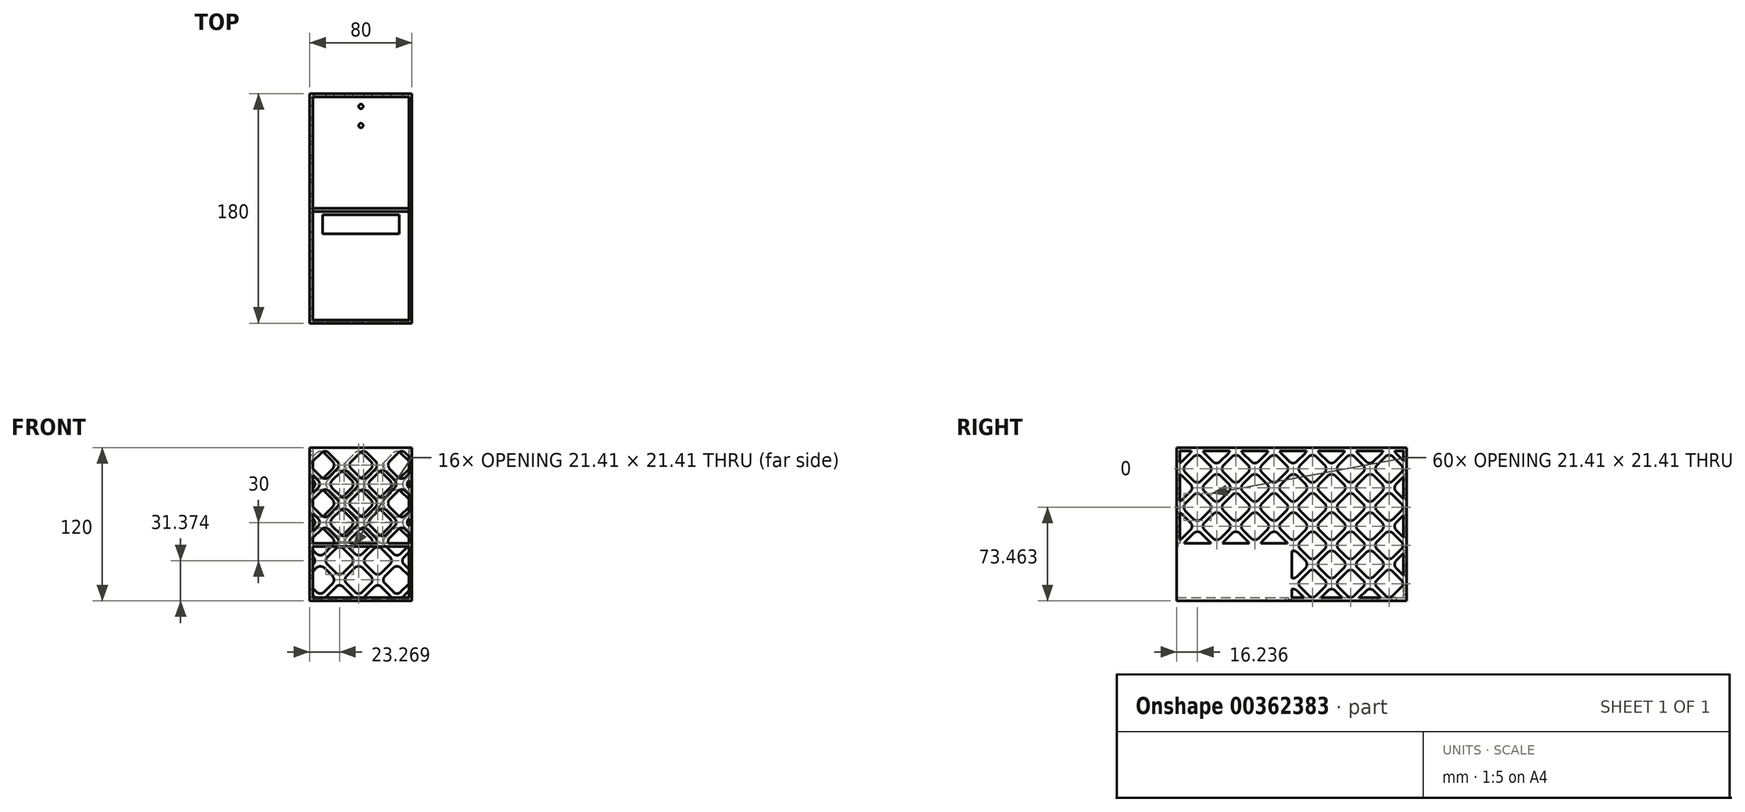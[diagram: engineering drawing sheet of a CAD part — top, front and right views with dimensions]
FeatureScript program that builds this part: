
annotation { "Feature Type Name" : "Feature", "Feature Type Description" : "" }
export const myFeature = defineFeature(function(context is Context, id is Id, definition is map)
    precondition{}
    {
        {
            var Q0;
            Q0=qCreatedBy(makeId("Right.planeOp"),FACE);
            var sketch = newSketch(context, id + "F0", { "sketchPlane" : qUnion([Q0])});
            skLineSegment(sketch, "E0.bottom", {"start": v(-62.96, 61.03) * mm, "end": v(117.04, 61.03) * mm});
            skLineSegment(sketch, "E0.top", {"start": v(-62.96, -58.97) * mm, "end": v(117.04, -58.97) * mm});
            skLineSegment(sketch, "E0.left", {"start": v(-62.96, 61.03) * mm, "end": v(-62.96, -58.97) * mm});
            skLineSegment(sketch, "E0.right", {"start": v(117.04, 61.03) * mm, "end": v(117.04, -58.97) * mm});
            skSolve(sketch);
        }
        {
            var Q0;
            Q0 = qSketchRegion(id + "F0", true);
            extrude(context, id + "F1", {"entities" : qUnion([Q0]), "depth" : 80 * mm});
        }
        {
            var Q0;
            Q0=makeQuery(id+"F1.opExtrude","CAP_FACE",FACE,{"disambiguationData":[OSD([sQuery(id+"F0.wireOp",EDGE,"E0.bottom"),sQuery(id+"F0.wireOp",EDGE,"E0.top"),sQuery(id+"F0.wireOp",EDGE,"E0.left"),sQuery(id+"F0.wireOp",EDGE,"E0.right")])],"isStart":false});
            var sketch = newSketch(context, id + "F2", { "sketchPlane" : qUnion([Q0])});
            skLineSegment(sketch, "E1.bottom", {"start": v(-60.46, 61.03) * mm, "end": v(114.54, 61.03) * mm});
            skLineSegment(sketch, "E1.top", {"start": v(-60.46, -13.97) * mm, "end": v(27.04, -13.97) * mm});
            skLineSegment(sketch, "E1.left", {"start": v(-60.46, 61.03) * mm, "end": v(-60.46, -13.97) * mm});
            skLineSegment(sketch, "E1.right", {"start": v(114.54, 61.03) * mm, "end": v(114.54, -13.97) * mm});
            skLineSegment(sketch, "E2.top", {"start": v(27.04, -56.47) * mm, "end": v(114.54, -56.47) * mm});
            skLineSegment(sketch, "E2.left", {"start": v(27.04, -13.97) * mm, "end": v(27.04, -56.47) * mm});
            skLineSegment(sketch, "E2.right", {"start": v(114.54, 15.9) * mm, "end": v(114.54, -56.47) * mm});
            skSolve(sketch);
        }
        {
            var Q0;
            Q0=makeQuery(id+"F2.imprint","IMPRINT",FACE,{"disambiguationData":[TD([[makeQuery(id+"F2.imprint","IMPRINT",EDGE,{"derivedFrom":sQuery(id+"F2.wireOp",EDGE,"E1.bottom")}),-1.0]])]});
            extrude(context, id + "F3", {"entities" : qUnion([Q0]), "operationType" : NewBodyOperationType.REMOVE, "oppositeDirection" : true, "depth" : 77.5 * mm, "hasSecondDirection" : true, "secondDirectionOppositeDirection" : false, "secondDirectionDepth" : -2.5 * mm});
        }
        {
            var Q0;
            Q0=makeQuery(id+"F1.opExtrude","SWEPT_FACE",FACE,{"disambiguationData":[OSD([sQuery(id+"F0.wireOp",EDGE,"E0.left")])]});
            var sketch = newSketch(context, id + "F4", { "sketchPlane" : qUnion([Q0])});
            skLineSegment(sketch, "E3.bottom", {"start": v(2.5, -16.47) * mm, "end": v(77.5, -16.47) * mm});
            skLineSegment(sketch, "E3.top", {"start": v(2.5, -56.47) * mm, "end": v(77.5, -56.47) * mm});
            skLineSegment(sketch, "E3.left", {"start": v(2.5, -16.47) * mm, "end": v(2.5, -56.47) * mm});
            skLineSegment(sketch, "E3.right", {"start": v(77.5, -16.47) * mm, "end": v(77.5, -56.47) * mm});
            skSolve(sketch);
        }
        {
            var Q0;
            Q0=makeQuery(id+"F4.imprint","IMPRINT",FACE,{"disambiguationData":[TD([[makeQuery(id+"F4.imprint","IMPRINT",EDGE,{"derivedFrom":sQuery(id+"F4.wireOp",EDGE,"E3.bottom")}),-1.0]])]});
            extrude(context, id + "F5", {"entities" : qUnion([Q0]), "operationType" : NewBodyOperationType.REMOVE, "oppositeDirection" : true, "depth" : 87.5 * mm});
        }
        {
            var Q0;
            Q0=makeQuery(id+"F1.opExtrude","CAP_FACE",FACE,{"disambiguationData":[OSD([sQuery(id+"F0.wireOp",EDGE,"E0.bottom"),sQuery(id+"F0.wireOp",EDGE,"E0.top"),sQuery(id+"F0.wireOp",EDGE,"E0.left"),sQuery(id+"F0.wireOp",EDGE,"E0.right")])],"isStart":false});
            var sketch = newSketch(context, id + "F6", { "sketchPlane" : qUnion([Q0])});
            skLineSegment(sketch, "E4", {"start": v(-49.58, 54.02) * mm, "end": v(-56.25, 47.34) * mm});
            skLineSegment(sketch, "E5", {"start": v(-56.25, 41.64) * mm, "end": v(-49.58, 34.97) * mm});
            skLineSegment(sketch, "E6", {"start": v(-43.87, 34.97) * mm, "end": v(-37.2, 41.64) * mm});
            skLineSegment(sketch, "E7", {"start": v(-37.2, 47.34) * mm, "end": v(-43.87, 54.02) * mm});
            skArc(sketch, "E8", {"start": v(-43.87, 54.02) * mm, "mid": v(-46.72, 55.2) * mm, "end": v(-49.58, 54.02) * mm});
            skArc(sketch, "E9", {"start": v(-37.2, 41.64) * mm, "mid": v(-36.02, 44.5) * mm, "end": v(-37.2, 47.34) * mm});
            skArc(sketch, "E10", {"start": v(-56.25, 47.34) * mm, "mid": v(-57.43, 44.5) * mm, "end": v(-56.25, 41.64) * mm});
            skArc(sketch, "E11", {"start": v(-49.58, 34.97) * mm, "mid": v(-46.72, 33.79) * mm, "end": v(-43.87, 34.97) * mm});
            skLineSegment(sketch, "E12", {"start": v(-64.58, 39.02) * mm, "end": v(-71.25, 32.34) * mm});
            skLineSegment(sketch, "E13", {"start": v(-71.25, 26.64) * mm, "end": v(-64.58, 19.97) * mm});
            skLineSegment(sketch, "E14", {"start": v(-58.87, 19.97) * mm, "end": v(-52.2, 26.64) * mm});
            skLineSegment(sketch, "E15", {"start": v(-52.2, 32.34) * mm, "end": v(-58.87, 39.02) * mm});
            skArc(sketch, "E16", {"start": v(-58.87, 39.02) * mm, "mid": v(-61.72, 40.2) * mm, "end": v(-64.58, 39.02) * mm});
            skArc(sketch, "E17", {"start": v(-52.2, 26.64) * mm, "mid": v(-51.02, 29.5) * mm, "end": v(-52.2, 32.34) * mm});
            skArc(sketch, "E18", {"start": v(-71.25, 32.34) * mm, "mid": v(-72.43, 29.5) * mm, "end": v(-71.25, 26.64) * mm});
            skArc(sketch, "E19", {"start": v(-64.58, 19.97) * mm, "mid": v(-61.72, 18.79) * mm, "end": v(-58.87, 19.97) * mm});
            skLineSegment(sketch, "E20.0.1.0", {"start": v(-37.2, 17.34) * mm, "end": v(-43.87, 24.02) * mm});
            skArc(sketch, "E20.0.1.1", {"start": v(-43.87, 24.02) * mm, "mid": v(-46.72, 25.2) * mm, "end": v(-49.58, 24.02) * mm});
            skLineSegment(sketch, "E20.0.1.2", {"start": v(-49.58, 24.02) * mm, "end": v(-56.25, 17.34) * mm});
            skArc(sketch, "E20.0.1.3", {"start": v(-56.25, 17.34) * mm, "mid": v(-57.43, 14.5) * mm, "end": v(-56.25, 11.64) * mm});
            skLineSegment(sketch, "E20.0.1.4", {"start": v(-56.25, 11.64) * mm, "end": v(-49.58, 4.97) * mm});
            skArc(sketch, "E20.0.1.5", {"start": v(-49.58, 4.97) * mm, "mid": v(-46.72, 3.79) * mm, "end": v(-43.87, 4.97) * mm});
            skLineSegment(sketch, "E20.0.1.6", {"start": v(-43.87, 4.97) * mm, "end": v(-37.2, 11.64) * mm});
            skArc(sketch, "E20.0.1.7", {"start": v(-37.2, 11.64) * mm, "mid": v(-36.02, 14.5) * mm, "end": v(-37.2, 17.34) * mm});
            skLineSegment(sketch, "E20.0.1.8", {"start": v(-52.2, 2.34) * mm, "end": v(-58.87, 9.02) * mm});
            skArc(sketch, "E20.0.1.9", {"start": v(-58.87, 9.02) * mm, "mid": v(-61.72, 10.2) * mm, "end": v(-64.58, 9.02) * mm});
            skLineSegment(sketch, "E20.0.1.10", {"start": v(-64.58, 9.02) * mm, "end": v(-71.25, 2.34) * mm});
            skArc(sketch, "E20.0.1.11", {"start": v(-71.25, 2.34) * mm, "mid": v(-72.43, -0.5) * mm, "end": v(-71.25, -3.36) * mm});
            skLineSegment(sketch, "E20.0.1.12", {"start": v(-71.25, -3.36) * mm, "end": v(-64.58, -10.03) * mm});
            skArc(sketch, "E20.0.1.13", {"start": v(-64.58, -10.03) * mm, "mid": v(-61.72, -11.21) * mm, "end": v(-58.87, -10.03) * mm});
            skLineSegment(sketch, "E20.0.1.14", {"start": v(-58.87, -10.03) * mm, "end": v(-52.2, -3.36) * mm});
            skArc(sketch, "E20.0.1.15", {"start": v(-52.2, -3.36) * mm, "mid": v(-51.02, -0.5) * mm, "end": v(-52.2, 2.34) * mm});
            skLineSegment(sketch, "E20.0.2.0", {"start": v(-37.2, -12.66) * mm, "end": v(-43.87, -5.98) * mm});
            skArc(sketch, "E20.0.2.1", {"start": v(-43.87, -5.98) * mm, "mid": v(-46.72, -4.8) * mm, "end": v(-49.58, -5.98) * mm});
            skLineSegment(sketch, "E20.0.2.2", {"start": v(-49.58, -5.98) * mm, "end": v(-56.25, -12.66) * mm});
            skArc(sketch, "E20.0.2.3", {"start": v(-56.25, -12.66) * mm, "mid": v(-57.43, -15.5) * mm, "end": v(-56.25, -18.36) * mm});
            skLineSegment(sketch, "E20.0.2.4", {"start": v(-56.25, -18.36) * mm, "end": v(-49.58, -25.03) * mm});
            skArc(sketch, "E20.0.2.5", {"start": v(-49.58, -25.03) * mm, "mid": v(-46.72, -26.21) * mm, "end": v(-43.87, -25.03) * mm});
            skLineSegment(sketch, "E20.0.2.6", {"start": v(-43.87, -25.03) * mm, "end": v(-37.2, -18.36) * mm});
            skArc(sketch, "E20.0.2.7", {"start": v(-37.2, -18.36) * mm, "mid": v(-36.02, -15.5) * mm, "end": v(-37.2, -12.66) * mm});
            skLineSegment(sketch, "E20.0.2.8", {"start": v(-52.2, -27.66) * mm, "end": v(-58.87, -20.98) * mm});
            skArc(sketch, "E20.0.2.9", {"start": v(-58.87, -20.98) * mm, "mid": v(-61.72, -19.8) * mm, "end": v(-64.58, -20.98) * mm});
            skLineSegment(sketch, "E20.0.2.10", {"start": v(-64.58, -20.98) * mm, "end": v(-71.25, -27.66) * mm});
            skArc(sketch, "E20.0.2.11", {"start": v(-71.25, -27.66) * mm, "mid": v(-72.43, -30.5) * mm, "end": v(-71.25, -33.36) * mm});
            skLineSegment(sketch, "E20.0.2.12", {"start": v(-71.25, -33.36) * mm, "end": v(-64.58, -40.03) * mm});
            skArc(sketch, "E20.0.2.13", {"start": v(-64.58, -40.03) * mm, "mid": v(-61.72, -41.21) * mm, "end": v(-58.87, -40.03) * mm});
            skLineSegment(sketch, "E20.0.2.14", {"start": v(-58.87, -40.03) * mm, "end": v(-52.2, -33.36) * mm});
            skArc(sketch, "E20.0.2.15", {"start": v(-52.2, -33.36) * mm, "mid": v(-51.02, -30.5) * mm, "end": v(-52.2, -27.66) * mm});
            skLineSegment(sketch, "E20.0.3.0", {"start": v(-37.2, -42.66) * mm, "end": v(-43.87, -35.98) * mm});
            skArc(sketch, "E20.0.3.1", {"start": v(-43.87, -35.98) * mm, "mid": v(-46.72, -34.8) * mm, "end": v(-49.58, -35.98) * mm});
            skLineSegment(sketch, "E20.0.3.2", {"start": v(-49.58, -35.98) * mm, "end": v(-56.25, -42.66) * mm});
            skArc(sketch, "E20.0.3.3", {"start": v(-56.25, -42.66) * mm, "mid": v(-57.43, -45.5) * mm, "end": v(-56.25, -48.36) * mm});
            skLineSegment(sketch, "E20.0.3.4", {"start": v(-56.25, -48.36) * mm, "end": v(-49.58, -55.03) * mm});
            skArc(sketch, "E20.0.3.5", {"start": v(-49.58, -55.03) * mm, "mid": v(-46.72, -56.21) * mm, "end": v(-43.87, -55.03) * mm});
            skLineSegment(sketch, "E20.0.3.6", {"start": v(-43.87, -55.03) * mm, "end": v(-37.2, -48.36) * mm});
            skArc(sketch, "E20.0.3.7", {"start": v(-37.2, -48.36) * mm, "mid": v(-36.02, -45.5) * mm, "end": v(-37.2, -42.66) * mm});
            skLineSegment(sketch, "E20.0.3.8", {"start": v(-52.2, -57.66) * mm, "end": v(-58.87, -50.98) * mm});
            skArc(sketch, "E20.0.3.9", {"start": v(-58.87, -50.98) * mm, "mid": v(-61.72, -49.8) * mm, "end": v(-64.58, -50.98) * mm});
            skLineSegment(sketch, "E20.0.3.10", {"start": v(-64.58, -50.98) * mm, "end": v(-71.25, -57.66) * mm});
            skArc(sketch, "E20.0.3.11", {"start": v(-71.25, -57.66) * mm, "mid": v(-72.43, -60.5) * mm, "end": v(-71.25, -63.36) * mm});
            skLineSegment(sketch, "E20.0.3.12", {"start": v(-71.25, -63.36) * mm, "end": v(-64.58, -70.03) * mm});
            skArc(sketch, "E20.0.3.13", {"start": v(-64.58, -70.03) * mm, "mid": v(-61.72, -71.21) * mm, "end": v(-58.87, -70.03) * mm});
            skLineSegment(sketch, "E20.0.3.14", {"start": v(-58.87, -70.03) * mm, "end": v(-52.2, -63.36) * mm});
            skArc(sketch, "E20.0.3.15", {"start": v(-52.2, -63.36) * mm, "mid": v(-51.02, -60.5) * mm, "end": v(-52.2, -57.66) * mm});
            skLineSegment(sketch, "E20.1.0.0", {"start": v(-7.2, 47.34) * mm, "end": v(-13.87, 54.02) * mm});
            skArc(sketch, "E20.1.0.1", {"start": v(-13.87, 54.02) * mm, "mid": v(-16.72, 55.2) * mm, "end": v(-19.58, 54.02) * mm});
            skLineSegment(sketch, "E20.1.0.2", {"start": v(-19.58, 54.02) * mm, "end": v(-26.25, 47.34) * mm});
            skArc(sketch, "E20.1.0.3", {"start": v(-26.25, 47.34) * mm, "mid": v(-27.43, 44.5) * mm, "end": v(-26.25, 41.64) * mm});
            skLineSegment(sketch, "E20.1.0.4", {"start": v(-26.25, 41.64) * mm, "end": v(-19.58, 34.97) * mm});
            skArc(sketch, "E20.1.0.5", {"start": v(-19.58, 34.97) * mm, "mid": v(-16.72, 33.79) * mm, "end": v(-13.87, 34.97) * mm});
            skLineSegment(sketch, "E20.1.0.6", {"start": v(-13.87, 34.97) * mm, "end": v(-7.2, 41.64) * mm});
            skArc(sketch, "E20.1.0.7", {"start": v(-7.2, 41.64) * mm, "mid": v(-6.02, 44.5) * mm, "end": v(-7.2, 47.34) * mm});
            skLineSegment(sketch, "E20.1.0.8", {"start": v(-22.2, 32.34) * mm, "end": v(-28.87, 39.02) * mm});
            skArc(sketch, "E20.1.0.9", {"start": v(-28.87, 39.02) * mm, "mid": v(-31.72, 40.2) * mm, "end": v(-34.58, 39.02) * mm});
            skLineSegment(sketch, "E20.1.0.10", {"start": v(-34.58, 39.02) * mm, "end": v(-41.25, 32.34) * mm});
            skArc(sketch, "E20.1.0.11", {"start": v(-41.25, 32.34) * mm, "mid": v(-42.43, 29.5) * mm, "end": v(-41.25, 26.64) * mm});
            skLineSegment(sketch, "E20.1.0.12", {"start": v(-41.25, 26.64) * mm, "end": v(-34.58, 19.97) * mm});
            skArc(sketch, "E20.1.0.13", {"start": v(-34.58, 19.97) * mm, "mid": v(-31.72, 18.79) * mm, "end": v(-28.87, 19.97) * mm});
            skLineSegment(sketch, "E20.1.0.14", {"start": v(-28.87, 19.97) * mm, "end": v(-22.2, 26.64) * mm});
            skArc(sketch, "E20.1.0.15", {"start": v(-22.2, 26.64) * mm, "mid": v(-21.02, 29.5) * mm, "end": v(-22.2, 32.34) * mm});
            skLineSegment(sketch, "E20.1.1.0", {"start": v(-7.2, 17.34) * mm, "end": v(-13.87, 24.02) * mm});
            skArc(sketch, "E20.1.1.1", {"start": v(-13.87, 24.02) * mm, "mid": v(-16.72, 25.2) * mm, "end": v(-19.58, 24.02) * mm});
            skLineSegment(sketch, "E20.1.1.2", {"start": v(-19.58, 24.02) * mm, "end": v(-26.25, 17.34) * mm});
            skArc(sketch, "E20.1.1.3", {"start": v(-26.25, 17.34) * mm, "mid": v(-27.43, 14.5) * mm, "end": v(-26.25, 11.64) * mm});
            skLineSegment(sketch, "E20.1.1.4", {"start": v(-26.25, 11.64) * mm, "end": v(-19.58, 4.97) * mm});
            skArc(sketch, "E20.1.1.5", {"start": v(-19.58, 4.97) * mm, "mid": v(-16.72, 3.79) * mm, "end": v(-13.87, 4.97) * mm});
            skLineSegment(sketch, "E20.1.1.6", {"start": v(-13.87, 4.97) * mm, "end": v(-7.2, 11.64) * mm});
            skArc(sketch, "E20.1.1.7", {"start": v(-7.2, 11.64) * mm, "mid": v(-6.02, 14.5) * mm, "end": v(-7.2, 17.34) * mm});
            skLineSegment(sketch, "E20.1.1.8", {"start": v(-22.2, 2.34) * mm, "end": v(-28.87, 9.02) * mm});
            skArc(sketch, "E20.1.1.9", {"start": v(-28.87, 9.02) * mm, "mid": v(-31.72, 10.2) * mm, "end": v(-34.58, 9.02) * mm});
            skLineSegment(sketch, "E20.1.1.10", {"start": v(-34.58, 9.02) * mm, "end": v(-41.25, 2.34) * mm});
            skArc(sketch, "E20.1.1.11", {"start": v(-41.25, 2.34) * mm, "mid": v(-42.43, -0.5) * mm, "end": v(-41.25, -3.36) * mm});
            skLineSegment(sketch, "E20.1.1.12", {"start": v(-41.25, -3.36) * mm, "end": v(-34.58, -10.03) * mm});
            skArc(sketch, "E20.1.1.13", {"start": v(-34.58, -10.03) * mm, "mid": v(-31.72, -11.21) * mm, "end": v(-28.87, -10.03) * mm});
            skLineSegment(sketch, "E20.1.1.14", {"start": v(-28.87, -10.03) * mm, "end": v(-22.2, -3.36) * mm});
            skArc(sketch, "E20.1.1.15", {"start": v(-22.2, -3.36) * mm, "mid": v(-21.02, -0.5) * mm, "end": v(-22.2, 2.34) * mm});
            skLineSegment(sketch, "E20.1.2.0", {"start": v(-7.2, -12.66) * mm, "end": v(-13.87, -5.98) * mm});
            skArc(sketch, "E20.1.2.1", {"start": v(-13.87, -5.98) * mm, "mid": v(-16.72, -4.8) * mm, "end": v(-19.58, -5.98) * mm});
            skLineSegment(sketch, "E20.1.2.2", {"start": v(-19.58, -5.98) * mm, "end": v(-26.25, -12.66) * mm});
            skArc(sketch, "E20.1.2.3", {"start": v(-26.25, -12.66) * mm, "mid": v(-27.43, -15.5) * mm, "end": v(-26.25, -18.36) * mm});
            skLineSegment(sketch, "E20.1.2.4", {"start": v(-26.25, -18.36) * mm, "end": v(-19.58, -25.03) * mm});
            skArc(sketch, "E20.1.2.5", {"start": v(-19.58, -25.03) * mm, "mid": v(-16.72, -26.21) * mm, "end": v(-13.87, -25.03) * mm});
            skLineSegment(sketch, "E20.1.2.6", {"start": v(-13.87, -25.03) * mm, "end": v(-7.2, -18.36) * mm});
            skArc(sketch, "E20.1.2.7", {"start": v(-7.2, -18.36) * mm, "mid": v(-6.02, -15.5) * mm, "end": v(-7.2, -12.66) * mm});
            skLineSegment(sketch, "E20.1.2.8", {"start": v(-22.2, -27.66) * mm, "end": v(-28.87, -20.98) * mm});
            skArc(sketch, "E20.1.2.9", {"start": v(-28.87, -20.98) * mm, "mid": v(-31.72, -19.8) * mm, "end": v(-34.58, -20.98) * mm});
            skLineSegment(sketch, "E20.1.2.10", {"start": v(-34.58, -20.98) * mm, "end": v(-41.25, -27.66) * mm});
            skArc(sketch, "E20.1.2.11", {"start": v(-41.25, -27.66) * mm, "mid": v(-42.43, -30.5) * mm, "end": v(-41.25, -33.36) * mm});
            skLineSegment(sketch, "E20.1.2.12", {"start": v(-41.25, -33.36) * mm, "end": v(-34.58, -40.03) * mm});
            skArc(sketch, "E20.1.2.13", {"start": v(-34.58, -40.03) * mm, "mid": v(-31.72, -41.21) * mm, "end": v(-28.87, -40.03) * mm});
            skLineSegment(sketch, "E20.1.2.14", {"start": v(-28.87, -40.03) * mm, "end": v(-22.2, -33.36) * mm});
            skArc(sketch, "E20.1.2.15", {"start": v(-22.2, -33.36) * mm, "mid": v(-21.02, -30.5) * mm, "end": v(-22.2, -27.66) * mm});
            skLineSegment(sketch, "E20.1.3.0", {"start": v(-7.2, -42.66) * mm, "end": v(-13.87, -35.98) * mm});
            skArc(sketch, "E20.1.3.1", {"start": v(-13.87, -35.98) * mm, "mid": v(-16.72, -34.8) * mm, "end": v(-19.58, -35.98) * mm});
            skLineSegment(sketch, "E20.1.3.2", {"start": v(-19.58, -35.98) * mm, "end": v(-26.25, -42.66) * mm});
            skArc(sketch, "E20.1.3.3", {"start": v(-26.25, -42.66) * mm, "mid": v(-27.43, -45.5) * mm, "end": v(-26.25, -48.36) * mm});
            skLineSegment(sketch, "E20.1.3.4", {"start": v(-26.25, -48.36) * mm, "end": v(-19.58, -55.03) * mm});
            skArc(sketch, "E20.1.3.5", {"start": v(-19.58, -55.03) * mm, "mid": v(-16.72, -56.21) * mm, "end": v(-13.87, -55.03) * mm});
            skLineSegment(sketch, "E20.1.3.6", {"start": v(-13.87, -55.03) * mm, "end": v(-7.2, -48.36) * mm});
            skArc(sketch, "E20.1.3.7", {"start": v(-7.2, -48.36) * mm, "mid": v(-6.02, -45.5) * mm, "end": v(-7.2, -42.66) * mm});
            skLineSegment(sketch, "E20.1.3.8", {"start": v(-22.2, -57.66) * mm, "end": v(-28.87, -50.98) * mm});
            skArc(sketch, "E20.1.3.9", {"start": v(-28.87, -50.98) * mm, "mid": v(-31.72, -49.8) * mm, "end": v(-34.58, -50.98) * mm});
            skLineSegment(sketch, "E20.1.3.10", {"start": v(-34.58, -50.98) * mm, "end": v(-41.25, -57.66) * mm});
            skArc(sketch, "E20.1.3.11", {"start": v(-41.25, -57.66) * mm, "mid": v(-42.43, -60.5) * mm, "end": v(-41.25, -63.36) * mm});
            skLineSegment(sketch, "E20.1.3.12", {"start": v(-41.25, -63.36) * mm, "end": v(-34.58, -70.03) * mm});
            skArc(sketch, "E20.1.3.13", {"start": v(-34.58, -70.03) * mm, "mid": v(-31.72, -71.21) * mm, "end": v(-28.87, -70.03) * mm});
            skLineSegment(sketch, "E20.1.3.14", {"start": v(-28.87, -70.03) * mm, "end": v(-22.2, -63.36) * mm});
            skArc(sketch, "E20.1.3.15", {"start": v(-22.2, -63.36) * mm, "mid": v(-21.02, -60.5) * mm, "end": v(-22.2, -57.66) * mm});
            skLineSegment(sketch, "E20.2.0.0", {"start": v(22.8, 47.34) * mm, "end": v(16.13, 54.02) * mm});
            skArc(sketch, "E20.2.0.1", {"start": v(16.13, 54.02) * mm, "mid": v(13.28, 55.2) * mm, "end": v(10.42, 54.02) * mm});
            skLineSegment(sketch, "E20.2.0.2", {"start": v(10.42, 54.02) * mm, "end": v(3.75, 47.34) * mm});
            skArc(sketch, "E20.2.0.3", {"start": v(3.75, 47.34) * mm, "mid": v(2.57, 44.5) * mm, "end": v(3.75, 41.64) * mm});
            skLineSegment(sketch, "E20.2.0.4", {"start": v(3.75, 41.64) * mm, "end": v(10.42, 34.97) * mm});
            skArc(sketch, "E20.2.0.5", {"start": v(10.42, 34.97) * mm, "mid": v(13.28, 33.79) * mm, "end": v(16.13, 34.97) * mm});
            skLineSegment(sketch, "E20.2.0.6", {"start": v(16.13, 34.97) * mm, "end": v(22.8, 41.64) * mm});
            skArc(sketch, "E20.2.0.7", {"start": v(22.8, 41.64) * mm, "mid": v(23.98, 44.5) * mm, "end": v(22.8, 47.34) * mm});
            skLineSegment(sketch, "E20.2.0.8", {"start": v(7.8, 32.34) * mm, "end": v(1.13, 39.02) * mm});
            skArc(sketch, "E20.2.0.9", {"start": v(1.13, 39.02) * mm, "mid": v(-1.72, 40.2) * mm, "end": v(-4.58, 39.02) * mm});
            skLineSegment(sketch, "E20.2.0.10", {"start": v(-4.58, 39.02) * mm, "end": v(-11.25, 32.34) * mm});
            skArc(sketch, "E20.2.0.11", {"start": v(-11.25, 32.34) * mm, "mid": v(-12.43, 29.5) * mm, "end": v(-11.25, 26.64) * mm});
            skLineSegment(sketch, "E20.2.0.12", {"start": v(-11.25, 26.64) * mm, "end": v(-4.58, 19.97) * mm});
            skArc(sketch, "E20.2.0.13", {"start": v(-4.58, 19.97) * mm, "mid": v(-1.72, 18.79) * mm, "end": v(1.13, 19.97) * mm});
            skLineSegment(sketch, "E20.2.0.14", {"start": v(1.13, 19.97) * mm, "end": v(7.8, 26.64) * mm});
            skArc(sketch, "E20.2.0.15", {"start": v(7.8, 26.64) * mm, "mid": v(8.98, 29.5) * mm, "end": v(7.8, 32.34) * mm});
            skLineSegment(sketch, "E20.2.1.0", {"start": v(22.8, 17.34) * mm, "end": v(16.13, 24.02) * mm});
            skArc(sketch, "E20.2.1.1", {"start": v(16.13, 24.02) * mm, "mid": v(13.28, 25.2) * mm, "end": v(10.42, 24.02) * mm});
            skLineSegment(sketch, "E20.2.1.2", {"start": v(10.42, 24.02) * mm, "end": v(3.75, 17.34) * mm});
            skArc(sketch, "E20.2.1.3", {"start": v(3.75, 17.34) * mm, "mid": v(2.57, 14.5) * mm, "end": v(3.75, 11.64) * mm});
            skLineSegment(sketch, "E20.2.1.4", {"start": v(3.75, 11.64) * mm, "end": v(10.42, 4.97) * mm});
            skArc(sketch, "E20.2.1.5", {"start": v(10.42, 4.97) * mm, "mid": v(13.28, 3.79) * mm, "end": v(16.13, 4.97) * mm});
            skLineSegment(sketch, "E20.2.1.6", {"start": v(16.13, 4.97) * mm, "end": v(22.8, 11.64) * mm});
            skArc(sketch, "E20.2.1.7", {"start": v(22.8, 11.64) * mm, "mid": v(23.98, 14.5) * mm, "end": v(22.8, 17.34) * mm});
            skLineSegment(sketch, "E20.2.1.8", {"start": v(7.8, 2.34) * mm, "end": v(1.13, 9.02) * mm});
            skArc(sketch, "E20.2.1.9", {"start": v(1.13, 9.02) * mm, "mid": v(-1.72, 10.2) * mm, "end": v(-4.58, 9.02) * mm});
            skLineSegment(sketch, "E20.2.1.10", {"start": v(-4.58, 9.02) * mm, "end": v(-11.25, 2.34) * mm});
            skArc(sketch, "E20.2.1.11", {"start": v(-11.25, 2.34) * mm, "mid": v(-12.43, -0.5) * mm, "end": v(-11.25, -3.36) * mm});
            skLineSegment(sketch, "E20.2.1.12", {"start": v(-11.25, -3.36) * mm, "end": v(-4.58, -10.03) * mm});
            skArc(sketch, "E20.2.1.13", {"start": v(-4.58, -10.03) * mm, "mid": v(-1.72, -11.21) * mm, "end": v(1.13, -10.03) * mm});
            skLineSegment(sketch, "E20.2.1.14", {"start": v(1.13, -10.03) * mm, "end": v(7.8, -3.36) * mm});
            skArc(sketch, "E20.2.1.15", {"start": v(7.8, -3.36) * mm, "mid": v(8.98, -0.5) * mm, "end": v(7.8, 2.34) * mm});
            skLineSegment(sketch, "E20.2.2.0", {"start": v(22.8, -12.66) * mm, "end": v(16.13, -5.98) * mm});
            skArc(sketch, "E20.2.2.1", {"start": v(16.13, -5.98) * mm, "mid": v(13.28, -4.8) * mm, "end": v(10.42, -5.98) * mm});
            skLineSegment(sketch, "E20.2.2.2", {"start": v(10.42, -5.98) * mm, "end": v(3.75, -12.66) * mm});
            skArc(sketch, "E20.2.2.3", {"start": v(3.75, -12.66) * mm, "mid": v(2.57, -15.5) * mm, "end": v(3.75, -18.36) * mm});
            skLineSegment(sketch, "E20.2.2.4", {"start": v(3.75, -18.36) * mm, "end": v(10.42, -25.03) * mm});
            skArc(sketch, "E20.2.2.5", {"start": v(10.42, -25.03) * mm, "mid": v(13.28, -26.21) * mm, "end": v(16.13, -25.03) * mm});
            skLineSegment(sketch, "E20.2.2.6", {"start": v(16.13, -25.03) * mm, "end": v(22.8, -18.36) * mm});
            skArc(sketch, "E20.2.2.7", {"start": v(22.8, -18.36) * mm, "mid": v(23.98, -15.5) * mm, "end": v(22.8, -12.66) * mm});
            skLineSegment(sketch, "E20.2.2.8", {"start": v(7.8, -27.66) * mm, "end": v(1.13, -20.98) * mm});
            skArc(sketch, "E20.2.2.9", {"start": v(1.13, -20.98) * mm, "mid": v(-1.72, -19.8) * mm, "end": v(-4.58, -20.98) * mm});
            skLineSegment(sketch, "E20.2.2.10", {"start": v(-4.58, -20.98) * mm, "end": v(-11.25, -27.66) * mm});
            skArc(sketch, "E20.2.2.11", {"start": v(-11.25, -27.66) * mm, "mid": v(-12.43, -30.5) * mm, "end": v(-11.25, -33.36) * mm});
            skLineSegment(sketch, "E20.2.2.12", {"start": v(-11.25, -33.36) * mm, "end": v(-4.58, -40.03) * mm});
            skArc(sketch, "E20.2.2.13", {"start": v(-4.58, -40.03) * mm, "mid": v(-1.72, -41.21) * mm, "end": v(1.13, -40.03) * mm});
            skLineSegment(sketch, "E20.2.2.14", {"start": v(1.13, -40.03) * mm, "end": v(7.8, -33.36) * mm});
            skArc(sketch, "E20.2.2.15", {"start": v(7.8, -33.36) * mm, "mid": v(8.98, -30.5) * mm, "end": v(7.8, -27.66) * mm});
            skLineSegment(sketch, "E20.2.3.0", {"start": v(22.8, -42.66) * mm, "end": v(16.13, -35.98) * mm});
            skArc(sketch, "E20.2.3.1", {"start": v(16.13, -35.98) * mm, "mid": v(13.28, -34.8) * mm, "end": v(10.42, -35.98) * mm});
            skLineSegment(sketch, "E20.2.3.2", {"start": v(10.42, -35.98) * mm, "end": v(3.75, -42.66) * mm});
            skArc(sketch, "E20.2.3.3", {"start": v(3.75, -42.66) * mm, "mid": v(2.57, -45.5) * mm, "end": v(3.75, -48.36) * mm});
            skLineSegment(sketch, "E20.2.3.4", {"start": v(3.75, -48.36) * mm, "end": v(10.42, -55.03) * mm});
            skArc(sketch, "E20.2.3.5", {"start": v(10.42, -55.03) * mm, "mid": v(13.28, -56.21) * mm, "end": v(16.13, -55.03) * mm});
            skLineSegment(sketch, "E20.2.3.6", {"start": v(16.13, -55.03) * mm, "end": v(22.8, -48.36) * mm});
            skArc(sketch, "E20.2.3.7", {"start": v(22.8, -48.36) * mm, "mid": v(23.98, -45.5) * mm, "end": v(22.8, -42.66) * mm});
            skLineSegment(sketch, "E20.2.3.8", {"start": v(7.8, -57.66) * mm, "end": v(1.13, -50.98) * mm});
            skArc(sketch, "E20.2.3.9", {"start": v(1.13, -50.98) * mm, "mid": v(-1.72, -49.8) * mm, "end": v(-4.58, -50.98) * mm});
            skLineSegment(sketch, "E20.2.3.10", {"start": v(-4.58, -50.98) * mm, "end": v(-11.25, -57.66) * mm});
            skArc(sketch, "E20.2.3.11", {"start": v(-11.25, -57.66) * mm, "mid": v(-12.43, -60.5) * mm, "end": v(-11.25, -63.36) * mm});
            skLineSegment(sketch, "E20.2.3.12", {"start": v(-11.25, -63.36) * mm, "end": v(-4.58, -70.03) * mm});
            skArc(sketch, "E20.2.3.13", {"start": v(-4.58, -70.03) * mm, "mid": v(-1.72, -71.21) * mm, "end": v(1.13, -70.03) * mm});
            skLineSegment(sketch, "E20.2.3.14", {"start": v(1.13, -70.03) * mm, "end": v(7.8, -63.36) * mm});
            skArc(sketch, "E20.2.3.15", {"start": v(7.8, -63.36) * mm, "mid": v(8.98, -60.5) * mm, "end": v(7.8, -57.66) * mm});
            skLineSegment(sketch, "E20.3.0.0", {"start": v(52.8, 47.34) * mm, "end": v(46.13, 54.02) * mm});
            skArc(sketch, "E20.3.0.1", {"start": v(46.13, 54.02) * mm, "mid": v(43.28, 55.2) * mm, "end": v(40.42, 54.02) * mm});
            skLineSegment(sketch, "E20.3.0.2", {"start": v(40.42, 54.02) * mm, "end": v(33.75, 47.34) * mm});
            skArc(sketch, "E20.3.0.3", {"start": v(33.75, 47.34) * mm, "mid": v(32.57, 44.5) * mm, "end": v(33.75, 41.64) * mm});
            skLineSegment(sketch, "E20.3.0.4", {"start": v(33.75, 41.64) * mm, "end": v(40.42, 34.97) * mm});
            skArc(sketch, "E20.3.0.5", {"start": v(40.42, 34.97) * mm, "mid": v(43.28, 33.79) * mm, "end": v(46.13, 34.97) * mm});
            skLineSegment(sketch, "E20.3.0.6", {"start": v(46.13, 34.97) * mm, "end": v(52.8, 41.64) * mm});
            skArc(sketch, "E20.3.0.7", {"start": v(52.8, 41.64) * mm, "mid": v(53.98, 44.5) * mm, "end": v(52.8, 47.34) * mm});
            skLineSegment(sketch, "E20.3.0.8", {"start": v(37.8, 32.34) * mm, "end": v(31.13, 39.02) * mm});
            skArc(sketch, "E20.3.0.9", {"start": v(31.13, 39.02) * mm, "mid": v(28.28, 40.2) * mm, "end": v(25.42, 39.02) * mm});
            skLineSegment(sketch, "E20.3.0.10", {"start": v(25.42, 39.02) * mm, "end": v(18.75, 32.34) * mm});
            skArc(sketch, "E20.3.0.11", {"start": v(18.75, 32.34) * mm, "mid": v(17.57, 29.5) * mm, "end": v(18.75, 26.64) * mm});
            skLineSegment(sketch, "E20.3.0.12", {"start": v(18.75, 26.64) * mm, "end": v(25.42, 19.97) * mm});
            skArc(sketch, "E20.3.0.13", {"start": v(25.42, 19.97) * mm, "mid": v(28.28, 18.79) * mm, "end": v(31.13, 19.97) * mm});
            skLineSegment(sketch, "E20.3.0.14", {"start": v(31.13, 19.97) * mm, "end": v(37.8, 26.64) * mm});
            skArc(sketch, "E20.3.0.15", {"start": v(37.8, 26.64) * mm, "mid": v(38.98, 29.5) * mm, "end": v(37.8, 32.34) * mm});
            skLineSegment(sketch, "E20.3.1.0", {"start": v(52.8, 17.34) * mm, "end": v(46.13, 24.02) * mm});
            skArc(sketch, "E20.3.1.1", {"start": v(46.13, 24.02) * mm, "mid": v(43.28, 25.2) * mm, "end": v(40.42, 24.02) * mm});
            skLineSegment(sketch, "E20.3.1.2", {"start": v(40.42, 24.02) * mm, "end": v(33.75, 17.34) * mm});
            skArc(sketch, "E20.3.1.3", {"start": v(33.75, 17.34) * mm, "mid": v(32.57, 14.5) * mm, "end": v(33.75, 11.64) * mm});
            skLineSegment(sketch, "E20.3.1.4", {"start": v(33.75, 11.64) * mm, "end": v(40.42, 4.97) * mm});
            skArc(sketch, "E20.3.1.5", {"start": v(40.42, 4.97) * mm, "mid": v(43.28, 3.79) * mm, "end": v(46.13, 4.97) * mm});
            skLineSegment(sketch, "E20.3.1.6", {"start": v(46.13, 4.97) * mm, "end": v(52.8, 11.64) * mm});
            skArc(sketch, "E20.3.1.7", {"start": v(52.8, 11.64) * mm, "mid": v(53.98, 14.5) * mm, "end": v(52.8, 17.34) * mm});
            skLineSegment(sketch, "E20.3.1.8", {"start": v(37.8, 2.34) * mm, "end": v(31.13, 9.02) * mm});
            skArc(sketch, "E20.3.1.9", {"start": v(31.13, 9.02) * mm, "mid": v(28.28, 10.2) * mm, "end": v(25.42, 9.02) * mm});
            skLineSegment(sketch, "E20.3.1.10", {"start": v(25.42, 9.02) * mm, "end": v(18.75, 2.34) * mm});
            skArc(sketch, "E20.3.1.11", {"start": v(18.75, 2.34) * mm, "mid": v(17.57, -0.5) * mm, "end": v(18.75, -3.36) * mm});
            skLineSegment(sketch, "E20.3.1.12", {"start": v(18.75, -3.36) * mm, "end": v(25.42, -10.03) * mm});
            skArc(sketch, "E20.3.1.13", {"start": v(25.42, -10.03) * mm, "mid": v(28.28, -11.21) * mm, "end": v(31.13, -10.03) * mm});
            skLineSegment(sketch, "E20.3.1.14", {"start": v(31.13, -10.03) * mm, "end": v(37.8, -3.36) * mm});
            skArc(sketch, "E20.3.1.15", {"start": v(37.8, -3.36) * mm, "mid": v(38.98, -0.5) * mm, "end": v(37.8, 2.34) * mm});
            skLineSegment(sketch, "E20.3.2.0", {"start": v(52.8, -12.66) * mm, "end": v(46.13, -5.98) * mm});
            skArc(sketch, "E20.3.2.1", {"start": v(46.13, -5.98) * mm, "mid": v(43.28, -4.8) * mm, "end": v(40.42, -5.98) * mm});
            skLineSegment(sketch, "E20.3.2.2", {"start": v(40.42, -5.98) * mm, "end": v(33.75, -12.66) * mm});
            skArc(sketch, "E20.3.2.3", {"start": v(33.75, -12.66) * mm, "mid": v(32.57, -15.5) * mm, "end": v(33.75, -18.36) * mm});
            skLineSegment(sketch, "E20.3.2.4", {"start": v(33.75, -18.36) * mm, "end": v(40.42, -25.03) * mm});
            skArc(sketch, "E20.3.2.5", {"start": v(40.42, -25.03) * mm, "mid": v(43.28, -26.21) * mm, "end": v(46.13, -25.03) * mm});
            skLineSegment(sketch, "E20.3.2.6", {"start": v(46.13, -25.03) * mm, "end": v(52.8, -18.36) * mm});
            skArc(sketch, "E20.3.2.7", {"start": v(52.8, -18.36) * mm, "mid": v(53.98, -15.5) * mm, "end": v(52.8, -12.66) * mm});
            skLineSegment(sketch, "E20.3.2.8", {"start": v(37.8, -27.66) * mm, "end": v(31.13, -20.98) * mm});
            skArc(sketch, "E20.3.2.9", {"start": v(31.13, -20.98) * mm, "mid": v(28.28, -19.8) * mm, "end": v(25.42, -20.98) * mm});
            skLineSegment(sketch, "E20.3.2.10", {"start": v(25.42, -20.98) * mm, "end": v(18.75, -27.66) * mm});
            skArc(sketch, "E20.3.2.11", {"start": v(18.75, -27.66) * mm, "mid": v(17.57, -30.5) * mm, "end": v(18.75, -33.36) * mm});
            skLineSegment(sketch, "E20.3.2.12", {"start": v(18.75, -33.36) * mm, "end": v(25.42, -40.03) * mm});
            skArc(sketch, "E20.3.2.13", {"start": v(25.42, -40.03) * mm, "mid": v(28.28, -41.21) * mm, "end": v(31.13, -40.03) * mm});
            skLineSegment(sketch, "E20.3.2.14", {"start": v(31.13, -40.03) * mm, "end": v(37.8, -33.36) * mm});
            skArc(sketch, "E20.3.2.15", {"start": v(37.8, -33.36) * mm, "mid": v(38.98, -30.5) * mm, "end": v(37.8, -27.66) * mm});
            skLineSegment(sketch, "E20.3.3.0", {"start": v(52.8, -42.66) * mm, "end": v(46.13, -35.98) * mm});
            skArc(sketch, "E20.3.3.1", {"start": v(46.13, -35.98) * mm, "mid": v(43.28, -34.8) * mm, "end": v(40.42, -35.98) * mm});
            skLineSegment(sketch, "E20.3.3.2", {"start": v(40.42, -35.98) * mm, "end": v(33.75, -42.66) * mm});
            skArc(sketch, "E20.3.3.3", {"start": v(33.75, -42.66) * mm, "mid": v(32.57, -45.5) * mm, "end": v(33.75, -48.36) * mm});
            skLineSegment(sketch, "E20.3.3.4", {"start": v(33.75, -48.36) * mm, "end": v(40.42, -55.03) * mm});
            skArc(sketch, "E20.3.3.5", {"start": v(40.42, -55.03) * mm, "mid": v(43.28, -56.21) * mm, "end": v(46.13, -55.03) * mm});
            skLineSegment(sketch, "E20.3.3.6", {"start": v(46.13, -55.03) * mm, "end": v(52.8, -48.36) * mm});
            skArc(sketch, "E20.3.3.7", {"start": v(52.8, -48.36) * mm, "mid": v(53.98, -45.5) * mm, "end": v(52.8, -42.66) * mm});
            skLineSegment(sketch, "E20.3.3.8", {"start": v(37.8, -57.66) * mm, "end": v(31.13, -50.98) * mm});
            skArc(sketch, "E20.3.3.9", {"start": v(31.13, -50.98) * mm, "mid": v(28.28, -49.8) * mm, "end": v(25.42, -50.98) * mm});
            skLineSegment(sketch, "E20.3.3.10", {"start": v(25.42, -50.98) * mm, "end": v(18.75, -57.66) * mm});
            skArc(sketch, "E20.3.3.11", {"start": v(18.75, -57.66) * mm, "mid": v(17.57, -60.5) * mm, "end": v(18.75, -63.36) * mm});
            skLineSegment(sketch, "E20.3.3.12", {"start": v(18.75, -63.36) * mm, "end": v(25.42, -70.03) * mm});
            skArc(sketch, "E20.3.3.13", {"start": v(25.42, -70.03) * mm, "mid": v(28.28, -71.21) * mm, "end": v(31.13, -70.03) * mm});
            skLineSegment(sketch, "E20.3.3.14", {"start": v(31.13, -70.03) * mm, "end": v(37.8, -63.36) * mm});
            skArc(sketch, "E20.3.3.15", {"start": v(37.8, -63.36) * mm, "mid": v(38.98, -60.5) * mm, "end": v(37.8, -57.66) * mm});
            skLineSegment(sketch, "E20.4.0.0", {"start": v(82.8, 47.34) * mm, "end": v(76.13, 54.02) * mm});
            skArc(sketch, "E20.4.0.1", {"start": v(76.13, 54.02) * mm, "mid": v(73.28, 55.2) * mm, "end": v(70.42, 54.02) * mm});
            skLineSegment(sketch, "E20.4.0.2", {"start": v(70.42, 54.02) * mm, "end": v(63.75, 47.34) * mm});
            skArc(sketch, "E20.4.0.3", {"start": v(63.75, 47.34) * mm, "mid": v(62.57, 44.5) * mm, "end": v(63.75, 41.64) * mm});
            skLineSegment(sketch, "E20.4.0.4", {"start": v(63.75, 41.64) * mm, "end": v(70.42, 34.97) * mm});
            skArc(sketch, "E20.4.0.5", {"start": v(70.42, 34.97) * mm, "mid": v(73.28, 33.79) * mm, "end": v(76.13, 34.97) * mm});
            skLineSegment(sketch, "E20.4.0.6", {"start": v(76.13, 34.97) * mm, "end": v(82.8, 41.64) * mm});
            skArc(sketch, "E20.4.0.7", {"start": v(82.8, 41.64) * mm, "mid": v(83.98, 44.5) * mm, "end": v(82.8, 47.34) * mm});
            skLineSegment(sketch, "E20.4.0.8", {"start": v(67.8, 32.34) * mm, "end": v(61.13, 39.02) * mm});
            skArc(sketch, "E20.4.0.9", {"start": v(61.13, 39.02) * mm, "mid": v(58.28, 40.2) * mm, "end": v(55.42, 39.02) * mm});
            skLineSegment(sketch, "E20.4.0.10", {"start": v(55.42, 39.02) * mm, "end": v(48.75, 32.34) * mm});
            skArc(sketch, "E20.4.0.11", {"start": v(48.75, 32.34) * mm, "mid": v(47.57, 29.5) * mm, "end": v(48.75, 26.64) * mm});
            skLineSegment(sketch, "E20.4.0.12", {"start": v(48.75, 26.64) * mm, "end": v(55.42, 19.97) * mm});
            skArc(sketch, "E20.4.0.13", {"start": v(55.42, 19.97) * mm, "mid": v(58.28, 18.79) * mm, "end": v(61.13, 19.97) * mm});
            skLineSegment(sketch, "E20.4.0.14", {"start": v(61.13, 19.97) * mm, "end": v(67.8, 26.64) * mm});
            skArc(sketch, "E20.4.0.15", {"start": v(67.8, 26.64) * mm, "mid": v(68.98, 29.5) * mm, "end": v(67.8, 32.34) * mm});
            skLineSegment(sketch, "E20.4.1.0", {"start": v(82.8, 17.34) * mm, "end": v(76.13, 24.02) * mm});
            skArc(sketch, "E20.4.1.1", {"start": v(76.13, 24.02) * mm, "mid": v(73.28, 25.2) * mm, "end": v(70.42, 24.02) * mm});
            skLineSegment(sketch, "E20.4.1.2", {"start": v(70.42, 24.02) * mm, "end": v(63.75, 17.34) * mm});
            skArc(sketch, "E20.4.1.3", {"start": v(63.75, 17.34) * mm, "mid": v(62.57, 14.5) * mm, "end": v(63.75, 11.64) * mm});
            skLineSegment(sketch, "E20.4.1.4", {"start": v(63.75, 11.64) * mm, "end": v(70.42, 4.97) * mm});
            skArc(sketch, "E20.4.1.5", {"start": v(70.42, 4.97) * mm, "mid": v(73.28, 3.79) * mm, "end": v(76.13, 4.97) * mm});
            skLineSegment(sketch, "E20.4.1.6", {"start": v(76.13, 4.97) * mm, "end": v(82.8, 11.64) * mm});
            skArc(sketch, "E20.4.1.7", {"start": v(82.8, 11.64) * mm, "mid": v(83.98, 14.5) * mm, "end": v(82.8, 17.34) * mm});
            skLineSegment(sketch, "E20.4.1.8", {"start": v(67.8, 2.34) * mm, "end": v(61.13, 9.02) * mm});
            skArc(sketch, "E20.4.1.9", {"start": v(61.13, 9.02) * mm, "mid": v(58.28, 10.2) * mm, "end": v(55.42, 9.02) * mm});
            skLineSegment(sketch, "E20.4.1.10", {"start": v(55.42, 9.02) * mm, "end": v(48.75, 2.34) * mm});
            skArc(sketch, "E20.4.1.11", {"start": v(48.75, 2.34) * mm, "mid": v(47.57, -0.5) * mm, "end": v(48.75, -3.36) * mm});
            skLineSegment(sketch, "E20.4.1.12", {"start": v(48.75, -3.36) * mm, "end": v(55.42, -10.03) * mm});
            skArc(sketch, "E20.4.1.13", {"start": v(55.42, -10.03) * mm, "mid": v(58.28, -11.21) * mm, "end": v(61.13, -10.03) * mm});
            skLineSegment(sketch, "E20.4.1.14", {"start": v(61.13, -10.03) * mm, "end": v(67.8, -3.36) * mm});
            skArc(sketch, "E20.4.1.15", {"start": v(67.8, -3.36) * mm, "mid": v(68.98, -0.5) * mm, "end": v(67.8, 2.34) * mm});
            skLineSegment(sketch, "E20.4.2.0", {"start": v(82.8, -12.66) * mm, "end": v(76.13, -5.98) * mm});
            skArc(sketch, "E20.4.2.1", {"start": v(76.13, -5.98) * mm, "mid": v(73.28, -4.8) * mm, "end": v(70.42, -5.98) * mm});
            skLineSegment(sketch, "E20.4.2.2", {"start": v(70.42, -5.98) * mm, "end": v(63.75, -12.66) * mm});
            skArc(sketch, "E20.4.2.3", {"start": v(63.75, -12.66) * mm, "mid": v(62.57, -15.5) * mm, "end": v(63.75, -18.36) * mm});
            skLineSegment(sketch, "E20.4.2.4", {"start": v(63.75, -18.36) * mm, "end": v(70.42, -25.03) * mm});
            skArc(sketch, "E20.4.2.5", {"start": v(70.42, -25.03) * mm, "mid": v(73.28, -26.21) * mm, "end": v(76.13, -25.03) * mm});
            skLineSegment(sketch, "E20.4.2.6", {"start": v(76.13, -25.03) * mm, "end": v(82.8, -18.36) * mm});
            skArc(sketch, "E20.4.2.7", {"start": v(82.8, -18.36) * mm, "mid": v(83.98, -15.5) * mm, "end": v(82.8, -12.66) * mm});
            skLineSegment(sketch, "E20.4.2.8", {"start": v(67.8, -27.66) * mm, "end": v(61.13, -20.98) * mm});
            skArc(sketch, "E20.4.2.9", {"start": v(61.13, -20.98) * mm, "mid": v(58.28, -19.8) * mm, "end": v(55.42, -20.98) * mm});
            skLineSegment(sketch, "E20.4.2.10", {"start": v(55.42, -20.98) * mm, "end": v(48.75, -27.66) * mm});
            skArc(sketch, "E20.4.2.11", {"start": v(48.75, -27.66) * mm, "mid": v(47.57, -30.5) * mm, "end": v(48.75, -33.36) * mm});
            skLineSegment(sketch, "E20.4.2.12", {"start": v(48.75, -33.36) * mm, "end": v(55.42, -40.03) * mm});
            skArc(sketch, "E20.4.2.13", {"start": v(55.42, -40.03) * mm, "mid": v(58.28, -41.21) * mm, "end": v(61.13, -40.03) * mm});
            skLineSegment(sketch, "E20.4.2.14", {"start": v(61.13, -40.03) * mm, "end": v(67.8, -33.36) * mm});
            skArc(sketch, "E20.4.2.15", {"start": v(67.8, -33.36) * mm, "mid": v(68.98, -30.5) * mm, "end": v(67.8, -27.66) * mm});
            skLineSegment(sketch, "E20.4.3.0", {"start": v(82.8, -42.66) * mm, "end": v(76.13, -35.98) * mm});
            skArc(sketch, "E20.4.3.1", {"start": v(76.13, -35.98) * mm, "mid": v(73.28, -34.8) * mm, "end": v(70.42, -35.98) * mm});
            skLineSegment(sketch, "E20.4.3.2", {"start": v(70.42, -35.98) * mm, "end": v(63.75, -42.66) * mm});
            skArc(sketch, "E20.4.3.3", {"start": v(63.75, -42.66) * mm, "mid": v(62.57, -45.5) * mm, "end": v(63.75, -48.36) * mm});
            skLineSegment(sketch, "E20.4.3.4", {"start": v(63.75, -48.36) * mm, "end": v(70.42, -55.03) * mm});
            skArc(sketch, "E20.4.3.5", {"start": v(70.42, -55.03) * mm, "mid": v(73.28, -56.21) * mm, "end": v(76.13, -55.03) * mm});
            skLineSegment(sketch, "E20.4.3.6", {"start": v(76.13, -55.03) * mm, "end": v(82.8, -48.36) * mm});
            skArc(sketch, "E20.4.3.7", {"start": v(82.8, -48.36) * mm, "mid": v(83.98, -45.5) * mm, "end": v(82.8, -42.66) * mm});
            skLineSegment(sketch, "E20.4.3.8", {"start": v(67.8, -57.66) * mm, "end": v(61.13, -50.98) * mm});
            skArc(sketch, "E20.4.3.9", {"start": v(61.13, -50.98) * mm, "mid": v(58.28, -49.8) * mm, "end": v(55.42, -50.98) * mm});
            skLineSegment(sketch, "E20.4.3.10", {"start": v(55.42, -50.98) * mm, "end": v(48.75, -57.66) * mm});
            skArc(sketch, "E20.4.3.11", {"start": v(48.75, -57.66) * mm, "mid": v(47.57, -60.5) * mm, "end": v(48.75, -63.36) * mm});
            skLineSegment(sketch, "E20.4.3.12", {"start": v(48.75, -63.36) * mm, "end": v(55.42, -70.03) * mm});
            skArc(sketch, "E20.4.3.13", {"start": v(55.42, -70.03) * mm, "mid": v(58.28, -71.21) * mm, "end": v(61.13, -70.03) * mm});
            skLineSegment(sketch, "E20.4.3.14", {"start": v(61.13, -70.03) * mm, "end": v(67.8, -63.36) * mm});
            skArc(sketch, "E20.4.3.15", {"start": v(67.8, -63.36) * mm, "mid": v(68.98, -60.5) * mm, "end": v(67.8, -57.66) * mm});
            skLineSegment(sketch, "E20.5.0.0", {"start": v(112.8, 47.34) * mm, "end": v(106.13, 54.02) * mm});
            skArc(sketch, "E20.5.0.1", {"start": v(106.13, 54.02) * mm, "mid": v(103.28, 55.2) * mm, "end": v(100.42, 54.02) * mm});
            skLineSegment(sketch, "E20.5.0.2", {"start": v(100.42, 54.02) * mm, "end": v(93.75, 47.34) * mm});
            skArc(sketch, "E20.5.0.3", {"start": v(93.75, 47.34) * mm, "mid": v(92.57, 44.5) * mm, "end": v(93.75, 41.64) * mm});
            skLineSegment(sketch, "E20.5.0.4", {"start": v(93.75, 41.64) * mm, "end": v(100.42, 34.97) * mm});
            skArc(sketch, "E20.5.0.5", {"start": v(100.42, 34.97) * mm, "mid": v(103.28, 33.79) * mm, "end": v(106.13, 34.97) * mm});
            skLineSegment(sketch, "E20.5.0.6", {"start": v(106.13, 34.97) * mm, "end": v(112.8, 41.64) * mm});
            skArc(sketch, "E20.5.0.7", {"start": v(112.8, 41.64) * mm, "mid": v(113.98, 44.5) * mm, "end": v(112.8, 47.34) * mm});
            skLineSegment(sketch, "E20.5.0.8", {"start": v(97.8, 32.34) * mm, "end": v(91.13, 39.02) * mm});
            skArc(sketch, "E20.5.0.9", {"start": v(91.13, 39.02) * mm, "mid": v(88.28, 40.2) * mm, "end": v(85.42, 39.02) * mm});
            skLineSegment(sketch, "E20.5.0.10", {"start": v(85.42, 39.02) * mm, "end": v(78.75, 32.34) * mm});
            skArc(sketch, "E20.5.0.11", {"start": v(78.75, 32.34) * mm, "mid": v(77.57, 29.5) * mm, "end": v(78.75, 26.64) * mm});
            skLineSegment(sketch, "E20.5.0.12", {"start": v(78.75, 26.64) * mm, "end": v(85.42, 19.97) * mm});
            skArc(sketch, "E20.5.0.13", {"start": v(85.42, 19.97) * mm, "mid": v(88.28, 18.79) * mm, "end": v(91.13, 19.97) * mm});
            skLineSegment(sketch, "E20.5.0.14", {"start": v(91.13, 19.97) * mm, "end": v(97.8, 26.64) * mm});
            skArc(sketch, "E20.5.0.15", {"start": v(97.8, 26.64) * mm, "mid": v(98.98, 29.5) * mm, "end": v(97.8, 32.34) * mm});
            skLineSegment(sketch, "E20.5.1.0", {"start": v(112.8, 17.34) * mm, "end": v(106.13, 24.02) * mm});
            skArc(sketch, "E20.5.1.1", {"start": v(106.13, 24.02) * mm, "mid": v(103.28, 25.2) * mm, "end": v(100.42, 24.02) * mm});
            skLineSegment(sketch, "E20.5.1.2", {"start": v(100.42, 24.02) * mm, "end": v(93.75, 17.34) * mm});
            skArc(sketch, "E20.5.1.3", {"start": v(93.75, 17.34) * mm, "mid": v(92.57, 14.5) * mm, "end": v(93.75, 11.64) * mm});
            skLineSegment(sketch, "E20.5.1.4", {"start": v(93.75, 11.64) * mm, "end": v(100.42, 4.97) * mm});
            skArc(sketch, "E20.5.1.5", {"start": v(100.42, 4.97) * mm, "mid": v(103.28, 3.79) * mm, "end": v(106.13, 4.97) * mm});
            skLineSegment(sketch, "E20.5.1.6", {"start": v(106.13, 4.97) * mm, "end": v(112.8, 11.64) * mm});
            skArc(sketch, "E20.5.1.7", {"start": v(112.8, 11.64) * mm, "mid": v(113.98, 14.5) * mm, "end": v(112.8, 17.34) * mm});
            skLineSegment(sketch, "E20.5.1.8", {"start": v(97.8, 2.34) * mm, "end": v(91.13, 9.02) * mm});
            skArc(sketch, "E20.5.1.9", {"start": v(91.13, 9.02) * mm, "mid": v(88.28, 10.2) * mm, "end": v(85.42, 9.02) * mm});
            skLineSegment(sketch, "E20.5.1.10", {"start": v(85.42, 9.02) * mm, "end": v(78.75, 2.34) * mm});
            skArc(sketch, "E20.5.1.11", {"start": v(78.75, 2.34) * mm, "mid": v(77.57, -0.5) * mm, "end": v(78.75, -3.36) * mm});
            skLineSegment(sketch, "E20.5.1.12", {"start": v(78.75, -3.36) * mm, "end": v(85.42, -10.03) * mm});
            skArc(sketch, "E20.5.1.13", {"start": v(85.42, -10.03) * mm, "mid": v(88.28, -11.21) * mm, "end": v(91.13, -10.03) * mm});
            skLineSegment(sketch, "E20.5.1.14", {"start": v(91.13, -10.03) * mm, "end": v(97.8, -3.36) * mm});
            skArc(sketch, "E20.5.1.15", {"start": v(97.8, -3.36) * mm, "mid": v(98.98, -0.5) * mm, "end": v(97.8, 2.34) * mm});
            skLineSegment(sketch, "E20.5.2.0", {"start": v(112.8, -12.66) * mm, "end": v(106.13, -5.98) * mm});
            skArc(sketch, "E20.5.2.1", {"start": v(106.13, -5.98) * mm, "mid": v(103.28, -4.8) * mm, "end": v(100.42, -5.98) * mm});
            skLineSegment(sketch, "E20.5.2.2", {"start": v(100.42, -5.98) * mm, "end": v(93.75, -12.66) * mm});
            skArc(sketch, "E20.5.2.3", {"start": v(93.75, -12.66) * mm, "mid": v(92.57, -15.5) * mm, "end": v(93.75, -18.36) * mm});
            skLineSegment(sketch, "E20.5.2.4", {"start": v(93.75, -18.36) * mm, "end": v(100.42, -25.03) * mm});
            skArc(sketch, "E20.5.2.5", {"start": v(100.42, -25.03) * mm, "mid": v(103.28, -26.21) * mm, "end": v(106.13, -25.03) * mm});
            skLineSegment(sketch, "E20.5.2.6", {"start": v(106.13, -25.03) * mm, "end": v(112.8, -18.36) * mm});
            skArc(sketch, "E20.5.2.7", {"start": v(112.8, -18.36) * mm, "mid": v(113.98, -15.5) * mm, "end": v(112.8, -12.66) * mm});
            skLineSegment(sketch, "E20.5.2.8", {"start": v(97.8, -27.66) * mm, "end": v(91.13, -20.98) * mm});
            skArc(sketch, "E20.5.2.9", {"start": v(91.13, -20.98) * mm, "mid": v(88.28, -19.8) * mm, "end": v(85.42, -20.98) * mm});
            skLineSegment(sketch, "E20.5.2.10", {"start": v(85.42, -20.98) * mm, "end": v(78.75, -27.66) * mm});
            skArc(sketch, "E20.5.2.11", {"start": v(78.75, -27.66) * mm, "mid": v(77.57, -30.5) * mm, "end": v(78.75, -33.36) * mm});
            skLineSegment(sketch, "E20.5.2.12", {"start": v(78.75, -33.36) * mm, "end": v(85.42, -40.03) * mm});
            skArc(sketch, "E20.5.2.13", {"start": v(85.42, -40.03) * mm, "mid": v(88.28, -41.21) * mm, "end": v(91.13, -40.03) * mm});
            skLineSegment(sketch, "E20.5.2.14", {"start": v(91.13, -40.03) * mm, "end": v(97.8, -33.36) * mm});
            skArc(sketch, "E20.5.2.15", {"start": v(97.8, -33.36) * mm, "mid": v(98.98, -30.5) * mm, "end": v(97.8, -27.66) * mm});
            skLineSegment(sketch, "E20.5.3.0", {"start": v(112.8, -42.66) * mm, "end": v(106.13, -35.98) * mm});
            skArc(sketch, "E20.5.3.1", {"start": v(106.13, -35.98) * mm, "mid": v(103.28, -34.8) * mm, "end": v(100.42, -35.98) * mm});
            skLineSegment(sketch, "E20.5.3.2", {"start": v(100.42, -35.98) * mm, "end": v(93.75, -42.66) * mm});
            skArc(sketch, "E20.5.3.3", {"start": v(93.75, -42.66) * mm, "mid": v(92.57, -45.5) * mm, "end": v(93.75, -48.36) * mm});
            skLineSegment(sketch, "E20.5.3.4", {"start": v(93.75, -48.36) * mm, "end": v(100.42, -55.03) * mm});
            skArc(sketch, "E20.5.3.5", {"start": v(100.42, -55.03) * mm, "mid": v(103.28, -56.21) * mm, "end": v(106.13, -55.03) * mm});
            skLineSegment(sketch, "E20.5.3.6", {"start": v(106.13, -55.03) * mm, "end": v(112.8, -48.36) * mm});
            skArc(sketch, "E20.5.3.7", {"start": v(112.8, -48.36) * mm, "mid": v(113.98, -45.5) * mm, "end": v(112.8, -42.66) * mm});
            skLineSegment(sketch, "E20.5.3.8", {"start": v(97.8, -57.66) * mm, "end": v(91.13, -50.98) * mm});
            skArc(sketch, "E20.5.3.9", {"start": v(91.13, -50.98) * mm, "mid": v(88.28, -49.8) * mm, "end": v(85.42, -50.98) * mm});
            skLineSegment(sketch, "E20.5.3.10", {"start": v(85.42, -50.98) * mm, "end": v(78.75, -57.66) * mm});
            skArc(sketch, "E20.5.3.11", {"start": v(78.75, -57.66) * mm, "mid": v(77.57, -60.5) * mm, "end": v(78.75, -63.36) * mm});
            skLineSegment(sketch, "E20.5.3.12", {"start": v(78.75, -63.36) * mm, "end": v(85.42, -70.03) * mm});
            skArc(sketch, "E20.5.3.13", {"start": v(85.42, -70.03) * mm, "mid": v(88.28, -71.21) * mm, "end": v(91.13, -70.03) * mm});
            skLineSegment(sketch, "E20.5.3.14", {"start": v(91.13, -70.03) * mm, "end": v(97.8, -63.36) * mm});
            skArc(sketch, "E20.5.3.15", {"start": v(97.8, -63.36) * mm, "mid": v(98.98, -60.5) * mm, "end": v(97.8, -57.66) * mm});
            skLineSegment(sketch, "E20.6.0.0", {"start": v(142.8, 47.34) * mm, "end": v(136.13, 54.02) * mm});
            skArc(sketch, "E20.6.0.1", {"start": v(136.13, 54.02) * mm, "mid": v(133.28, 55.2) * mm, "end": v(130.42, 54.02) * mm});
            skLineSegment(sketch, "E20.6.0.2", {"start": v(130.42, 54.02) * mm, "end": v(123.75, 47.34) * mm});
            skArc(sketch, "E20.6.0.3", {"start": v(123.75, 47.34) * mm, "mid": v(122.57, 44.5) * mm, "end": v(123.75, 41.64) * mm});
            skLineSegment(sketch, "E20.6.0.4", {"start": v(123.75, 41.64) * mm, "end": v(130.42, 34.97) * mm});
            skArc(sketch, "E20.6.0.5", {"start": v(130.42, 34.97) * mm, "mid": v(133.28, 33.79) * mm, "end": v(136.13, 34.97) * mm});
            skLineSegment(sketch, "E20.6.0.6", {"start": v(136.13, 34.97) * mm, "end": v(142.8, 41.64) * mm});
            skArc(sketch, "E20.6.0.7", {"start": v(142.8, 41.64) * mm, "mid": v(143.98, 44.5) * mm, "end": v(142.8, 47.34) * mm});
            skLineSegment(sketch, "E20.6.0.8", {"start": v(127.8, 32.34) * mm, "end": v(121.13, 39.02) * mm});
            skArc(sketch, "E20.6.0.9", {"start": v(121.13, 39.02) * mm, "mid": v(118.28, 40.2) * mm, "end": v(115.42, 39.02) * mm});
            skLineSegment(sketch, "E20.6.0.10", {"start": v(115.42, 39.02) * mm, "end": v(108.75, 32.34) * mm});
            skArc(sketch, "E20.6.0.11", {"start": v(108.75, 32.34) * mm, "mid": v(107.57, 29.5) * mm, "end": v(108.75, 26.64) * mm});
            skLineSegment(sketch, "E20.6.0.12", {"start": v(108.75, 26.64) * mm, "end": v(115.42, 19.97) * mm});
            skArc(sketch, "E20.6.0.13", {"start": v(115.42, 19.97) * mm, "mid": v(118.28, 18.79) * mm, "end": v(121.13, 19.97) * mm});
            skLineSegment(sketch, "E20.6.0.14", {"start": v(121.13, 19.97) * mm, "end": v(127.8, 26.64) * mm});
            skArc(sketch, "E20.6.0.15", {"start": v(127.8, 26.64) * mm, "mid": v(128.98, 29.5) * mm, "end": v(127.8, 32.34) * mm});
            skLineSegment(sketch, "E20.6.1.0", {"start": v(142.8, 17.34) * mm, "end": v(136.13, 24.02) * mm});
            skArc(sketch, "E20.6.1.1", {"start": v(136.13, 24.02) * mm, "mid": v(133.28, 25.2) * mm, "end": v(130.42, 24.02) * mm});
            skLineSegment(sketch, "E20.6.1.2", {"start": v(130.42, 24.02) * mm, "end": v(123.75, 17.34) * mm});
            skArc(sketch, "E20.6.1.3", {"start": v(123.75, 17.34) * mm, "mid": v(122.57, 14.5) * mm, "end": v(123.75, 11.64) * mm});
            skLineSegment(sketch, "E20.6.1.4", {"start": v(123.75, 11.64) * mm, "end": v(130.42, 4.97) * mm});
            skArc(sketch, "E20.6.1.5", {"start": v(130.42, 4.97) * mm, "mid": v(133.28, 3.79) * mm, "end": v(136.13, 4.97) * mm});
            skLineSegment(sketch, "E20.6.1.6", {"start": v(136.13, 4.97) * mm, "end": v(142.8, 11.64) * mm});
            skArc(sketch, "E20.6.1.7", {"start": v(142.8, 11.64) * mm, "mid": v(143.98, 14.5) * mm, "end": v(142.8, 17.34) * mm});
            skLineSegment(sketch, "E20.6.1.8", {"start": v(127.8, 2.34) * mm, "end": v(121.13, 9.02) * mm});
            skArc(sketch, "E20.6.1.9", {"start": v(121.13, 9.02) * mm, "mid": v(118.28, 10.2) * mm, "end": v(115.42, 9.02) * mm});
            skLineSegment(sketch, "E20.6.1.10", {"start": v(115.42, 9.02) * mm, "end": v(108.75, 2.34) * mm});
            skArc(sketch, "E20.6.1.11", {"start": v(108.75, 2.34) * mm, "mid": v(107.57, -0.5) * mm, "end": v(108.75, -3.36) * mm});
            skLineSegment(sketch, "E20.6.1.12", {"start": v(108.75, -3.36) * mm, "end": v(115.42, -10.03) * mm});
            skArc(sketch, "E20.6.1.13", {"start": v(115.42, -10.03) * mm, "mid": v(118.28, -11.21) * mm, "end": v(121.13, -10.03) * mm});
            skLineSegment(sketch, "E20.6.1.14", {"start": v(121.13, -10.03) * mm, "end": v(127.8, -3.36) * mm});
            skArc(sketch, "E20.6.1.15", {"start": v(127.8, -3.36) * mm, "mid": v(128.98, -0.5) * mm, "end": v(127.8, 2.34) * mm});
            skLineSegment(sketch, "E20.6.2.0", {"start": v(142.8, -12.66) * mm, "end": v(136.13, -5.98) * mm});
            skArc(sketch, "E20.6.2.1", {"start": v(136.13, -5.98) * mm, "mid": v(133.28, -4.8) * mm, "end": v(130.42, -5.98) * mm});
            skLineSegment(sketch, "E20.6.2.2", {"start": v(130.42, -5.98) * mm, "end": v(123.75, -12.66) * mm});
            skArc(sketch, "E20.6.2.3", {"start": v(123.75, -12.66) * mm, "mid": v(122.57, -15.5) * mm, "end": v(123.75, -18.36) * mm});
            skLineSegment(sketch, "E20.6.2.4", {"start": v(123.75, -18.36) * mm, "end": v(130.42, -25.03) * mm});
            skArc(sketch, "E20.6.2.5", {"start": v(130.42, -25.03) * mm, "mid": v(133.28, -26.21) * mm, "end": v(136.13, -25.03) * mm});
            skLineSegment(sketch, "E20.6.2.6", {"start": v(136.13, -25.03) * mm, "end": v(142.8, -18.36) * mm});
            skArc(sketch, "E20.6.2.7", {"start": v(142.8, -18.36) * mm, "mid": v(143.98, -15.5) * mm, "end": v(142.8, -12.66) * mm});
            skLineSegment(sketch, "E20.6.2.8", {"start": v(127.8, -27.66) * mm, "end": v(121.13, -20.98) * mm});
            skArc(sketch, "E20.6.2.9", {"start": v(121.13, -20.98) * mm, "mid": v(118.28, -19.8) * mm, "end": v(115.42, -20.98) * mm});
            skLineSegment(sketch, "E20.6.2.10", {"start": v(115.42, -20.98) * mm, "end": v(108.75, -27.66) * mm});
            skArc(sketch, "E20.6.2.11", {"start": v(108.75, -27.66) * mm, "mid": v(107.57, -30.5) * mm, "end": v(108.75, -33.36) * mm});
            skLineSegment(sketch, "E20.6.2.12", {"start": v(108.75, -33.36) * mm, "end": v(115.42, -40.03) * mm});
            skArc(sketch, "E20.6.2.13", {"start": v(115.42, -40.03) * mm, "mid": v(118.28, -41.21) * mm, "end": v(121.13, -40.03) * mm});
            skLineSegment(sketch, "E20.6.2.14", {"start": v(121.13, -40.03) * mm, "end": v(127.8, -33.36) * mm});
            skArc(sketch, "E20.6.2.15", {"start": v(127.8, -33.36) * mm, "mid": v(128.98, -30.5) * mm, "end": v(127.8, -27.66) * mm});
            skLineSegment(sketch, "E20.6.3.0", {"start": v(142.8, -42.66) * mm, "end": v(136.13, -35.98) * mm});
            skArc(sketch, "E20.6.3.1", {"start": v(136.13, -35.98) * mm, "mid": v(133.28, -34.8) * mm, "end": v(130.42, -35.98) * mm});
            skLineSegment(sketch, "E20.6.3.2", {"start": v(130.42, -35.98) * mm, "end": v(123.75, -42.66) * mm});
            skArc(sketch, "E20.6.3.3", {"start": v(123.75, -42.66) * mm, "mid": v(122.57, -45.5) * mm, "end": v(123.75, -48.36) * mm});
            skLineSegment(sketch, "E20.6.3.4", {"start": v(123.75, -48.36) * mm, "end": v(130.42, -55.03) * mm});
            skArc(sketch, "E20.6.3.5", {"start": v(130.42, -55.03) * mm, "mid": v(133.28, -56.21) * mm, "end": v(136.13, -55.03) * mm});
            skLineSegment(sketch, "E20.6.3.6", {"start": v(136.13, -55.03) * mm, "end": v(142.8, -48.36) * mm});
            skArc(sketch, "E20.6.3.7", {"start": v(142.8, -48.36) * mm, "mid": v(143.98, -45.5) * mm, "end": v(142.8, -42.66) * mm});
            skLineSegment(sketch, "E20.6.3.8", {"start": v(127.8, -57.66) * mm, "end": v(121.13, -50.98) * mm});
            skArc(sketch, "E20.6.3.9", {"start": v(121.13, -50.98) * mm, "mid": v(118.28, -49.8) * mm, "end": v(115.42, -50.98) * mm});
            skLineSegment(sketch, "E20.6.3.10", {"start": v(115.42, -50.98) * mm, "end": v(108.75, -57.66) * mm});
            skArc(sketch, "E20.6.3.11", {"start": v(108.75, -57.66) * mm, "mid": v(107.57, -60.5) * mm, "end": v(108.75, -63.36) * mm});
            skLineSegment(sketch, "E20.6.3.12", {"start": v(108.75, -63.36) * mm, "end": v(115.42, -70.03) * mm});
            skArc(sketch, "E20.6.3.13", {"start": v(115.42, -70.03) * mm, "mid": v(118.28, -71.21) * mm, "end": v(121.13, -70.03) * mm});
            skLineSegment(sketch, "E20.6.3.14", {"start": v(121.13, -70.03) * mm, "end": v(127.8, -63.36) * mm});
            skArc(sketch, "E20.6.3.15", {"start": v(127.8, -63.36) * mm, "mid": v(128.98, -60.5) * mm, "end": v(127.8, -57.66) * mm});
            skLineSegment(sketch, "E20.direction1", {"start": v(-37.2, 47.34) * mm, "end": v(-7.2, 47.34) * mm, "construction": true});
            skLineSegment(sketch, "E20.direction2", {"start": v(-37.2, 47.34) * mm, "end": v(-37.2, 17.34) * mm, "construction": true});
            skLineSegment(sketch, "E21", {"start": v(-60.46, 61.03) * mm, "end": v(-60.46, -13.97) * mm});
            skLineSegment(sketch, "E22", {"start": v(-60.46, -13.97) * mm, "end": v(27.06, -13.97) * mm});
            skLineSegment(sketch, "E23", {"start": v(27.06, -13.97) * mm, "end": v(27.06, -56.47) * mm});
            skLineSegment(sketch, "E24", {"start": v(27.06, -56.47) * mm, "end": v(114.54, -56.47) * mm});
            skLineSegment(sketch, "E25", {"start": v(114.54, -56.47) * mm, "end": v(114.54, 61.03) * mm});
            skLineSegment(sketch, "E26", {"start": v(114.54, 61.03) * mm, "end": v(-60.46, 61.03) * mm});
            skLineSegment(sketch, "E27.1.0.8", {"start": v(-52.54, 62.34) * mm, "end": v(-59.04, 68.85) * mm});
            skArc(sketch, "E27.1.0.9", {"start": v(-59.04, 68.85) * mm, "mid": v(-61.9, 70.08) * mm, "end": v(-64.74, 68.85) * mm});
            skLineSegment(sketch, "E27.1.0.10", {"start": v(-64.74, 68.85) * mm, "end": v(-71.25, 62.34) * mm});
            skArc(sketch, "E27.1.0.11", {"start": v(-71.25, 62.34) * mm, "mid": v(-72.43, 59.5) * mm, "end": v(-71.25, 56.64) * mm});
            skLineSegment(sketch, "E27.1.0.12", {"start": v(-71.25, 56.64) * mm, "end": v(-64.74, 50.14) * mm});
            skArc(sketch, "E27.1.0.13", {"start": v(-64.74, 50.14) * mm, "mid": v(-61.9, 48.96) * mm, "end": v(-59.04, 50.14) * mm});
            skLineSegment(sketch, "E27.1.0.14", {"start": v(-59.04, 50.14) * mm, "end": v(-52.54, 56.64) * mm});
            skArc(sketch, "E27.1.0.15", {"start": v(-52.54, 56.64) * mm, "mid": v(-51.36, 59.5) * mm, "end": v(-52.54, 62.34) * mm});
            skLineSegment(sketch, "E28.1.0.0", {"start": v(-34.74, 68.85) * mm, "end": v(-41.25, 62.34) * mm});
            skArc(sketch, "E28.1.0.1", {"start": v(-29.04, 68.85) * mm, "mid": v(-31.9, 70.08) * mm, "end": v(-34.74, 68.85) * mm});
            skLineSegment(sketch, "E28.1.0.2", {"start": v(-22.54, 62.34) * mm, "end": v(-29.04, 68.85) * mm});
            skArc(sketch, "E28.1.0.3", {"start": v(-22.54, 56.64) * mm, "mid": v(-21.36, 59.5) * mm, "end": v(-22.54, 62.34) * mm});
            skLineSegment(sketch, "E28.1.0.4", {"start": v(-29.04, 50.14) * mm, "end": v(-22.54, 56.64) * mm});
            skArc(sketch, "E28.1.0.5", {"start": v(-34.74, 50.14) * mm, "mid": v(-31.9, 48.96) * mm, "end": v(-29.04, 50.14) * mm});
            skLineSegment(sketch, "E28.1.0.6", {"start": v(-41.25, 56.64) * mm, "end": v(-34.74, 50.14) * mm});
            skArc(sketch, "E28.1.0.7", {"start": v(-41.25, 62.34) * mm, "mid": v(-42.43, 59.5) * mm, "end": v(-41.25, 56.64) * mm});
            skLineSegment(sketch, "E28.2.0.0", {"start": v(-4.74, 68.85) * mm, "end": v(-11.25, 62.34) * mm});
            skArc(sketch, "E28.2.0.1", {"start": v(0.96, 68.85) * mm, "mid": v(-1.9, 70.08) * mm, "end": v(-4.74, 68.85) * mm});
            skLineSegment(sketch, "E28.2.0.2", {"start": v(7.46, 62.34) * mm, "end": v(0.96, 68.85) * mm});
            skArc(sketch, "E28.2.0.3", {"start": v(7.46, 56.64) * mm, "mid": v(8.64, 59.5) * mm, "end": v(7.46, 62.34) * mm});
            skLineSegment(sketch, "E28.2.0.4", {"start": v(0.96, 50.14) * mm, "end": v(7.46, 56.64) * mm});
            skArc(sketch, "E28.2.0.5", {"start": v(-4.74, 50.14) * mm, "mid": v(-1.9, 48.96) * mm, "end": v(0.96, 50.14) * mm});
            skLineSegment(sketch, "E28.2.0.6", {"start": v(-11.25, 56.64) * mm, "end": v(-4.74, 50.14) * mm});
            skArc(sketch, "E28.2.0.7", {"start": v(-11.25, 62.34) * mm, "mid": v(-12.43, 59.5) * mm, "end": v(-11.25, 56.64) * mm});
            skLineSegment(sketch, "E28.3.0.0", {"start": v(25.26, 68.85) * mm, "end": v(18.75, 62.34) * mm});
            skArc(sketch, "E28.3.0.1", {"start": v(30.96, 68.85) * mm, "mid": v(28.1, 70.08) * mm, "end": v(25.26, 68.85) * mm});
            skLineSegment(sketch, "E28.3.0.2", {"start": v(37.46, 62.34) * mm, "end": v(30.96, 68.85) * mm});
            skArc(sketch, "E28.3.0.3", {"start": v(37.46, 56.64) * mm, "mid": v(38.64, 59.5) * mm, "end": v(37.46, 62.34) * mm});
            skLineSegment(sketch, "E28.3.0.4", {"start": v(30.96, 50.14) * mm, "end": v(37.46, 56.64) * mm});
            skArc(sketch, "E28.3.0.5", {"start": v(25.26, 50.14) * mm, "mid": v(28.1, 48.96) * mm, "end": v(30.96, 50.14) * mm});
            skLineSegment(sketch, "E28.3.0.6", {"start": v(18.75, 56.64) * mm, "end": v(25.26, 50.14) * mm});
            skArc(sketch, "E28.3.0.7", {"start": v(18.75, 62.34) * mm, "mid": v(17.57, 59.5) * mm, "end": v(18.75, 56.64) * mm});
            skLineSegment(sketch, "E28.4.0.0", {"start": v(55.26, 68.85) * mm, "end": v(48.75, 62.34) * mm});
            skArc(sketch, "E28.4.0.1", {"start": v(60.96, 68.85) * mm, "mid": v(58.1, 70.08) * mm, "end": v(55.26, 68.85) * mm});
            skLineSegment(sketch, "E28.4.0.2", {"start": v(67.46, 62.34) * mm, "end": v(60.96, 68.85) * mm});
            skArc(sketch, "E28.4.0.3", {"start": v(67.46, 56.64) * mm, "mid": v(68.64, 59.5) * mm, "end": v(67.46, 62.34) * mm});
            skLineSegment(sketch, "E28.4.0.4", {"start": v(60.96, 50.14) * mm, "end": v(67.46, 56.64) * mm});
            skArc(sketch, "E28.4.0.5", {"start": v(55.26, 50.14) * mm, "mid": v(58.1, 48.96) * mm, "end": v(60.96, 50.14) * mm});
            skLineSegment(sketch, "E28.4.0.6", {"start": v(48.75, 56.64) * mm, "end": v(55.26, 50.14) * mm});
            skArc(sketch, "E28.4.0.7", {"start": v(48.75, 62.34) * mm, "mid": v(47.57, 59.5) * mm, "end": v(48.75, 56.64) * mm});
            skLineSegment(sketch, "E28.5.0.0", {"start": v(85.26, 68.85) * mm, "end": v(78.75, 62.34) * mm});
            skArc(sketch, "E28.5.0.1", {"start": v(90.96, 68.85) * mm, "mid": v(88.1, 70.08) * mm, "end": v(85.26, 68.85) * mm});
            skLineSegment(sketch, "E28.5.0.2", {"start": v(97.46, 62.34) * mm, "end": v(90.96, 68.85) * mm});
            skArc(sketch, "E28.5.0.3", {"start": v(97.46, 56.64) * mm, "mid": v(98.64, 59.5) * mm, "end": v(97.46, 62.34) * mm});
            skLineSegment(sketch, "E28.5.0.4", {"start": v(90.96, 50.14) * mm, "end": v(97.46, 56.64) * mm});
            skArc(sketch, "E28.5.0.5", {"start": v(85.26, 50.14) * mm, "mid": v(88.1, 48.96) * mm, "end": v(90.96, 50.14) * mm});
            skLineSegment(sketch, "E28.5.0.6", {"start": v(78.75, 56.64) * mm, "end": v(85.26, 50.14) * mm});
            skArc(sketch, "E28.5.0.7", {"start": v(78.75, 62.34) * mm, "mid": v(77.57, 59.5) * mm, "end": v(78.75, 56.64) * mm});
            skLineSegment(sketch, "E28.6.0.0", {"start": v(115.26, 68.85) * mm, "end": v(108.75, 62.34) * mm});
            skArc(sketch, "E28.6.0.1", {"start": v(120.96, 68.85) * mm, "mid": v(118.1, 70.08) * mm, "end": v(115.26, 68.85) * mm});
            skLineSegment(sketch, "E28.6.0.2", {"start": v(127.46, 62.34) * mm, "end": v(120.96, 68.85) * mm});
            skArc(sketch, "E28.6.0.3", {"start": v(127.46, 56.64) * mm, "mid": v(128.64, 59.5) * mm, "end": v(127.46, 62.34) * mm});
            skLineSegment(sketch, "E28.6.0.4", {"start": v(120.96, 50.14) * mm, "end": v(127.46, 56.64) * mm});
            skArc(sketch, "E28.6.0.5", {"start": v(115.26, 50.14) * mm, "mid": v(118.1, 48.96) * mm, "end": v(120.96, 50.14) * mm});
            skLineSegment(sketch, "E28.6.0.6", {"start": v(108.75, 56.64) * mm, "end": v(115.26, 50.14) * mm});
            skArc(sketch, "E28.6.0.7", {"start": v(108.75, 62.34) * mm, "mid": v(107.57, 59.5) * mm, "end": v(108.75, 56.64) * mm});
            skLineSegment(sketch, "E28.direction1", {"start": v(-64.74, 50.14) * mm, "end": v(-34.74, 50.14) * mm, "construction": true});
            skLineSegment(sketch, "E29", {"start": v(-60.46, 58.53) * mm, "end": v(114.54, 58.53) * mm});
            skSolve(sketch);
        }
        {
            var Q0;
            Q0=makeQuery(id+"F6.imprint","IMPRINT",FACE,{"disambiguationData":[TD([[makeQuery(id+"F6.imprint","IMPRINT",EDGE,{"derivedFrom":sQuery(id+"F6.wireOp",EDGE,"E4")}),1.0]])]});
            var Q1;
            {var subQ4=sQuery(id+"F6.wireOp",EDGE,"E14");Q1=makeQuery(id+"F6.imprint","IMPRINT",FACE,{"disambiguationData":[TD([[makeQuery(id+"F6.imprint","IMPRINT",EDGE,{"derivedFrom":subQ4}),1.0]])]});}
            var Q2;
            {var subQ5=sQuery(id+"F6.wireOp",EDGE,"E20.0.1.8");Q2=makeQuery(id+"F6.imprint","IMPRINT",FACE,{"disambiguationData":[TD([[makeQuery(id+"F6.imprint","IMPRINT",EDGE,{"derivedFrom":subQ5}),1.0]])]});}
            var Q3;
            Q3=makeQuery(id+"F6.imprint","IMPRINT",FACE,{"disambiguationData":[TD([[makeQuery(id+"F6.imprint","IMPRINT",EDGE,{"derivedFrom":sQuery(id+"F6.wireOp",EDGE,"E20.0.1.0")}),1.0]])]});
            var Q4;
            Q4=makeQuery(id+"F6.imprint","IMPRINT",FACE,{"disambiguationData":[TD([[makeQuery(id+"F6.imprint","IMPRINT",EDGE,{"derivedFrom":sQuery(id+"F6.wireOp",EDGE,"E20.0.2.0")}),1.0]])]});
            var Q5;
            Q5=makeQuery(id+"F6.imprint","IMPRINT",FACE,{"disambiguationData":[TD([[makeQuery(id+"F6.imprint","IMPRINT",EDGE,{"derivedFrom":sQuery(id+"F6.wireOp",EDGE,"E20.1.2.0")}),1.0]])]});
            var Q6;
            Q6=makeQuery(id+"F6.imprint","IMPRINT",FACE,{"disambiguationData":[TD([[makeQuery(id+"F6.imprint","IMPRINT",EDGE,{"derivedFrom":sQuery(id+"F6.wireOp",EDGE,"E20.1.1.8")}),1.0]])]});
            var Q7;
            Q7=makeQuery(id+"F6.imprint","IMPRINT",FACE,{"disambiguationData":[TD([[makeQuery(id+"F6.imprint","IMPRINT",EDGE,{"derivedFrom":sQuery(id+"F6.wireOp",EDGE,"E20.1.1.0")}),1.0]])]});
            var Q8;
            Q8=makeQuery(id+"F6.imprint","IMPRINT",FACE,{"disambiguationData":[TD([[makeQuery(id+"F6.imprint","IMPRINT",EDGE,{"derivedFrom":sQuery(id+"F6.wireOp",EDGE,"E20.1.0.8")}),1.0]])]});
            var Q9;
            Q9=makeQuery(id+"F6.imprint","IMPRINT",FACE,{"disambiguationData":[TD([[makeQuery(id+"F6.imprint","IMPRINT",EDGE,{"derivedFrom":sQuery(id+"F6.wireOp",EDGE,"E20.1.0.0")}),1.0]])]});
            var Q10;
            Q10=makeQuery(id+"F6.imprint","IMPRINT",FACE,{"disambiguationData":[TD([[makeQuery(id+"F6.imprint","IMPRINT",EDGE,{"derivedFrom":sQuery(id+"F6.wireOp",EDGE,"E20.2.0.8")}),1.0]])]});
            var Q11;
            Q11=makeQuery(id+"F6.imprint","IMPRINT",FACE,{"disambiguationData":[TD([[makeQuery(id+"F6.imprint","IMPRINT",EDGE,{"derivedFrom":sQuery(id+"F6.wireOp",EDGE,"E20.2.0.0")}),1.0]])]});
            var Q12;
            Q12=makeQuery(id+"F6.imprint","IMPRINT",FACE,{"disambiguationData":[TD([[makeQuery(id+"F6.imprint","IMPRINT",EDGE,{"derivedFrom":sQuery(id+"F6.wireOp",EDGE,"E20.3.0.8")}),1.0]])]});
            var Q13;
            Q13=makeQuery(id+"F6.imprint","IMPRINT",FACE,{"disambiguationData":[TD([[makeQuery(id+"F6.imprint","IMPRINT",EDGE,{"derivedFrom":sQuery(id+"F6.wireOp",EDGE,"E20.2.1.0")}),1.0]])]});
            var Q14;
            Q14=makeQuery(id+"F6.imprint","IMPRINT",FACE,{"disambiguationData":[TD([[makeQuery(id+"F6.imprint","IMPRINT",EDGE,{"derivedFrom":sQuery(id+"F6.wireOp",EDGE,"E20.2.1.8")}),1.0]])]});
            var Q15;
            Q15=makeQuery(id+"F6.imprint","IMPRINT",FACE,{"disambiguationData":[TD([[makeQuery(id+"F6.imprint","IMPRINT",EDGE,{"derivedFrom":sQuery(id+"F6.wireOp",EDGE,"E20.2.2.0")}),1.0]])]});
            var Q16;
            Q16=makeQuery(id+"F6.imprint","IMPRINT",FACE,{"disambiguationData":[TD([[makeQuery(id+"F6.imprint","IMPRINT",EDGE,{"derivedFrom":sQuery(id+"F6.wireOp",EDGE,"E20.3.2.8")}),1.0]])]});
            var Q17;
            Q17=makeQuery(id+"F6.imprint","IMPRINT",FACE,{"disambiguationData":[TD([[makeQuery(id+"F6.imprint","IMPRINT",EDGE,{"derivedFrom":sQuery(id+"F6.wireOp",EDGE,"E20.3.2.0")}),1.0]])]});
            var Q18;
            Q18=makeQuery(id+"F6.imprint","IMPRINT",FACE,{"disambiguationData":[TD([[makeQuery(id+"F6.imprint","IMPRINT",EDGE,{"derivedFrom":sQuery(id+"F6.wireOp",EDGE,"E20.3.3.0")}),1.0]])]});
            var Q19;
            {var subQ0=sQuery(id+"F6.wireOp",EDGE,"E20.3.3.9");var subQ1=sQuery(id+"F6.wireOp",EDGE,"E20.3.3.8");var subQ2=makeQuery(id+"F6.imprint","INTERSECT",VERTEX,{"derivedFrom":[subQ1,subQ0]});Q19=makeQuery(id+"F6.imprint","IMPRINT",FACE,{"disambiguationData":[TD([[makeQuery(id+"F6.imprint","IMPRINT",EDGE,{"disambiguationData":[TD([[subQ2,1.0]])],"derivedFrom":subQ1}),1.0]])]});}
            var Q20;
            {var subQ0=sQuery(id+"F6.wireOp",EDGE,"E20.4.3.9");Q20=makeQuery(id+"F6.imprint","IMPRINT",FACE,{"disambiguationData":[TD([[makeQuery(id+"F6.imprint","IMPRINT",EDGE,{"derivedFrom":subQ0}),1.0]])]});}
            var Q21;
            Q21=makeQuery(id+"F6.imprint","IMPRINT",FACE,{"disambiguationData":[TD([[makeQuery(id+"F6.imprint","IMPRINT",EDGE,{"derivedFrom":sQuery(id+"F6.wireOp",EDGE,"E20.4.3.0")}),1.0]])]});
            var Q22;
            {var subQ0=sQuery(id+"F6.wireOp",EDGE,"E20.5.3.9");Q22=makeQuery(id+"F6.imprint","IMPRINT",FACE,{"disambiguationData":[TD([[makeQuery(id+"F6.imprint","IMPRINT",EDGE,{"derivedFrom":subQ0}),1.0]])]});}
            var Q23;
            Q23=makeQuery(id+"F6.imprint","IMPRINT",FACE,{"disambiguationData":[TD([[makeQuery(id+"F6.imprint","IMPRINT",EDGE,{"derivedFrom":sQuery(id+"F6.wireOp",EDGE,"E20.5.3.0")}),1.0]])]});
            var Q24;
            {var subQ0=sQuery(id+"F6.wireOp",EDGE,"E20.6.2.11");Q24=makeQuery(id+"F6.imprint","IMPRINT",FACE,{"disambiguationData":[TD([[makeQuery(id+"F6.imprint","IMPRINT",EDGE,{"derivedFrom":subQ0}),1.0]])]});}
            var Q25;
            Q25=makeQuery(id+"F6.imprint","IMPRINT",FACE,{"disambiguationData":[TD([[makeQuery(id+"F6.imprint","IMPRINT",EDGE,{"derivedFrom":sQuery(id+"F6.wireOp",EDGE,"E20.5.2.0")}),1.0]])]});
            var Q26;
            Q26=makeQuery(id+"F6.imprint","IMPRINT",FACE,{"disambiguationData":[TD([[makeQuery(id+"F6.imprint","IMPRINT",EDGE,{"derivedFrom":sQuery(id+"F6.wireOp",EDGE,"E20.5.2.8")}),1.0]])]});
            var Q27;
            Q27=makeQuery(id+"F6.imprint","IMPRINT",FACE,{"disambiguationData":[TD([[makeQuery(id+"F6.imprint","IMPRINT",EDGE,{"derivedFrom":sQuery(id+"F6.wireOp",EDGE,"E20.4.2.8")}),1.0]])]});
            var Q28;
            Q28=makeQuery(id+"F6.imprint","IMPRINT",FACE,{"disambiguationData":[TD([[makeQuery(id+"F6.imprint","IMPRINT",EDGE,{"derivedFrom":sQuery(id+"F6.wireOp",EDGE,"E20.3.1.8")}),1.0]])]});
            var Q29;
            Q29=makeQuery(id+"F6.imprint","IMPRINT",FACE,{"disambiguationData":[TD([[makeQuery(id+"F6.imprint","IMPRINT",EDGE,{"derivedFrom":sQuery(id+"F6.wireOp",EDGE,"E20.4.1.8")}),1.0]])]});
            var Q30;
            Q30=makeQuery(id+"F6.imprint","IMPRINT",FACE,{"disambiguationData":[TD([[makeQuery(id+"F6.imprint","IMPRINT",EDGE,{"derivedFrom":sQuery(id+"F6.wireOp",EDGE,"E20.3.1.0")}),1.0]])]});
            var Q31;
            Q31=makeQuery(id+"F6.imprint","IMPRINT",FACE,{"disambiguationData":[TD([[makeQuery(id+"F6.imprint","IMPRINT",EDGE,{"derivedFrom":sQuery(id+"F6.wireOp",EDGE,"E20.3.0.0")}),1.0]])]});
            var Q32;
            Q32=makeQuery(id+"F6.imprint","IMPRINT",FACE,{"disambiguationData":[TD([[makeQuery(id+"F6.imprint","IMPRINT",EDGE,{"derivedFrom":sQuery(id+"F6.wireOp",EDGE,"E20.4.0.8")}),1.0]])]});
            var Q33;
            Q33=makeQuery(id+"F6.imprint","IMPRINT",FACE,{"disambiguationData":[TD([[makeQuery(id+"F6.imprint","IMPRINT",EDGE,{"derivedFrom":sQuery(id+"F6.wireOp",EDGE,"E20.4.0.0")}),1.0]])]});
            var Q34;
            Q34=makeQuery(id+"F6.imprint","IMPRINT",FACE,{"disambiguationData":[TD([[makeQuery(id+"F6.imprint","IMPRINT",EDGE,{"derivedFrom":sQuery(id+"F6.wireOp",EDGE,"E20.4.1.0")}),1.0]])]});
            var Q35;
            Q35=makeQuery(id+"F6.imprint","IMPRINT",FACE,{"disambiguationData":[TD([[makeQuery(id+"F6.imprint","IMPRINT",EDGE,{"derivedFrom":sQuery(id+"F6.wireOp",EDGE,"E20.5.0.8")}),1.0]])]});
            var Q36;
            Q36=makeQuery(id+"F6.imprint","IMPRINT",FACE,{"disambiguationData":[TD([[makeQuery(id+"F6.imprint","IMPRINT",EDGE,{"derivedFrom":sQuery(id+"F6.wireOp",EDGE,"E20.5.0.0")}),1.0]])]});
            var Q37;
            Q37=makeQuery(id+"F6.imprint","IMPRINT",FACE,{"disambiguationData":[TD([[makeQuery(id+"F6.imprint","IMPRINT",EDGE,{"derivedFrom":sQuery(id+"F6.wireOp",EDGE,"E20.5.1.0")}),1.0]])]});
            var Q38;
            {var subQ0=sQuery(id+"F6.wireOp",EDGE,"E20.6.0.11");Q38=makeQuery(id+"F6.imprint","IMPRINT",FACE,{"disambiguationData":[TD([[makeQuery(id+"F6.imprint","IMPRINT",EDGE,{"derivedFrom":subQ0}),1.0]])]});}
            var Q39;
            Q39=makeQuery(id+"F6.imprint","IMPRINT",FACE,{"disambiguationData":[TD([[makeQuery(id+"F6.imprint","IMPRINT",EDGE,{"derivedFrom":sQuery(id+"F6.wireOp",EDGE,"E20.5.1.8")}),1.0]])]});
            var Q40;
            Q40=makeQuery(id+"F6.imprint","IMPRINT",FACE,{"disambiguationData":[TD([[makeQuery(id+"F6.imprint","IMPRINT",EDGE,{"derivedFrom":sQuery(id+"F6.wireOp",EDGE,"E20.4.2.0")}),1.0]])]});
            var Q41;
            {var subQ0=sQuery(id+"F6.wireOp",EDGE,"E20.6.1.11");Q41=makeQuery(id+"F6.imprint","IMPRINT",FACE,{"disambiguationData":[TD([[makeQuery(id+"F6.imprint","IMPRINT",EDGE,{"derivedFrom":subQ0}),1.0]])]});}
            var Q42;
            {var subQ1=sQuery(id+"F6.wireOp",EDGE,"E27.1.0.14");Q42=makeQuery(id+"F6.imprint","IMPRINT",FACE,{"disambiguationData":[TD([[makeQuery(id+"F6.imprint","IMPRINT",EDGE,{"derivedFrom":subQ1}),1.0]])]});}
            var Q43;
            {var subQ0=sQuery(id+"F6.wireOp",EDGE,"E28.1.0.4");Q43=makeQuery(id+"F6.imprint","IMPRINT",FACE,{"disambiguationData":[TD([[makeQuery(id+"F6.imprint","IMPRINT",EDGE,{"derivedFrom":subQ0}),1.0]])]});}
            var Q44;
            {var subQ0=sQuery(id+"F6.wireOp",EDGE,"E28.2.0.4");Q44=makeQuery(id+"F6.imprint","IMPRINT",FACE,{"disambiguationData":[TD([[makeQuery(id+"F6.imprint","IMPRINT",EDGE,{"derivedFrom":subQ0}),1.0]])]});}
            var Q45;
            {var subQ0=sQuery(id+"F6.wireOp",EDGE,"E28.3.0.4");Q45=makeQuery(id+"F6.imprint","IMPRINT",FACE,{"disambiguationData":[TD([[makeQuery(id+"F6.imprint","IMPRINT",EDGE,{"derivedFrom":subQ0}),1.0]])]});}
            var Q46;
            {var subQ0=sQuery(id+"F6.wireOp",EDGE,"E28.4.0.4");Q46=makeQuery(id+"F6.imprint","IMPRINT",FACE,{"disambiguationData":[TD([[makeQuery(id+"F6.imprint","IMPRINT",EDGE,{"derivedFrom":subQ0}),1.0]])]});}
            var Q47;
            {var subQ0=sQuery(id+"F6.wireOp",EDGE,"E28.5.0.4");Q47=makeQuery(id+"F6.imprint","IMPRINT",FACE,{"disambiguationData":[TD([[makeQuery(id+"F6.imprint","IMPRINT",EDGE,{"derivedFrom":subQ0}),1.0]])]});}
            var Q48;
            {var subQ0=sQuery(id+"F6.wireOp",EDGE,"E29");var subQ1=sQuery(id+"F6.wireOp",EDGE,"E25");var subQ2=makeQuery(id+"F6.imprint","INTERSECT",VERTEX,{"derivedFrom":[subQ1,subQ0]});Q48=makeQuery(id+"F6.imprint","IMPRINT",FACE,{"disambiguationData":[TD([[makeQuery(id+"F6.imprint","IMPRINT",EDGE,{"disambiguationData":[TD([[subQ2,1.0]])],"derivedFrom":subQ1}),1.0]])]});}
            extrude(context, id + "F7", {"entities" : qUnion([Q0, Q1, Q2, Q3, Q4, Q5, Q6, Q7, Q8, Q9, Q10, Q11, Q12, Q13, Q14, Q15, Q16, Q17, Q18, Q19, Q20, Q21, Q22, Q23, Q24, Q25, Q26, Q27, Q28, Q29, Q30, Q31, Q32, Q33, Q34, Q35, Q36, Q37, Q38, Q39, Q40, Q41, Q42, Q43, Q44, Q45, Q46, Q47, Q48]), "operationType" : NewBodyOperationType.REMOVE, "oppositeDirection" : true, "depth" : 100 * mm});
        }
        {
            var Q0;
            Q0=makeQuery(id+"F1.opExtrude","SWEPT_FACE",FACE,{"disambiguationData":[OSD([sQuery(id+"F0.wireOp",EDGE,"E0.top")])]});
            var sketch = newSketch(context, id + "F8", { "sketchPlane" : qUnion([Q0])});
            skLineSegment(sketch, "E30.bottom", {"start": v(10, -7.04) * mm, "end": v(70, -7.04) * mm});
            skLineSegment(sketch, "E30.top", {"start": v(10, -22.04) * mm, "end": v(70, -22.04) * mm});
            skLineSegment(sketch, "E30.left", {"start": v(10, -7.04) * mm, "end": v(10, -22.04) * mm});
            skLineSegment(sketch, "E30.right", {"start": v(70, -7.04) * mm, "end": v(70, -22.04) * mm});
            skCircle(sketch, "E31", {"center": v(40, -92.04) * mm, "radius": 1.75 * mm});
            skCircle(sketch, "E32", {"center": v(40, -107.04) * mm, "radius": 1.75 * mm});
            skSolve(sketch);
        }
        {
            var Q0;
            Q0=makeQuery(id+"F8.imprint","IMPRINT",FACE,{"disambiguationData":[TD([[makeQuery(id+"F8.imprint","IMPRINT",EDGE,{"derivedFrom":sQuery(id+"F8.wireOp",EDGE,"E30.bottom")}),-1.0]])]});
            var Q1;
            Q1=makeQuery(id+"F8.imprint","IMPRINT",FACE,{"disambiguationData":[TD([[makeQuery(id+"F8.imprint","IMPRINT",EDGE,{"derivedFrom":sQuery(id+"F8.wireOp",EDGE,"E31")}),1.0]])]});
            var Q2;
            Q2=makeQuery(id+"F8.imprint","IMPRINT",FACE,{"disambiguationData":[TD([[makeQuery(id+"F8.imprint","IMPRINT",EDGE,{"derivedFrom":sQuery(id+"F8.wireOp",EDGE,"E32")}),1.0]])]});
            extrude(context, id + "F9", {"entities" : qUnion([Q0, Q1, Q2]), "operationType" : NewBodyOperationType.REMOVE, "oppositeDirection" : true, "depth" : 5 * mm});
        }
        {
            var Q0;
            Q0=makeQuery(id+"F1.opExtrude","SWEPT_FACE",FACE,{"disambiguationData":[OSD([sQuery(id+"F0.wireOp",EDGE,"E0.right")])]});
            var sketch = newSketch(context, id + "F10", { "sketchPlane" : qUnion([Q0])});
            skLineSegment(sketch, "E33", {"start": v(-71.12, 56.93) * mm, "end": v(-77.8, 50.26) * mm});
            skLineSegment(sketch, "E34", {"start": v(-77.8, 44.55) * mm, "end": v(-71.12, 37.88) * mm});
            skLineSegment(sketch, "E35", {"start": v(-65.42, 37.88) * mm, "end": v(-58.75, 44.55) * mm});
            skLineSegment(sketch, "E36", {"start": v(-58.75, 50.26) * mm, "end": v(-65.42, 56.93) * mm});
            skArc(sketch, "E37", {"start": v(-65.42, 56.93) * mm, "mid": v(-68.27, 58.1) * mm, "end": v(-71.12, 56.93) * mm});
            skArc(sketch, "E38", {"start": v(-58.75, 44.55) * mm, "mid": v(-57.57, 47.4) * mm, "end": v(-58.75, 50.26) * mm});
            skArc(sketch, "E39", {"start": v(-77.8, 50.26) * mm, "mid": v(-78.97, 47.4) * mm, "end": v(-77.8, 44.55) * mm});
            skArc(sketch, "E40", {"start": v(-71.12, 37.88) * mm, "mid": v(-68.27, 36.7) * mm, "end": v(-65.42, 37.88) * mm});
            skLineSegment(sketch, "E41", {"start": v(-86.12, 41.93) * mm, "end": v(-92.8, 35.26) * mm});
            skLineSegment(sketch, "E42", {"start": v(-92.8, 29.55) * mm, "end": v(-86.12, 22.88) * mm});
            skLineSegment(sketch, "E43", {"start": v(-80.42, 22.88) * mm, "end": v(-73.75, 29.55) * mm});
            skLineSegment(sketch, "E44", {"start": v(-73.75, 35.26) * mm, "end": v(-80.42, 41.93) * mm});
            skArc(sketch, "E45", {"start": v(-80.42, 41.93) * mm, "mid": v(-83.27, 43.1) * mm, "end": v(-86.12, 41.93) * mm});
            skArc(sketch, "E46", {"start": v(-73.75, 29.55) * mm, "mid": v(-72.57, 32.4) * mm, "end": v(-73.75, 35.26) * mm});
            skArc(sketch, "E47", {"start": v(-92.8, 35.26) * mm, "mid": v(-93.97, 32.4) * mm, "end": v(-92.8, 29.55) * mm});
            skArc(sketch, "E48", {"start": v(-86.12, 22.88) * mm, "mid": v(-83.27, 21.7) * mm, "end": v(-80.42, 22.88) * mm});
            skLineSegment(sketch, "E49.0.1.0", {"start": v(-58.75, 20.26) * mm, "end": v(-65.42, 26.93) * mm});
            skArc(sketch, "E49.0.1.1", {"start": v(-58.75, 14.55) * mm, "mid": v(-57.57, 17.4) * mm, "end": v(-58.75, 20.26) * mm});
            skLineSegment(sketch, "E49.0.1.2", {"start": v(-65.42, 7.88) * mm, "end": v(-58.75, 14.55) * mm});
            skLineSegment(sketch, "E49.0.1.3", {"start": v(-77.8, 14.55) * mm, "end": v(-71.12, 7.88) * mm});
            skArc(sketch, "E49.0.1.4", {"start": v(-77.8, 20.26) * mm, "mid": v(-78.97, 17.4) * mm, "end": v(-77.8, 14.55) * mm});
            skLineSegment(sketch, "E49.0.1.5", {"start": v(-71.12, 26.93) * mm, "end": v(-77.8, 20.26) * mm});
            skArc(sketch, "E49.0.1.6", {"start": v(-65.42, 26.93) * mm, "mid": v(-68.27, 28.1) * mm, "end": v(-71.12, 26.93) * mm});
            skArc(sketch, "E49.0.1.7", {"start": v(-71.12, 7.88) * mm, "mid": v(-68.27, 6.7) * mm, "end": v(-65.42, 7.88) * mm});
            skArc(sketch, "E49.0.1.8", {"start": v(-73.75, -0.45) * mm, "mid": v(-72.57, 2.4) * mm, "end": v(-73.75, 5.26) * mm});
            skLineSegment(sketch, "E49.0.1.9", {"start": v(-80.42, -7.12) * mm, "end": v(-73.75, -0.45) * mm});
            skArc(sketch, "E49.0.1.10", {"start": v(-86.12, -7.12) * mm, "mid": v(-83.27, -8.3) * mm, "end": v(-80.42, -7.12) * mm});
            skLineSegment(sketch, "E49.0.1.11", {"start": v(-92.8, -0.45) * mm, "end": v(-86.12, -7.12) * mm});
            skArc(sketch, "E49.0.1.12", {"start": v(-92.8, 5.26) * mm, "mid": v(-93.97, 2.4) * mm, "end": v(-92.8, -0.45) * mm});
            skLineSegment(sketch, "E49.0.1.13", {"start": v(-86.12, 11.93) * mm, "end": v(-92.8, 5.26) * mm});
            skArc(sketch, "E49.0.1.14", {"start": v(-80.42, 11.93) * mm, "mid": v(-83.27, 13.1) * mm, "end": v(-86.12, 11.93) * mm});
            skLineSegment(sketch, "E49.0.1.15", {"start": v(-73.75, 5.26) * mm, "end": v(-80.42, 11.93) * mm});
            skLineSegment(sketch, "E49.0.2.0", {"start": v(-58.75, -9.74) * mm, "end": v(-65.42, -3.07) * mm});
            skArc(sketch, "E49.0.2.1", {"start": v(-58.75, -15.45) * mm, "mid": v(-57.57, -12.6) * mm, "end": v(-58.75, -9.74) * mm});
            skLineSegment(sketch, "E49.0.2.2", {"start": v(-65.42, -22.12) * mm, "end": v(-58.75, -15.45) * mm});
            skLineSegment(sketch, "E49.0.2.3", {"start": v(-77.8, -15.45) * mm, "end": v(-71.12, -22.12) * mm});
            skArc(sketch, "E49.0.2.4", {"start": v(-77.8, -9.74) * mm, "mid": v(-78.97, -12.6) * mm, "end": v(-77.8, -15.45) * mm});
            skLineSegment(sketch, "E49.0.2.5", {"start": v(-71.12, -3.07) * mm, "end": v(-77.8, -9.74) * mm});
            skArc(sketch, "E49.0.2.6", {"start": v(-65.42, -3.07) * mm, "mid": v(-68.27, -1.9) * mm, "end": v(-71.12, -3.07) * mm});
            skArc(sketch, "E49.0.2.7", {"start": v(-71.12, -22.12) * mm, "mid": v(-68.27, -23.3) * mm, "end": v(-65.42, -22.12) * mm});
            skArc(sketch, "E49.0.2.8", {"start": v(-73.75, -30.45) * mm, "mid": v(-72.57, -27.6) * mm, "end": v(-73.75, -24.74) * mm});
            skLineSegment(sketch, "E49.0.2.9", {"start": v(-80.42, -37.12) * mm, "end": v(-73.75, -30.45) * mm});
            skArc(sketch, "E49.0.2.10", {"start": v(-86.12, -37.12) * mm, "mid": v(-83.27, -38.3) * mm, "end": v(-80.42, -37.12) * mm});
            skLineSegment(sketch, "E49.0.2.11", {"start": v(-92.8, -30.45) * mm, "end": v(-86.12, -37.12) * mm});
            skArc(sketch, "E49.0.2.12", {"start": v(-92.8, -24.74) * mm, "mid": v(-93.97, -27.6) * mm, "end": v(-92.8, -30.45) * mm});
            skLineSegment(sketch, "E49.0.2.13", {"start": v(-86.12, -18.07) * mm, "end": v(-92.8, -24.74) * mm});
            skArc(sketch, "E49.0.2.14", {"start": v(-80.42, -18.07) * mm, "mid": v(-83.27, -16.9) * mm, "end": v(-86.12, -18.07) * mm});
            skLineSegment(sketch, "E49.0.2.15", {"start": v(-73.75, -24.74) * mm, "end": v(-80.42, -18.07) * mm});
            skLineSegment(sketch, "E49.0.3.0", {"start": v(-58.75, -39.74) * mm, "end": v(-65.42, -33.07) * mm});
            skArc(sketch, "E49.0.3.1", {"start": v(-58.75, -45.45) * mm, "mid": v(-57.57, -42.6) * mm, "end": v(-58.75, -39.74) * mm});
            skLineSegment(sketch, "E49.0.3.2", {"start": v(-65.42, -52.12) * mm, "end": v(-58.75, -45.45) * mm});
            skLineSegment(sketch, "E49.0.3.3", {"start": v(-77.8, -45.45) * mm, "end": v(-71.12, -52.12) * mm});
            skArc(sketch, "E49.0.3.4", {"start": v(-77.8, -39.74) * mm, "mid": v(-78.97, -42.6) * mm, "end": v(-77.8, -45.45) * mm});
            skLineSegment(sketch, "E49.0.3.5", {"start": v(-71.12, -33.07) * mm, "end": v(-77.8, -39.74) * mm});
            skArc(sketch, "E49.0.3.6", {"start": v(-65.42, -33.07) * mm, "mid": v(-68.27, -31.9) * mm, "end": v(-71.12, -33.07) * mm});
            skArc(sketch, "E49.0.3.7", {"start": v(-71.12, -52.12) * mm, "mid": v(-68.27, -53.3) * mm, "end": v(-65.42, -52.12) * mm});
            skArc(sketch, "E49.0.3.8", {"start": v(-73.75, -60.45) * mm, "mid": v(-72.57, -57.6) * mm, "end": v(-73.75, -54.74) * mm});
            skLineSegment(sketch, "E49.0.3.9", {"start": v(-80.42, -67.12) * mm, "end": v(-73.75, -60.45) * mm});
            skArc(sketch, "E49.0.3.10", {"start": v(-86.12, -67.12) * mm, "mid": v(-83.27, -68.3) * mm, "end": v(-80.42, -67.12) * mm});
            skLineSegment(sketch, "E49.0.3.11", {"start": v(-92.8, -60.45) * mm, "end": v(-86.12, -67.12) * mm});
            skArc(sketch, "E49.0.3.12", {"start": v(-92.8, -54.74) * mm, "mid": v(-93.97, -57.6) * mm, "end": v(-92.8, -60.45) * mm});
            skLineSegment(sketch, "E49.0.3.13", {"start": v(-86.12, -48.07) * mm, "end": v(-92.8, -54.74) * mm});
            skArc(sketch, "E49.0.3.14", {"start": v(-80.42, -48.07) * mm, "mid": v(-83.27, -46.9) * mm, "end": v(-86.12, -48.07) * mm});
            skLineSegment(sketch, "E49.0.3.15", {"start": v(-73.75, -54.74) * mm, "end": v(-80.42, -48.07) * mm});
            skLineSegment(sketch, "E49.1.0.0", {"start": v(-28.75, 50.26) * mm, "end": v(-35.42, 56.93) * mm});
            skArc(sketch, "E49.1.0.1", {"start": v(-28.75, 44.55) * mm, "mid": v(-27.57, 47.4) * mm, "end": v(-28.75, 50.26) * mm});
            skLineSegment(sketch, "E49.1.0.2", {"start": v(-35.42, 37.88) * mm, "end": v(-28.75, 44.55) * mm});
            skLineSegment(sketch, "E49.1.0.3", {"start": v(-47.8, 44.55) * mm, "end": v(-41.12, 37.88) * mm});
            skArc(sketch, "E49.1.0.4", {"start": v(-47.8, 50.26) * mm, "mid": v(-48.97, 47.4) * mm, "end": v(-47.8, 44.55) * mm});
            skLineSegment(sketch, "E49.1.0.5", {"start": v(-41.12, 56.93) * mm, "end": v(-47.8, 50.26) * mm});
            skArc(sketch, "E49.1.0.6", {"start": v(-35.42, 56.93) * mm, "mid": v(-38.27, 58.1) * mm, "end": v(-41.12, 56.93) * mm});
            skArc(sketch, "E49.1.0.7", {"start": v(-41.12, 37.88) * mm, "mid": v(-38.27, 36.7) * mm, "end": v(-35.42, 37.88) * mm});
            skArc(sketch, "E49.1.0.8", {"start": v(-43.75, 29.55) * mm, "mid": v(-42.57, 32.4) * mm, "end": v(-43.75, 35.26) * mm});
            skLineSegment(sketch, "E49.1.0.9", {"start": v(-50.42, 22.88) * mm, "end": v(-43.75, 29.55) * mm});
            skArc(sketch, "E49.1.0.10", {"start": v(-56.12, 22.88) * mm, "mid": v(-53.27, 21.7) * mm, "end": v(-50.42, 22.88) * mm});
            skLineSegment(sketch, "E49.1.0.11", {"start": v(-62.8, 29.55) * mm, "end": v(-56.12, 22.88) * mm});
            skArc(sketch, "E49.1.0.12", {"start": v(-62.8, 35.26) * mm, "mid": v(-63.97, 32.4) * mm, "end": v(-62.8, 29.55) * mm});
            skLineSegment(sketch, "E49.1.0.13", {"start": v(-56.12, 41.93) * mm, "end": v(-62.8, 35.26) * mm});
            skArc(sketch, "E49.1.0.14", {"start": v(-50.42, 41.93) * mm, "mid": v(-53.27, 43.1) * mm, "end": v(-56.12, 41.93) * mm});
            skLineSegment(sketch, "E49.1.0.15", {"start": v(-43.75, 35.26) * mm, "end": v(-50.42, 41.93) * mm});
            skLineSegment(sketch, "E49.1.1.0", {"start": v(-28.75, 20.26) * mm, "end": v(-35.42, 26.93) * mm});
            skArc(sketch, "E49.1.1.1", {"start": v(-28.75, 14.55) * mm, "mid": v(-27.57, 17.4) * mm, "end": v(-28.75, 20.26) * mm});
            skLineSegment(sketch, "E49.1.1.2", {"start": v(-35.42, 7.88) * mm, "end": v(-28.75, 14.55) * mm});
            skLineSegment(sketch, "E49.1.1.3", {"start": v(-47.8, 14.55) * mm, "end": v(-41.12, 7.88) * mm});
            skArc(sketch, "E49.1.1.4", {"start": v(-47.8, 20.26) * mm, "mid": v(-48.97, 17.4) * mm, "end": v(-47.8, 14.55) * mm});
            skLineSegment(sketch, "E49.1.1.5", {"start": v(-41.12, 26.93) * mm, "end": v(-47.8, 20.26) * mm});
            skArc(sketch, "E49.1.1.6", {"start": v(-35.42, 26.93) * mm, "mid": v(-38.27, 28.1) * mm, "end": v(-41.12, 26.93) * mm});
            skArc(sketch, "E49.1.1.7", {"start": v(-41.12, 7.88) * mm, "mid": v(-38.27, 6.7) * mm, "end": v(-35.42, 7.88) * mm});
            skArc(sketch, "E49.1.1.8", {"start": v(-43.75, -0.45) * mm, "mid": v(-42.57, 2.4) * mm, "end": v(-43.75, 5.26) * mm});
            skLineSegment(sketch, "E49.1.1.9", {"start": v(-50.42, -7.12) * mm, "end": v(-43.75, -0.45) * mm});
            skArc(sketch, "E49.1.1.10", {"start": v(-56.12, -7.12) * mm, "mid": v(-53.27, -8.3) * mm, "end": v(-50.42, -7.12) * mm});
            skLineSegment(sketch, "E49.1.1.11", {"start": v(-62.8, -0.45) * mm, "end": v(-56.12, -7.12) * mm});
            skArc(sketch, "E49.1.1.12", {"start": v(-62.8, 5.26) * mm, "mid": v(-63.97, 2.4) * mm, "end": v(-62.8, -0.45) * mm});
            skLineSegment(sketch, "E49.1.1.13", {"start": v(-56.12, 11.93) * mm, "end": v(-62.8, 5.26) * mm});
            skArc(sketch, "E49.1.1.14", {"start": v(-50.42, 11.93) * mm, "mid": v(-53.27, 13.1) * mm, "end": v(-56.12, 11.93) * mm});
            skLineSegment(sketch, "E49.1.1.15", {"start": v(-43.75, 5.26) * mm, "end": v(-50.42, 11.93) * mm});
            skLineSegment(sketch, "E49.1.2.0", {"start": v(-28.75, -9.74) * mm, "end": v(-35.42, -3.07) * mm});
            skArc(sketch, "E49.1.2.1", {"start": v(-28.75, -15.45) * mm, "mid": v(-27.57, -12.6) * mm, "end": v(-28.75, -9.74) * mm});
            skLineSegment(sketch, "E49.1.2.2", {"start": v(-35.42, -22.12) * mm, "end": v(-28.75, -15.45) * mm});
            skLineSegment(sketch, "E49.1.2.3", {"start": v(-47.8, -15.45) * mm, "end": v(-41.12, -22.12) * mm});
            skArc(sketch, "E49.1.2.4", {"start": v(-47.8, -9.74) * mm, "mid": v(-48.97, -12.6) * mm, "end": v(-47.8, -15.45) * mm});
            skLineSegment(sketch, "E49.1.2.5", {"start": v(-41.12, -3.07) * mm, "end": v(-47.8, -9.74) * mm});
            skArc(sketch, "E49.1.2.6", {"start": v(-35.42, -3.07) * mm, "mid": v(-38.27, -1.9) * mm, "end": v(-41.12, -3.07) * mm});
            skArc(sketch, "E49.1.2.7", {"start": v(-41.12, -22.12) * mm, "mid": v(-38.27, -23.3) * mm, "end": v(-35.42, -22.12) * mm});
            skArc(sketch, "E49.1.2.8", {"start": v(-43.75, -30.45) * mm, "mid": v(-42.57, -27.6) * mm, "end": v(-43.75, -24.74) * mm});
            skLineSegment(sketch, "E49.1.2.9", {"start": v(-50.42, -37.12) * mm, "end": v(-43.75, -30.45) * mm});
            skArc(sketch, "E49.1.2.10", {"start": v(-56.12, -37.12) * mm, "mid": v(-53.27, -38.3) * mm, "end": v(-50.42, -37.12) * mm});
            skLineSegment(sketch, "E49.1.2.11", {"start": v(-62.8, -30.45) * mm, "end": v(-56.12, -37.12) * mm});
            skArc(sketch, "E49.1.2.12", {"start": v(-62.8, -24.74) * mm, "mid": v(-63.97, -27.6) * mm, "end": v(-62.8, -30.45) * mm});
            skLineSegment(sketch, "E49.1.2.13", {"start": v(-56.12, -18.07) * mm, "end": v(-62.8, -24.74) * mm});
            skArc(sketch, "E49.1.2.14", {"start": v(-50.42, -18.07) * mm, "mid": v(-53.27, -16.9) * mm, "end": v(-56.12, -18.07) * mm});
            skLineSegment(sketch, "E49.1.2.15", {"start": v(-43.75, -24.74) * mm, "end": v(-50.42, -18.07) * mm});
            skLineSegment(sketch, "E49.1.3.0", {"start": v(-28.75, -39.74) * mm, "end": v(-35.42, -33.07) * mm});
            skArc(sketch, "E49.1.3.1", {"start": v(-28.75, -45.45) * mm, "mid": v(-27.57, -42.6) * mm, "end": v(-28.75, -39.74) * mm});
            skLineSegment(sketch, "E49.1.3.2", {"start": v(-35.42, -52.12) * mm, "end": v(-28.75, -45.45) * mm});
            skLineSegment(sketch, "E49.1.3.3", {"start": v(-47.8, -45.45) * mm, "end": v(-41.12, -52.12) * mm});
            skArc(sketch, "E49.1.3.4", {"start": v(-47.8, -39.74) * mm, "mid": v(-48.97, -42.6) * mm, "end": v(-47.8, -45.45) * mm});
            skLineSegment(sketch, "E49.1.3.5", {"start": v(-41.12, -33.07) * mm, "end": v(-47.8, -39.74) * mm});
            skArc(sketch, "E49.1.3.6", {"start": v(-35.42, -33.07) * mm, "mid": v(-38.27, -31.9) * mm, "end": v(-41.12, -33.07) * mm});
            skArc(sketch, "E49.1.3.7", {"start": v(-41.12, -52.12) * mm, "mid": v(-38.27, -53.3) * mm, "end": v(-35.42, -52.12) * mm});
            skArc(sketch, "E49.1.3.8", {"start": v(-43.75, -60.45) * mm, "mid": v(-42.57, -57.6) * mm, "end": v(-43.75, -54.74) * mm});
            skLineSegment(sketch, "E49.1.3.9", {"start": v(-50.42, -67.12) * mm, "end": v(-43.75, -60.45) * mm});
            skArc(sketch, "E49.1.3.10", {"start": v(-56.12, -67.12) * mm, "mid": v(-53.27, -68.3) * mm, "end": v(-50.42, -67.12) * mm});
            skLineSegment(sketch, "E49.1.3.11", {"start": v(-62.8, -60.45) * mm, "end": v(-56.12, -67.12) * mm});
            skArc(sketch, "E49.1.3.12", {"start": v(-62.8, -54.74) * mm, "mid": v(-63.97, -57.6) * mm, "end": v(-62.8, -60.45) * mm});
            skLineSegment(sketch, "E49.1.3.13", {"start": v(-56.12, -48.07) * mm, "end": v(-62.8, -54.74) * mm});
            skArc(sketch, "E49.1.3.14", {"start": v(-50.42, -48.07) * mm, "mid": v(-53.27, -46.9) * mm, "end": v(-56.12, -48.07) * mm});
            skLineSegment(sketch, "E49.1.3.15", {"start": v(-43.75, -54.74) * mm, "end": v(-50.42, -48.07) * mm});
            skLineSegment(sketch, "E49.2.0.0", {"start": v(1.25, 50.26) * mm, "end": v(-5.42, 56.93) * mm});
            skArc(sketch, "E49.2.0.1", {"start": v(1.25, 44.55) * mm, "mid": v(2.43, 47.4) * mm, "end": v(1.25, 50.26) * mm});
            skLineSegment(sketch, "E49.2.0.2", {"start": v(-5.42, 37.88) * mm, "end": v(1.25, 44.55) * mm});
            skLineSegment(sketch, "E49.2.0.3", {"start": v(-17.8, 44.55) * mm, "end": v(-11.12, 37.88) * mm});
            skArc(sketch, "E49.2.0.4", {"start": v(-17.8, 50.26) * mm, "mid": v(-18.97, 47.4) * mm, "end": v(-17.8, 44.55) * mm});
            skLineSegment(sketch, "E49.2.0.5", {"start": v(-11.12, 56.93) * mm, "end": v(-17.8, 50.26) * mm});
            skArc(sketch, "E49.2.0.6", {"start": v(-5.42, 56.93) * mm, "mid": v(-8.27, 58.1) * mm, "end": v(-11.12, 56.93) * mm});
            skArc(sketch, "E49.2.0.7", {"start": v(-11.12, 37.88) * mm, "mid": v(-8.27, 36.7) * mm, "end": v(-5.42, 37.88) * mm});
            skArc(sketch, "E49.2.0.8", {"start": v(-13.75, 29.55) * mm, "mid": v(-12.57, 32.4) * mm, "end": v(-13.75, 35.26) * mm});
            skLineSegment(sketch, "E49.2.0.9", {"start": v(-20.42, 22.88) * mm, "end": v(-13.75, 29.55) * mm});
            skArc(sketch, "E49.2.0.10", {"start": v(-26.12, 22.88) * mm, "mid": v(-23.27, 21.7) * mm, "end": v(-20.42, 22.88) * mm});
            skLineSegment(sketch, "E49.2.0.11", {"start": v(-32.8, 29.55) * mm, "end": v(-26.12, 22.88) * mm});
            skArc(sketch, "E49.2.0.12", {"start": v(-32.8, 35.26) * mm, "mid": v(-33.97, 32.4) * mm, "end": v(-32.8, 29.55) * mm});
            skLineSegment(sketch, "E49.2.0.13", {"start": v(-26.12, 41.93) * mm, "end": v(-32.8, 35.26) * mm});
            skArc(sketch, "E49.2.0.14", {"start": v(-20.42, 41.93) * mm, "mid": v(-23.27, 43.1) * mm, "end": v(-26.12, 41.93) * mm});
            skLineSegment(sketch, "E49.2.0.15", {"start": v(-13.75, 35.26) * mm, "end": v(-20.42, 41.93) * mm});
            skLineSegment(sketch, "E49.2.1.0", {"start": v(1.25, 20.26) * mm, "end": v(-5.42, 26.93) * mm});
            skArc(sketch, "E49.2.1.1", {"start": v(1.25, 14.55) * mm, "mid": v(2.43, 17.4) * mm, "end": v(1.25, 20.26) * mm});
            skLineSegment(sketch, "E49.2.1.2", {"start": v(-5.42, 7.88) * mm, "end": v(1.25, 14.55) * mm});
            skLineSegment(sketch, "E49.2.1.3", {"start": v(-17.8, 14.55) * mm, "end": v(-11.12, 7.88) * mm});
            skArc(sketch, "E49.2.1.4", {"start": v(-17.8, 20.26) * mm, "mid": v(-18.97, 17.4) * mm, "end": v(-17.8, 14.55) * mm});
            skLineSegment(sketch, "E49.2.1.5", {"start": v(-11.12, 26.93) * mm, "end": v(-17.8, 20.26) * mm});
            skArc(sketch, "E49.2.1.6", {"start": v(-5.42, 26.93) * mm, "mid": v(-8.27, 28.1) * mm, "end": v(-11.12, 26.93) * mm});
            skArc(sketch, "E49.2.1.7", {"start": v(-11.12, 7.88) * mm, "mid": v(-8.27, 6.7) * mm, "end": v(-5.42, 7.88) * mm});
            skArc(sketch, "E49.2.1.8", {"start": v(-13.75, -0.45) * mm, "mid": v(-12.57, 2.4) * mm, "end": v(-13.75, 5.26) * mm});
            skLineSegment(sketch, "E49.2.1.9", {"start": v(-20.42, -7.12) * mm, "end": v(-13.75, -0.45) * mm});
            skArc(sketch, "E49.2.1.10", {"start": v(-26.12, -7.12) * mm, "mid": v(-23.27, -8.3) * mm, "end": v(-20.42, -7.12) * mm});
            skLineSegment(sketch, "E49.2.1.11", {"start": v(-32.8, -0.45) * mm, "end": v(-26.12, -7.12) * mm});
            skArc(sketch, "E49.2.1.12", {"start": v(-32.8, 5.26) * mm, "mid": v(-33.97, 2.4) * mm, "end": v(-32.8, -0.45) * mm});
            skLineSegment(sketch, "E49.2.1.13", {"start": v(-26.12, 11.93) * mm, "end": v(-32.8, 5.26) * mm});
            skArc(sketch, "E49.2.1.14", {"start": v(-20.42, 11.93) * mm, "mid": v(-23.27, 13.1) * mm, "end": v(-26.12, 11.93) * mm});
            skLineSegment(sketch, "E49.2.1.15", {"start": v(-13.75, 5.26) * mm, "end": v(-20.42, 11.93) * mm});
            skLineSegment(sketch, "E49.2.2.0", {"start": v(1.25, -9.74) * mm, "end": v(-5.42, -3.07) * mm});
            skArc(sketch, "E49.2.2.1", {"start": v(1.25, -15.45) * mm, "mid": v(2.43, -12.6) * mm, "end": v(1.25, -9.74) * mm});
            skLineSegment(sketch, "E49.2.2.2", {"start": v(-5.42, -22.12) * mm, "end": v(1.25, -15.45) * mm});
            skLineSegment(sketch, "E49.2.2.3", {"start": v(-17.8, -15.45) * mm, "end": v(-11.12, -22.12) * mm});
            skArc(sketch, "E49.2.2.4", {"start": v(-17.8, -9.74) * mm, "mid": v(-18.97, -12.6) * mm, "end": v(-17.8, -15.45) * mm});
            skLineSegment(sketch, "E49.2.2.5", {"start": v(-11.12, -3.07) * mm, "end": v(-17.8, -9.74) * mm});
            skArc(sketch, "E49.2.2.6", {"start": v(-5.42, -3.07) * mm, "mid": v(-8.27, -1.9) * mm, "end": v(-11.12, -3.07) * mm});
            skArc(sketch, "E49.2.2.7", {"start": v(-11.12, -22.12) * mm, "mid": v(-8.27, -23.3) * mm, "end": v(-5.42, -22.12) * mm});
            skArc(sketch, "E49.2.2.8", {"start": v(-13.75, -30.45) * mm, "mid": v(-12.57, -27.6) * mm, "end": v(-13.75, -24.74) * mm});
            skLineSegment(sketch, "E49.2.2.9", {"start": v(-20.42, -37.12) * mm, "end": v(-13.75, -30.45) * mm});
            skArc(sketch, "E49.2.2.10", {"start": v(-26.12, -37.12) * mm, "mid": v(-23.27, -38.3) * mm, "end": v(-20.42, -37.12) * mm});
            skLineSegment(sketch, "E49.2.2.11", {"start": v(-32.8, -30.45) * mm, "end": v(-26.12, -37.12) * mm});
            skArc(sketch, "E49.2.2.12", {"start": v(-32.8, -24.74) * mm, "mid": v(-33.97, -27.6) * mm, "end": v(-32.8, -30.45) * mm});
            skLineSegment(sketch, "E49.2.2.13", {"start": v(-26.12, -18.07) * mm, "end": v(-32.8, -24.74) * mm});
            skArc(sketch, "E49.2.2.14", {"start": v(-20.42, -18.07) * mm, "mid": v(-23.27, -16.9) * mm, "end": v(-26.12, -18.07) * mm});
            skLineSegment(sketch, "E49.2.2.15", {"start": v(-13.75, -24.74) * mm, "end": v(-20.42, -18.07) * mm});
            skLineSegment(sketch, "E49.2.3.0", {"start": v(1.25, -39.74) * mm, "end": v(-5.42, -33.07) * mm});
            skArc(sketch, "E49.2.3.1", {"start": v(1.25, -45.45) * mm, "mid": v(2.43, -42.6) * mm, "end": v(1.25, -39.74) * mm});
            skLineSegment(sketch, "E49.2.3.2", {"start": v(-5.42, -52.12) * mm, "end": v(1.25, -45.45) * mm});
            skLineSegment(sketch, "E49.2.3.3", {"start": v(-17.8, -45.45) * mm, "end": v(-11.12, -52.12) * mm});
            skArc(sketch, "E49.2.3.4", {"start": v(-17.8, -39.74) * mm, "mid": v(-18.97, -42.6) * mm, "end": v(-17.8, -45.45) * mm});
            skLineSegment(sketch, "E49.2.3.5", {"start": v(-11.12, -33.07) * mm, "end": v(-17.8, -39.74) * mm});
            skArc(sketch, "E49.2.3.6", {"start": v(-5.42, -33.07) * mm, "mid": v(-8.27, -31.9) * mm, "end": v(-11.12, -33.07) * mm});
            skArc(sketch, "E49.2.3.7", {"start": v(-11.12, -52.12) * mm, "mid": v(-8.27, -53.3) * mm, "end": v(-5.42, -52.12) * mm});
            skArc(sketch, "E49.2.3.8", {"start": v(-13.75, -60.45) * mm, "mid": v(-12.57, -57.6) * mm, "end": v(-13.75, -54.74) * mm});
            skLineSegment(sketch, "E49.2.3.9", {"start": v(-20.42, -67.12) * mm, "end": v(-13.75, -60.45) * mm});
            skArc(sketch, "E49.2.3.10", {"start": v(-26.12, -67.12) * mm, "mid": v(-23.27, -68.3) * mm, "end": v(-20.42, -67.12) * mm});
            skLineSegment(sketch, "E49.2.3.11", {"start": v(-32.8, -60.45) * mm, "end": v(-26.12, -67.12) * mm});
            skArc(sketch, "E49.2.3.12", {"start": v(-32.8, -54.74) * mm, "mid": v(-33.97, -57.6) * mm, "end": v(-32.8, -60.45) * mm});
            skLineSegment(sketch, "E49.2.3.13", {"start": v(-26.12, -48.07) * mm, "end": v(-32.8, -54.74) * mm});
            skArc(sketch, "E49.2.3.14", {"start": v(-20.42, -48.07) * mm, "mid": v(-23.27, -46.9) * mm, "end": v(-26.12, -48.07) * mm});
            skLineSegment(sketch, "E49.2.3.15", {"start": v(-13.75, -54.74) * mm, "end": v(-20.42, -48.07) * mm});
            skLineSegment(sketch, "E49.3.0.0", {"start": v(31.25, 50.26) * mm, "end": v(24.58, 56.93) * mm});
            skArc(sketch, "E49.3.0.1", {"start": v(31.25, 44.55) * mm, "mid": v(32.43, 47.4) * mm, "end": v(31.25, 50.26) * mm});
            skLineSegment(sketch, "E49.3.0.2", {"start": v(24.58, 37.88) * mm, "end": v(31.25, 44.55) * mm});
            skLineSegment(sketch, "E49.3.0.3", {"start": v(12.2, 44.55) * mm, "end": v(18.88, 37.88) * mm});
            skArc(sketch, "E49.3.0.4", {"start": v(12.2, 50.26) * mm, "mid": v(11.03, 47.4) * mm, "end": v(12.2, 44.55) * mm});
            skLineSegment(sketch, "E49.3.0.5", {"start": v(18.88, 56.93) * mm, "end": v(12.2, 50.26) * mm});
            skArc(sketch, "E49.3.0.6", {"start": v(24.58, 56.93) * mm, "mid": v(21.73, 58.1) * mm, "end": v(18.88, 56.93) * mm});
            skArc(sketch, "E49.3.0.7", {"start": v(18.88, 37.88) * mm, "mid": v(21.73, 36.7) * mm, "end": v(24.58, 37.88) * mm});
            skArc(sketch, "E49.3.0.8", {"start": v(16.25, 29.55) * mm, "mid": v(17.43, 32.4) * mm, "end": v(16.25, 35.26) * mm});
            skLineSegment(sketch, "E49.3.0.9", {"start": v(9.58, 22.88) * mm, "end": v(16.25, 29.55) * mm});
            skArc(sketch, "E49.3.0.10", {"start": v(3.88, 22.88) * mm, "mid": v(6.73, 21.7) * mm, "end": v(9.58, 22.88) * mm});
            skLineSegment(sketch, "E49.3.0.11", {"start": v(-2.8, 29.55) * mm, "end": v(3.88, 22.88) * mm});
            skArc(sketch, "E49.3.0.12", {"start": v(-2.8, 35.26) * mm, "mid": v(-3.97, 32.4) * mm, "end": v(-2.8, 29.55) * mm});
            skLineSegment(sketch, "E49.3.0.13", {"start": v(3.88, 41.93) * mm, "end": v(-2.8, 35.26) * mm});
            skArc(sketch, "E49.3.0.14", {"start": v(9.58, 41.93) * mm, "mid": v(6.73, 43.1) * mm, "end": v(3.88, 41.93) * mm});
            skLineSegment(sketch, "E49.3.0.15", {"start": v(16.25, 35.26) * mm, "end": v(9.58, 41.93) * mm});
            skLineSegment(sketch, "E49.3.1.0", {"start": v(31.25, 20.26) * mm, "end": v(24.58, 26.93) * mm});
            skArc(sketch, "E49.3.1.1", {"start": v(31.25, 14.55) * mm, "mid": v(32.43, 17.4) * mm, "end": v(31.25, 20.26) * mm});
            skLineSegment(sketch, "E49.3.1.2", {"start": v(24.58, 7.88) * mm, "end": v(31.25, 14.55) * mm});
            skLineSegment(sketch, "E49.3.1.3", {"start": v(12.2, 14.55) * mm, "end": v(18.88, 7.88) * mm});
            skArc(sketch, "E49.3.1.4", {"start": v(12.2, 20.26) * mm, "mid": v(11.03, 17.4) * mm, "end": v(12.2, 14.55) * mm});
            skLineSegment(sketch, "E49.3.1.5", {"start": v(18.88, 26.93) * mm, "end": v(12.2, 20.26) * mm});
            skArc(sketch, "E49.3.1.6", {"start": v(24.58, 26.93) * mm, "mid": v(21.73, 28.1) * mm, "end": v(18.88, 26.93) * mm});
            skArc(sketch, "E49.3.1.7", {"start": v(18.88, 7.88) * mm, "mid": v(21.73, 6.7) * mm, "end": v(24.58, 7.88) * mm});
            skArc(sketch, "E49.3.1.8", {"start": v(16.25, -0.45) * mm, "mid": v(17.43, 2.4) * mm, "end": v(16.25, 5.26) * mm});
            skLineSegment(sketch, "E49.3.1.9", {"start": v(9.58, -7.12) * mm, "end": v(16.25, -0.45) * mm});
            skArc(sketch, "E49.3.1.10", {"start": v(3.88, -7.12) * mm, "mid": v(6.73, -8.3) * mm, "end": v(9.58, -7.12) * mm});
            skLineSegment(sketch, "E49.3.1.11", {"start": v(-2.8, -0.45) * mm, "end": v(3.88, -7.12) * mm});
            skArc(sketch, "E49.3.1.12", {"start": v(-2.8, 5.26) * mm, "mid": v(-3.97, 2.4) * mm, "end": v(-2.8, -0.45) * mm});
            skLineSegment(sketch, "E49.3.1.13", {"start": v(3.88, 11.93) * mm, "end": v(-2.8, 5.26) * mm});
            skArc(sketch, "E49.3.1.14", {"start": v(9.58, 11.93) * mm, "mid": v(6.73, 13.1) * mm, "end": v(3.88, 11.93) * mm});
            skLineSegment(sketch, "E49.3.1.15", {"start": v(16.25, 5.26) * mm, "end": v(9.58, 11.93) * mm});
            skLineSegment(sketch, "E49.3.2.0", {"start": v(31.25, -9.74) * mm, "end": v(24.58, -3.07) * mm});
            skArc(sketch, "E49.3.2.1", {"start": v(31.25, -15.45) * mm, "mid": v(32.43, -12.6) * mm, "end": v(31.25, -9.74) * mm});
            skLineSegment(sketch, "E49.3.2.2", {"start": v(24.58, -22.12) * mm, "end": v(31.25, -15.45) * mm});
            skLineSegment(sketch, "E49.3.2.3", {"start": v(12.2, -15.45) * mm, "end": v(18.88, -22.12) * mm});
            skArc(sketch, "E49.3.2.4", {"start": v(12.2, -9.74) * mm, "mid": v(11.03, -12.6) * mm, "end": v(12.2, -15.45) * mm});
            skLineSegment(sketch, "E49.3.2.5", {"start": v(18.88, -3.07) * mm, "end": v(12.2, -9.74) * mm});
            skArc(sketch, "E49.3.2.6", {"start": v(24.58, -3.07) * mm, "mid": v(21.73, -1.9) * mm, "end": v(18.88, -3.07) * mm});
            skArc(sketch, "E49.3.2.7", {"start": v(18.88, -22.12) * mm, "mid": v(21.73, -23.3) * mm, "end": v(24.58, -22.12) * mm});
            skArc(sketch, "E49.3.2.8", {"start": v(16.25, -30.45) * mm, "mid": v(17.43, -27.6) * mm, "end": v(16.25, -24.74) * mm});
            skLineSegment(sketch, "E49.3.2.9", {"start": v(9.58, -37.12) * mm, "end": v(16.25, -30.45) * mm});
            skArc(sketch, "E49.3.2.10", {"start": v(3.88, -37.12) * mm, "mid": v(6.73, -38.3) * mm, "end": v(9.58, -37.12) * mm});
            skLineSegment(sketch, "E49.3.2.11", {"start": v(-2.8, -30.45) * mm, "end": v(3.88, -37.12) * mm});
            skArc(sketch, "E49.3.2.12", {"start": v(-2.8, -24.74) * mm, "mid": v(-3.97, -27.6) * mm, "end": v(-2.8, -30.45) * mm});
            skLineSegment(sketch, "E49.3.2.13", {"start": v(3.88, -18.07) * mm, "end": v(-2.8, -24.74) * mm});
            skArc(sketch, "E49.3.2.14", {"start": v(9.58, -18.07) * mm, "mid": v(6.73, -16.9) * mm, "end": v(3.88, -18.07) * mm});
            skLineSegment(sketch, "E49.3.2.15", {"start": v(16.25, -24.74) * mm, "end": v(9.58, -18.07) * mm});
            skLineSegment(sketch, "E49.3.3.0", {"start": v(31.25, -39.74) * mm, "end": v(24.58, -33.07) * mm});
            skArc(sketch, "E49.3.3.1", {"start": v(31.25, -45.45) * mm, "mid": v(32.43, -42.6) * mm, "end": v(31.25, -39.74) * mm});
            skLineSegment(sketch, "E49.3.3.2", {"start": v(24.58, -52.12) * mm, "end": v(31.25, -45.45) * mm});
            skLineSegment(sketch, "E49.3.3.3", {"start": v(12.2, -45.45) * mm, "end": v(18.88, -52.12) * mm});
            skArc(sketch, "E49.3.3.4", {"start": v(12.2, -39.74) * mm, "mid": v(11.03, -42.6) * mm, "end": v(12.2, -45.45) * mm});
            skLineSegment(sketch, "E49.3.3.5", {"start": v(18.88, -33.07) * mm, "end": v(12.2, -39.74) * mm});
            skArc(sketch, "E49.3.3.6", {"start": v(24.58, -33.07) * mm, "mid": v(21.73, -31.9) * mm, "end": v(18.88, -33.07) * mm});
            skArc(sketch, "E49.3.3.7", {"start": v(18.88, -52.12) * mm, "mid": v(21.73, -53.3) * mm, "end": v(24.58, -52.12) * mm});
            skArc(sketch, "E49.3.3.8", {"start": v(16.25, -60.45) * mm, "mid": v(17.43, -57.6) * mm, "end": v(16.25, -54.74) * mm});
            skLineSegment(sketch, "E49.3.3.9", {"start": v(9.58, -67.12) * mm, "end": v(16.25, -60.45) * mm});
            skArc(sketch, "E49.3.3.10", {"start": v(3.88, -67.12) * mm, "mid": v(6.73, -68.3) * mm, "end": v(9.58, -67.12) * mm});
            skLineSegment(sketch, "E49.3.3.11", {"start": v(-2.8, -60.45) * mm, "end": v(3.88, -67.12) * mm});
            skArc(sketch, "E49.3.3.12", {"start": v(-2.8, -54.74) * mm, "mid": v(-3.97, -57.6) * mm, "end": v(-2.8, -60.45) * mm});
            skLineSegment(sketch, "E49.3.3.13", {"start": v(3.88, -48.07) * mm, "end": v(-2.8, -54.74) * mm});
            skArc(sketch, "E49.3.3.14", {"start": v(9.58, -48.07) * mm, "mid": v(6.73, -46.9) * mm, "end": v(3.88, -48.07) * mm});
            skLineSegment(sketch, "E49.3.3.15", {"start": v(16.25, -54.74) * mm, "end": v(9.58, -48.07) * mm});
            skLineSegment(sketch, "E49.direction1", {"start": v(-58.75, 50.26) * mm, "end": v(-28.75, 50.26) * mm, "construction": true});
            skLineSegment(sketch, "E49.direction2", {"start": v(-58.75, 50.26) * mm, "end": v(-58.75, 20.26) * mm, "construction": true});
            skLineSegment(sketch, "E50.bottom", {"start": v(-77.5, 61.03) * mm, "end": v(-2.5, 61.03) * mm});
            skLineSegment(sketch, "E50.top", {"start": v(-77.5, -56.47) * mm, "end": v(-2.5, -56.47) * mm});
            skLineSegment(sketch, "E50.left", {"start": v(-77.5, 61.03) * mm, "end": v(-77.5, -56.47) * mm});
            skLineSegment(sketch, "E50.right", {"start": v(-2.5, 61.03) * mm, "end": v(-2.5, -56.47) * mm});
            skLineSegment(sketch, "E51", {"start": v(-77.5, -13.97) * mm, "end": v(-2.5, -13.97) * mm});
            skSolve(sketch);
        }
        {
            var Q0;
            Q0=makeQuery(id+"F10.imprint","IMPRINT",FACE,{"disambiguationData":[TD([[makeQuery(id+"F10.imprint","IMPRINT",EDGE,{"derivedFrom":sQuery(id+"F10.wireOp",EDGE,"E35")}),1.0]])]});
            var Q1;
            Q1=makeQuery(id+"F10.imprint","IMPRINT",FACE,{"disambiguationData":[TD([[makeQuery(id+"F10.imprint","IMPRINT",EDGE,{"derivedFrom":sQuery(id+"F10.wireOp",EDGE,"E49.1.0.0")}),1.0]])]});
            var Q2;
            Q2=makeQuery(id+"F10.imprint","IMPRINT",FACE,{"disambiguationData":[TD([[makeQuery(id+"F10.imprint","IMPRINT",EDGE,{"derivedFrom":sQuery(id+"F10.wireOp",EDGE,"E49.2.0.3")}),1.0]])]});
            var Q3;
            Q3=makeQuery(id+"F10.imprint","IMPRINT",FACE,{"disambiguationData":[TD([[makeQuery(id+"F10.imprint","IMPRINT",EDGE,{"derivedFrom":sQuery(id+"F10.wireOp",EDGE,"E49.2.0.8")}),1.0]])]});
            var Q4;
            Q4=makeQuery(id+"F10.imprint","IMPRINT",FACE,{"disambiguationData":[TD([[makeQuery(id+"F10.imprint","IMPRINT",EDGE,{"derivedFrom":sQuery(id+"F10.wireOp",EDGE,"E49.1.0.8")}),1.0]])]});
            var Q5;
            {var subQ0=sQuery(id+"F10.wireOp",EDGE,"E46");Q5=makeQuery(id+"F10.imprint","IMPRINT",FACE,{"disambiguationData":[TD([[makeQuery(id+"F10.imprint","IMPRINT",EDGE,{"derivedFrom":subQ0}),1.0]])]});}
            var Q6;
            Q6=makeQuery(id+"F10.imprint","IMPRINT",FACE,{"disambiguationData":[TD([[makeQuery(id+"F10.imprint","IMPRINT",EDGE,{"derivedFrom":sQuery(id+"F10.wireOp",EDGE,"E49.0.1.0")}),1.0]])]});
            var Q7;
            Q7=makeQuery(id+"F10.imprint","IMPRINT",FACE,{"disambiguationData":[TD([[makeQuery(id+"F10.imprint","IMPRINT",EDGE,{"derivedFrom":sQuery(id+"F10.wireOp",EDGE,"E49.1.1.0")}),1.0]])]});
            var Q8;
            Q8=makeQuery(id+"F10.imprint","IMPRINT",FACE,{"disambiguationData":[TD([[makeQuery(id+"F10.imprint","IMPRINT",EDGE,{"derivedFrom":sQuery(id+"F10.wireOp",EDGE,"E49.2.1.3")}),1.0]])]});
            var Q9;
            Q9=makeQuery(id+"F10.imprint","IMPRINT",FACE,{"disambiguationData":[TD([[makeQuery(id+"F10.imprint","IMPRINT",EDGE,{"derivedFrom":sQuery(id+"F10.wireOp",EDGE,"E49.2.1.8")}),1.0]])]});
            var Q10;
            Q10=makeQuery(id+"F10.imprint","IMPRINT",FACE,{"disambiguationData":[TD([[makeQuery(id+"F10.imprint","IMPRINT",EDGE,{"derivedFrom":sQuery(id+"F10.wireOp",EDGE,"E49.1.1.8")}),1.0]])]});
            var Q11;
            {var subQ0=sQuery(id+"F10.wireOp",EDGE,"E49.0.1.8");Q11=makeQuery(id+"F10.imprint","IMPRINT",FACE,{"disambiguationData":[TD([[makeQuery(id+"F10.imprint","IMPRINT",EDGE,{"derivedFrom":subQ0}),1.0]])]});}
            var Q12;
            Q12=makeQuery(id+"F10.imprint","IMPRINT",FACE,{"disambiguationData":[TD([[makeQuery(id+"F10.imprint","IMPRINT",EDGE,{"derivedFrom":sQuery(id+"F10.wireOp",EDGE,"E49.0.2.0")}),1.0]])]});
            var Q13;
            {var subQ0=sQuery(id+"F10.wireOp",EDGE,"E49.0.2.8");Q13=makeQuery(id+"F10.imprint","IMPRINT",FACE,{"disambiguationData":[TD([[makeQuery(id+"F10.imprint","IMPRINT",EDGE,{"derivedFrom":subQ0}),1.0]])]});}
            var Q14;
            Q14=makeQuery(id+"F10.imprint","IMPRINT",FACE,{"disambiguationData":[TD([[makeQuery(id+"F10.imprint","IMPRINT",EDGE,{"derivedFrom":sQuery(id+"F10.wireOp",EDGE,"E49.0.3.0")}),1.0]])]});
            var Q15;
            {var subQ0=sQuery(id+"F10.wireOp",EDGE,"E49.0.3.15");var subQ1=sQuery(id+"F10.wireOp",EDGE,"E49.0.3.8");var subQ2=makeQuery(id+"F10.imprint","INTERSECT",VERTEX,{"derivedFrom":[subQ1,subQ0]});Q15=makeQuery(id+"F10.imprint","IMPRINT",FACE,{"disambiguationData":[TD([[makeQuery(id+"F10.imprint","IMPRINT",EDGE,{"disambiguationData":[TD([[subQ2,1.0]])],"derivedFrom":subQ1}),1.0]])]});}
            var Q16;
            {var subQ0=sQuery(id+"F10.wireOp",EDGE,"E49.1.3.13");Q16=makeQuery(id+"F10.imprint","IMPRINT",FACE,{"disambiguationData":[TD([[makeQuery(id+"F10.imprint","IMPRINT",EDGE,{"derivedFrom":subQ0}),1.0]])]});}
            var Q17;
            Q17=makeQuery(id+"F10.imprint","IMPRINT",FACE,{"disambiguationData":[TD([[makeQuery(id+"F10.imprint","IMPRINT",EDGE,{"derivedFrom":sQuery(id+"F10.wireOp",EDGE,"E49.1.3.0")}),1.0]])]});
            var Q18;
            Q18=makeQuery(id+"F10.imprint","IMPRINT",FACE,{"disambiguationData":[TD([[makeQuery(id+"F10.imprint","IMPRINT",EDGE,{"derivedFrom":sQuery(id+"F10.wireOp",EDGE,"E49.2.3.3")}),1.0]])]});
            var Q19;
            Q19=makeQuery(id+"F10.imprint","IMPRINT",FACE,{"disambiguationData":[TD([[makeQuery(id+"F10.imprint","IMPRINT",EDGE,{"derivedFrom":sQuery(id+"F10.wireOp",EDGE,"E49.2.2.3")}),1.0]])]});
            var Q20;
            Q20=makeQuery(id+"F10.imprint","IMPRINT",FACE,{"disambiguationData":[TD([[makeQuery(id+"F10.imprint","IMPRINT",EDGE,{"derivedFrom":sQuery(id+"F10.wireOp",EDGE,"E49.1.2.8")}),1.0]])]});
            var Q21;
            Q21=makeQuery(id+"F10.imprint","IMPRINT",FACE,{"disambiguationData":[TD([[makeQuery(id+"F10.imprint","IMPRINT",EDGE,{"derivedFrom":sQuery(id+"F10.wireOp",EDGE,"E49.1.2.0")}),1.0]])]});
            var Q22;
            Q22=makeQuery(id+"F10.imprint","IMPRINT",FACE,{"disambiguationData":[TD([[makeQuery(id+"F10.imprint","IMPRINT",EDGE,{"derivedFrom":sQuery(id+"F10.wireOp",EDGE,"E49.2.2.8")}),1.0]])]});
            var Q23;
            {var subQ0=sQuery(id+"F10.wireOp",EDGE,"E49.3.0.12");Q23=makeQuery(id+"F10.imprint","IMPRINT",FACE,{"disambiguationData":[TD([[makeQuery(id+"F10.imprint","IMPRINT",EDGE,{"derivedFrom":subQ0}),1.0]])]});}
            var Q24;
            {var subQ0=sQuery(id+"F10.wireOp",EDGE,"E49.3.1.12");Q24=makeQuery(id+"F10.imprint","IMPRINT",FACE,{"disambiguationData":[TD([[makeQuery(id+"F10.imprint","IMPRINT",EDGE,{"derivedFrom":subQ0}),1.0]])]});}
            var Q25;
            {var subQ0=sQuery(id+"F10.wireOp",EDGE,"E49.3.2.12");Q25=makeQuery(id+"F10.imprint","IMPRINT",FACE,{"disambiguationData":[TD([[makeQuery(id+"F10.imprint","IMPRINT",EDGE,{"derivedFrom":subQ0}),1.0]])]});}
            var Q26;
            {var subQ0=sQuery(id+"F10.wireOp",EDGE,"E49.2.3.13");Q26=makeQuery(id+"F10.imprint","IMPRINT",FACE,{"disambiguationData":[TD([[makeQuery(id+"F10.imprint","IMPRINT",EDGE,{"derivedFrom":subQ0}),1.0]])]});}
            var Q27;
            {var subQ0=sQuery(id+"F10.wireOp",EDGE,"E49.3.3.13");var subQ1=sQuery(id+"F10.wireOp",EDGE,"E49.3.3.12");var subQ2=makeQuery(id+"F10.imprint","INTERSECT",VERTEX,{"derivedFrom":[subQ1,subQ0]});Q27=makeQuery(id+"F10.imprint","IMPRINT",FACE,{"disambiguationData":[TD([[makeQuery(id+"F10.imprint","IMPRINT",EDGE,{"disambiguationData":[TD([[subQ2,-1.0]])],"derivedFrom":subQ1}),1.0]])]});}
            var Q28;
            {var subQ4=sQuery(id+"F10.wireOp",EDGE,"E49.0.2.2");Q28=makeQuery(id+"F10.imprint","IMPRINT",FACE,{"disambiguationData":[TD([[makeQuery(id+"F10.imprint","IMPRINT",EDGE,{"derivedFrom":subQ4}),1.0]])]});}
            var Q29;
            {var subQ1=sQuery(id+"F10.wireOp",EDGE,"E49.1.2.2");Q29=makeQuery(id+"F10.imprint","IMPRINT",FACE,{"disambiguationData":[TD([[makeQuery(id+"F10.imprint","IMPRINT",EDGE,{"derivedFrom":subQ1}),1.0]])]});}
            var Q30;
            {var subQ1=sQuery(id+"F10.wireOp",EDGE,"E49.2.2.5");Q30=makeQuery(id+"F10.imprint","IMPRINT",FACE,{"disambiguationData":[TD([[makeQuery(id+"F10.imprint","IMPRINT",EDGE,{"derivedFrom":subQ1}),1.0]])]});}
            extrude(context, id + "F11", {"entities" : qUnion([Q0, Q1, Q2, Q3, Q4, Q5, Q6, Q7, Q8, Q9, Q10, Q11, Q12, Q13, Q14, Q15, Q16, Q17, Q18, Q19, Q20, Q21, Q22, Q23, Q24, Q25, Q26, Q27, Q28, Q29, Q30]), "operationType" : NewBodyOperationType.REMOVE, "oppositeDirection" : true, "depth" : 25 * mm});
        }
        {
            var Q0;
            Q0=makeQuery(id+"F1.opExtrude","SWEPT_FACE",FACE,{"disambiguationData":[OSD([sQuery(id+"F0.wireOp",EDGE,"E0.left")])]});
            var sketch = newSketch(context, id + "F12", { "sketchPlane" : qUnion([Q0])});
            skLineSegment(sketch, "E52", {"start": v(9.14, 57.02) * mm, "end": v(2.47, 50.35) * mm});
            skLineSegment(sketch, "E53", {"start": v(2.47, 44.64) * mm, "end": v(9.14, 37.97) * mm});
            skLineSegment(sketch, "E54", {"start": v(14.84, 37.97) * mm, "end": v(21.51, 44.64) * mm});
            skLineSegment(sketch, "E55", {"start": v(21.51, 50.35) * mm, "end": v(14.84, 57.02) * mm});
            skArc(sketch, "E56", {"start": v(14.84, 57.02) * mm, "mid": v(11.99, 58.2) * mm, "end": v(9.14, 57.02) * mm});
            skArc(sketch, "E57", {"start": v(21.51, 44.64) * mm, "mid": v(22.7, 47.5) * mm, "end": v(21.51, 50.35) * mm});
            skArc(sketch, "E58", {"start": v(2.47, 50.35) * mm, "mid": v(1.29, 47.5) * mm, "end": v(2.47, 44.64) * mm});
            skArc(sketch, "E59", {"start": v(9.14, 37.97) * mm, "mid": v(11.99, 36.8) * mm, "end": v(14.84, 37.97) * mm});
            skLineSegment(sketch, "E60", {"start": v(-0.16, 22.97) * mm, "end": v(6.51, 29.64) * mm});
            skLineSegment(sketch, "E61", {"start": v(6.51, 35.35) * mm, "end": v(-0.16, 42.02) * mm});
            skArc(sketch, "E62", {"start": v(6.51, 29.64) * mm, "mid": v(7.7, 32.5) * mm, "end": v(6.51, 35.35) * mm});
            skLineSegment(sketch, "E63.0.1.0", {"start": v(21.51, 20.35) * mm, "end": v(14.84, 27.02) * mm});
            skArc(sketch, "E63.0.1.1", {"start": v(21.51, 14.64) * mm, "mid": v(22.7, 17.5) * mm, "end": v(21.51, 20.35) * mm});
            skLineSegment(sketch, "E63.0.1.2", {"start": v(14.84, 7.97) * mm, "end": v(21.51, 14.64) * mm});
            skLineSegment(sketch, "E63.0.1.3", {"start": v(2.47, 14.64) * mm, "end": v(9.14, 7.97) * mm});
            skArc(sketch, "E63.0.1.4", {"start": v(2.47, 20.35) * mm, "mid": v(1.29, 17.5) * mm, "end": v(2.47, 14.64) * mm});
            skLineSegment(sketch, "E63.0.1.5", {"start": v(9.14, 27.02) * mm, "end": v(2.47, 20.35) * mm});
            skArc(sketch, "E63.0.1.6", {"start": v(14.84, 27.02) * mm, "mid": v(11.99, 28.2) * mm, "end": v(9.14, 27.02) * mm});
            skArc(sketch, "E63.0.1.7", {"start": v(9.14, 7.97) * mm, "mid": v(11.99, 6.8) * mm, "end": v(14.84, 7.97) * mm});
            skArc(sketch, "E63.0.1.8", {"start": v(6.51, -0.36) * mm, "mid": v(7.7, 2.5) * mm, "end": v(6.51, 5.35) * mm});
            skLineSegment(sketch, "E63.0.1.9", {"start": v(-0.16, -7.03) * mm, "end": v(6.51, -0.36) * mm});
            skLineSegment(sketch, "E63.0.1.15", {"start": v(6.51, 5.35) * mm, "end": v(-0.16, 12.02) * mm});
            skLineSegment(sketch, "E63.0.2.0", {"start": v(21.51, -9.65) * mm, "end": v(14.84, -2.98) * mm});
            skArc(sketch, "E63.0.2.1", {"start": v(21.51, -15.36) * mm, "mid": v(22.7, -12.5) * mm, "end": v(21.51, -9.65) * mm});
            skLineSegment(sketch, "E63.0.2.2", {"start": v(14.84, -22.03) * mm, "end": v(21.51, -15.36) * mm});
            skLineSegment(sketch, "E63.0.2.3", {"start": v(2.47, -15.36) * mm, "end": v(9.14, -22.03) * mm});
            skArc(sketch, "E63.0.2.4", {"start": v(2.47, -9.65) * mm, "mid": v(1.29, -12.5) * mm, "end": v(2.47, -15.36) * mm});
            skLineSegment(sketch, "E63.0.2.5", {"start": v(9.14, -2.98) * mm, "end": v(2.47, -9.65) * mm});
            skArc(sketch, "E63.0.2.6", {"start": v(14.84, -2.98) * mm, "mid": v(11.99, -1.8) * mm, "end": v(9.14, -2.98) * mm});
            skArc(sketch, "E63.0.2.7", {"start": v(9.14, -22.03) * mm, "mid": v(11.99, -23.2) * mm, "end": v(14.84, -22.03) * mm});
            skLineSegment(sketch, "E63.1.0.0", {"start": v(51.51, 50.35) * mm, "end": v(44.84, 57.02) * mm});
            skArc(sketch, "E63.1.0.1", {"start": v(51.51, 44.64) * mm, "mid": v(52.7, 47.5) * mm, "end": v(51.51, 50.35) * mm});
            skLineSegment(sketch, "E63.1.0.2", {"start": v(44.84, 37.97) * mm, "end": v(51.51, 44.64) * mm});
            skLineSegment(sketch, "E63.1.0.3", {"start": v(32.47, 44.64) * mm, "end": v(39.14, 37.97) * mm});
            skArc(sketch, "E63.1.0.4", {"start": v(32.47, 50.35) * mm, "mid": v(31.29, 47.5) * mm, "end": v(32.47, 44.64) * mm});
            skLineSegment(sketch, "E63.1.0.5", {"start": v(39.14, 57.02) * mm, "end": v(32.47, 50.35) * mm});
            skArc(sketch, "E63.1.0.6", {"start": v(44.84, 57.02) * mm, "mid": v(41.99, 58.2) * mm, "end": v(39.14, 57.02) * mm});
            skArc(sketch, "E63.1.0.7", {"start": v(39.14, 37.97) * mm, "mid": v(41.99, 36.8) * mm, "end": v(44.84, 37.97) * mm});
            skArc(sketch, "E63.1.0.8", {"start": v(36.51, 29.64) * mm, "mid": v(37.7, 32.5) * mm, "end": v(36.51, 35.35) * mm});
            skLineSegment(sketch, "E63.1.0.9", {"start": v(29.84, 22.97) * mm, "end": v(36.51, 29.64) * mm});
            skArc(sketch, "E63.1.0.10", {"start": v(24.14, 22.97) * mm, "mid": v(26.99, 21.8) * mm, "end": v(29.84, 22.97) * mm});
            skLineSegment(sketch, "E63.1.0.11", {"start": v(17.47, 29.64) * mm, "end": v(24.14, 22.97) * mm});
            skArc(sketch, "E63.1.0.12", {"start": v(17.47, 35.35) * mm, "mid": v(16.29, 32.5) * mm, "end": v(17.47, 29.64) * mm});
            skLineSegment(sketch, "E63.1.0.13", {"start": v(24.14, 42.02) * mm, "end": v(17.47, 35.35) * mm});
            skArc(sketch, "E63.1.0.14", {"start": v(29.84, 42.02) * mm, "mid": v(26.99, 43.2) * mm, "end": v(24.14, 42.02) * mm});
            skLineSegment(sketch, "E63.1.0.15", {"start": v(36.51, 35.35) * mm, "end": v(29.84, 42.02) * mm});
            skLineSegment(sketch, "E63.1.1.0", {"start": v(51.51, 20.35) * mm, "end": v(44.84, 27.02) * mm});
            skArc(sketch, "E63.1.1.1", {"start": v(51.51, 14.64) * mm, "mid": v(52.7, 17.5) * mm, "end": v(51.51, 20.35) * mm});
            skLineSegment(sketch, "E63.1.1.2", {"start": v(44.84, 7.97) * mm, "end": v(51.51, 14.64) * mm});
            skLineSegment(sketch, "E63.1.1.3", {"start": v(32.47, 14.64) * mm, "end": v(39.14, 7.97) * mm});
            skArc(sketch, "E63.1.1.4", {"start": v(32.47, 20.35) * mm, "mid": v(31.29, 17.5) * mm, "end": v(32.47, 14.64) * mm});
            skLineSegment(sketch, "E63.1.1.5", {"start": v(39.14, 27.02) * mm, "end": v(32.47, 20.35) * mm});
            skArc(sketch, "E63.1.1.6", {"start": v(44.84, 27.02) * mm, "mid": v(41.99, 28.2) * mm, "end": v(39.14, 27.02) * mm});
            skArc(sketch, "E63.1.1.7", {"start": v(39.14, 7.97) * mm, "mid": v(41.99, 6.8) * mm, "end": v(44.84, 7.97) * mm});
            skArc(sketch, "E63.1.1.8", {"start": v(36.51, -0.36) * mm, "mid": v(37.7, 2.5) * mm, "end": v(36.51, 5.35) * mm});
            skLineSegment(sketch, "E63.1.1.9", {"start": v(29.84, -7.03) * mm, "end": v(36.51, -0.36) * mm});
            skArc(sketch, "E63.1.1.10", {"start": v(24.14, -7.03) * mm, "mid": v(26.99, -8.2) * mm, "end": v(29.84, -7.03) * mm});
            skLineSegment(sketch, "E63.1.1.11", {"start": v(17.47, -0.36) * mm, "end": v(24.14, -7.03) * mm});
            skArc(sketch, "E63.1.1.12", {"start": v(17.47, 5.35) * mm, "mid": v(16.29, 2.5) * mm, "end": v(17.47, -0.36) * mm});
            skLineSegment(sketch, "E63.1.1.13", {"start": v(24.14, 12.02) * mm, "end": v(17.47, 5.35) * mm});
            skArc(sketch, "E63.1.1.14", {"start": v(29.84, 12.02) * mm, "mid": v(26.99, 13.2) * mm, "end": v(24.14, 12.02) * mm});
            skLineSegment(sketch, "E63.1.1.15", {"start": v(36.51, 5.35) * mm, "end": v(29.84, 12.02) * mm});
            skLineSegment(sketch, "E63.1.2.0", {"start": v(51.51, -9.65) * mm, "end": v(44.84, -2.98) * mm});
            skArc(sketch, "E63.1.2.1", {"start": v(51.51, -15.36) * mm, "mid": v(52.7, -12.5) * mm, "end": v(51.51, -9.65) * mm});
            skLineSegment(sketch, "E63.1.2.2", {"start": v(44.84, -22.03) * mm, "end": v(51.51, -15.36) * mm});
            skLineSegment(sketch, "E63.1.2.3", {"start": v(32.47, -15.36) * mm, "end": v(39.14, -22.03) * mm});
            skArc(sketch, "E63.1.2.4", {"start": v(32.47, -9.65) * mm, "mid": v(31.29, -12.5) * mm, "end": v(32.47, -15.36) * mm});
            skLineSegment(sketch, "E63.1.2.5", {"start": v(39.14, -2.98) * mm, "end": v(32.47, -9.65) * mm});
            skArc(sketch, "E63.1.2.6", {"start": v(44.84, -2.98) * mm, "mid": v(41.99, -1.8) * mm, "end": v(39.14, -2.98) * mm});
            skArc(sketch, "E63.1.2.7", {"start": v(39.14, -22.03) * mm, "mid": v(41.99, -23.2) * mm, "end": v(44.84, -22.03) * mm});
            skArc(sketch, "E63.1.2.14", {"start": v(29.84, -17.98) * mm, "mid": v(26.99, -16.8) * mm, "end": v(24.14, -17.98) * mm});
            skLineSegment(sketch, "E63.2.0.0", {"start": v(81.51, 50.35) * mm, "end": v(74.84, 57.02) * mm});
            skLineSegment(sketch, "E63.2.0.2", {"start": v(74.84, 37.97) * mm, "end": v(81.51, 44.64) * mm});
            skLineSegment(sketch, "E63.2.0.3", {"start": v(62.47, 44.64) * mm, "end": v(69.14, 37.97) * mm});
            skArc(sketch, "E63.2.0.4", {"start": v(62.47, 50.35) * mm, "mid": v(61.29, 47.5) * mm, "end": v(62.47, 44.64) * mm});
            skLineSegment(sketch, "E63.2.0.5", {"start": v(69.14, 57.02) * mm, "end": v(62.47, 50.35) * mm});
            skArc(sketch, "E63.2.0.6", {"start": v(74.84, 57.02) * mm, "mid": v(71.99, 58.2) * mm, "end": v(69.14, 57.02) * mm});
            skArc(sketch, "E63.2.0.7", {"start": v(69.14, 37.97) * mm, "mid": v(71.99, 36.8) * mm, "end": v(74.84, 37.97) * mm});
            skArc(sketch, "E63.2.0.8", {"start": v(66.51, 29.64) * mm, "mid": v(67.7, 32.5) * mm, "end": v(66.51, 35.35) * mm});
            skLineSegment(sketch, "E63.2.0.9", {"start": v(59.84, 22.97) * mm, "end": v(66.51, 29.64) * mm});
            skArc(sketch, "E63.2.0.10", {"start": v(54.14, 22.97) * mm, "mid": v(56.99, 21.8) * mm, "end": v(59.84, 22.97) * mm});
            skLineSegment(sketch, "E63.2.0.11", {"start": v(47.47, 29.64) * mm, "end": v(54.14, 22.97) * mm});
            skArc(sketch, "E63.2.0.12", {"start": v(47.47, 35.35) * mm, "mid": v(46.29, 32.5) * mm, "end": v(47.47, 29.64) * mm});
            skLineSegment(sketch, "E63.2.0.13", {"start": v(54.14, 42.02) * mm, "end": v(47.47, 35.35) * mm});
            skArc(sketch, "E63.2.0.14", {"start": v(59.84, 42.02) * mm, "mid": v(56.99, 43.2) * mm, "end": v(54.14, 42.02) * mm});
            skLineSegment(sketch, "E63.2.0.15", {"start": v(66.51, 35.35) * mm, "end": v(59.84, 42.02) * mm});
            skLineSegment(sketch, "E63.2.1.0", {"start": v(81.51, 20.35) * mm, "end": v(74.84, 27.02) * mm});
            skLineSegment(sketch, "E63.2.1.2", {"start": v(74.84, 7.97) * mm, "end": v(81.51, 14.64) * mm});
            skLineSegment(sketch, "E63.2.1.3", {"start": v(62.47, 14.64) * mm, "end": v(69.14, 7.97) * mm});
            skArc(sketch, "E63.2.1.4", {"start": v(62.47, 20.35) * mm, "mid": v(61.29, 17.5) * mm, "end": v(62.47, 14.64) * mm});
            skLineSegment(sketch, "E63.2.1.5", {"start": v(69.14, 27.02) * mm, "end": v(62.47, 20.35) * mm});
            skArc(sketch, "E63.2.1.6", {"start": v(74.84, 27.02) * mm, "mid": v(71.99, 28.2) * mm, "end": v(69.14, 27.02) * mm});
            skArc(sketch, "E63.2.1.7", {"start": v(69.14, 7.97) * mm, "mid": v(71.99, 6.8) * mm, "end": v(74.84, 7.97) * mm});
            skArc(sketch, "E63.2.1.8", {"start": v(66.51, -0.36) * mm, "mid": v(67.7, 2.5) * mm, "end": v(66.51, 5.35) * mm});
            skLineSegment(sketch, "E63.2.1.9", {"start": v(59.84, -7.03) * mm, "end": v(66.51, -0.36) * mm});
            skArc(sketch, "E63.2.1.10", {"start": v(54.14, -7.03) * mm, "mid": v(56.99, -8.2) * mm, "end": v(59.84, -7.03) * mm});
            skLineSegment(sketch, "E63.2.1.11", {"start": v(47.47, -0.36) * mm, "end": v(54.14, -7.03) * mm});
            skArc(sketch, "E63.2.1.12", {"start": v(47.47, 5.35) * mm, "mid": v(46.29, 2.5) * mm, "end": v(47.47, -0.36) * mm});
            skLineSegment(sketch, "E63.2.1.13", {"start": v(54.14, 12.02) * mm, "end": v(47.47, 5.35) * mm});
            skArc(sketch, "E63.2.1.14", {"start": v(59.84, 12.02) * mm, "mid": v(56.99, 13.2) * mm, "end": v(54.14, 12.02) * mm});
            skLineSegment(sketch, "E63.2.1.15", {"start": v(66.51, 5.35) * mm, "end": v(59.84, 12.02) * mm});
            skLineSegment(sketch, "E63.2.2.0", {"start": v(81.51, -9.65) * mm, "end": v(74.84, -2.98) * mm});
            skLineSegment(sketch, "E63.2.2.2", {"start": v(74.84, -22.03) * mm, "end": v(81.51, -15.36) * mm});
            skLineSegment(sketch, "E63.2.2.3", {"start": v(62.47, -15.36) * mm, "end": v(69.14, -22.03) * mm});
            skArc(sketch, "E63.2.2.4", {"start": v(62.47, -9.65) * mm, "mid": v(61.29, -12.5) * mm, "end": v(62.47, -15.36) * mm});
            skLineSegment(sketch, "E63.2.2.5", {"start": v(69.14, -2.98) * mm, "end": v(62.47, -9.65) * mm});
            skArc(sketch, "E63.2.2.6", {"start": v(74.84, -2.98) * mm, "mid": v(71.99, -1.8) * mm, "end": v(69.14, -2.98) * mm});
            skArc(sketch, "E63.2.2.7", {"start": v(69.14, -22.03) * mm, "mid": v(71.99, -23.2) * mm, "end": v(74.84, -22.03) * mm});
            skArc(sketch, "E63.2.2.14", {"start": v(59.84, -17.98) * mm, "mid": v(56.99, -16.8) * mm, "end": v(54.14, -17.98) * mm});
            skArc(sketch, "E63.3.0.12", {"start": v(77.47, 35.35) * mm, "mid": v(76.29, 32.5) * mm, "end": v(77.47, 29.64) * mm});
            skArc(sketch, "E63.3.1.12", {"start": v(77.47, 5.35) * mm, "mid": v(76.29, 2.5) * mm, "end": v(77.47, -0.36) * mm});
            skLineSegment(sketch, "E63.direction1", {"start": v(21.51, 50.35) * mm, "end": v(51.51, 50.35) * mm, "construction": true});
            skLineSegment(sketch, "E63.direction2", {"start": v(21.51, 50.35) * mm, "end": v(21.51, 20.35) * mm, "construction": true});
            skLineSegment(sketch, "E64.bottom", {"start": v(2.5, 61.12) * mm, "end": v(77.5, 61.12) * mm});
            skLineSegment(sketch, "E65", {"start": v(2.5, -13.97) * mm, "end": v(77.5, -13.97) * mm});
            skLineSegment(sketch, "E66", {"start": v(2.5, -13.97) * mm, "end": v(2.5, 61.12) * mm});
            skLineSegment(sketch, "E67", {"start": v(77.5, 61.12) * mm, "end": v(77.5, -13.97) * mm});
            skLineSegment(sketch, "E68", {"start": v(77.47, 5.35) * mm, "end": v(84, 11.87) * mm});
            skLineSegment(sketch, "E69", {"start": v(77.47, -0.36) * mm, "end": v(83.43, -6.32) * mm});
            skPoint(sketch, "E69.endSnap0", {"position": v(65.8, -6.32) * mm});
            skLineSegment(sketch, "E70", {"start": v(77.47, 29.64) * mm, "end": v(83.5, 23.6) * mm});
            skLineSegment(sketch, "E71", {"start": v(77.47, 35.35) * mm, "end": v(83.88, 41.76) * mm});
            skSolve(sketch);
        }
        {
            var Q0;
            {var subQ7=sQuery(id+"F12.wireOp",EDGE,"E63.0.2.0");Q0=makeQuery(id+"F12.imprint","IMPRINT",FACE,{"disambiguationData":[TD([[makeQuery(id+"F12.imprint","IMPRINT",EDGE,{"derivedFrom":subQ7}),1.0]])]});}
            var Q1;
            {var subQ0=sQuery(id+"F12.wireOp",EDGE,"E63.0.1.8");Q1=makeQuery(id+"F12.imprint","IMPRINT",FACE,{"disambiguationData":[TD([[makeQuery(id+"F12.imprint","IMPRINT",EDGE,{"derivedFrom":subQ0}),1.0]])]});}
            var Q2;
            Q2=makeQuery(id+"F12.imprint","IMPRINT",FACE,{"disambiguationData":[TD([[makeQuery(id+"F12.imprint","IMPRINT",EDGE,{"derivedFrom":sQuery(id+"F12.wireOp",EDGE,"E63.0.1.0")}),1.0]])]});
            var Q3;
            {var subQ0=sQuery(id+"F12.wireOp",EDGE,"E62");Q3=makeQuery(id+"F12.imprint","IMPRINT",FACE,{"disambiguationData":[TD([[makeQuery(id+"F12.imprint","IMPRINT",EDGE,{"derivedFrom":subQ0}),1.0]])]});}
            var Q4;
            Q4=makeQuery(id+"F12.imprint","IMPRINT",FACE,{"disambiguationData":[TD([[makeQuery(id+"F12.imprint","IMPRINT",EDGE,{"derivedFrom":sQuery(id+"F12.wireOp",EDGE,"E54")}),1.0]])]});
            var Q5;
            Q5=makeQuery(id+"F12.imprint","IMPRINT",FACE,{"disambiguationData":[TD([[makeQuery(id+"F12.imprint","IMPRINT",EDGE,{"derivedFrom":sQuery(id+"F12.wireOp",EDGE,"E63.1.0.0")}),1.0]])]});
            var Q6;
            Q6=makeQuery(id+"F12.imprint","IMPRINT",FACE,{"disambiguationData":[TD([[makeQuery(id+"F12.imprint","IMPRINT",EDGE,{"derivedFrom":sQuery(id+"F12.wireOp",EDGE,"E63.1.0.8")}),1.0]])]});
            var Q7;
            Q7=makeQuery(id+"F12.imprint","IMPRINT",FACE,{"disambiguationData":[TD([[makeQuery(id+"F12.imprint","IMPRINT",EDGE,{"derivedFrom":sQuery(id+"F12.wireOp",EDGE,"E63.1.1.0")}),1.0]])]});
            var Q8;
            Q8=makeQuery(id+"F12.imprint","IMPRINT",FACE,{"disambiguationData":[TD([[makeQuery(id+"F12.imprint","IMPRINT",EDGE,{"derivedFrom":sQuery(id+"F12.wireOp",EDGE,"E63.1.1.8")}),1.0]])]});
            var Q9;
            {var subQ5=sQuery(id+"F12.wireOp",EDGE,"E63.1.2.0");Q9=makeQuery(id+"F12.imprint","IMPRINT",FACE,{"disambiguationData":[TD([[makeQuery(id+"F12.imprint","IMPRINT",EDGE,{"derivedFrom":subQ5}),1.0]])]});}
            var Q10;
            Q10=makeQuery(id+"F12.imprint","IMPRINT",FACE,{"disambiguationData":[TD([[makeQuery(id+"F12.imprint","IMPRINT",EDGE,{"derivedFrom":sQuery(id+"F12.wireOp",EDGE,"E63.2.1.8")}),1.0]])]});
            var Q11;
            Q11=makeQuery(id+"F12.imprint","IMPRINT",FACE,{"disambiguationData":[TD([[makeQuery(id+"F12.imprint","IMPRINT",EDGE,{"derivedFrom":sQuery(id+"F12.wireOp",EDGE,"E63.2.0.8")}),1.0]])]});
            var Q12;
            Q12=makeQuery(id+"F12.imprint","IMPRINT",FACE,{"disambiguationData":[TD([[makeQuery(id+"F12.imprint","IMPRINT",EDGE,{"derivedFrom":sQuery(id+"F12.wireOp",EDGE,"E63.2.1.3")}),1.0]])]});
            var Q13;
            {var subQ1=sQuery(id+"F12.wireOp",EDGE,"E63.2.2.5");Q13=makeQuery(id+"F12.imprint","IMPRINT",FACE,{"disambiguationData":[TD([[makeQuery(id+"F12.imprint","IMPRINT",EDGE,{"derivedFrom":subQ1}),1.0]])]});}
            var Q14;
            Q14=makeQuery(id+"F12.imprint","IMPRINT",FACE,{"disambiguationData":[TD([[makeQuery(id+"F12.imprint","IMPRINT",EDGE,{"derivedFrom":sQuery(id+"F12.wireOp",EDGE,"E63.2.0.3")}),1.0]])]});
            var Q15;
            {var subQ0=sQuery(id+"F12.wireOp",EDGE,"E63.3.1.12");Q15=makeQuery(id+"F12.imprint","IMPRINT",FACE,{"disambiguationData":[TD([[makeQuery(id+"F12.imprint","IMPRINT",EDGE,{"derivedFrom":subQ0}),1.0]])]});}
            var Q16;
            {var subQ0=sQuery(id+"F12.wireOp",EDGE,"E63.3.0.12");Q16=makeQuery(id+"F12.imprint","IMPRINT",FACE,{"disambiguationData":[TD([[makeQuery(id+"F12.imprint","IMPRINT",EDGE,{"derivedFrom":subQ0}),1.0]])]});}
            extrude(context, id + "F13", {"entities" : qUnion([Q0, Q1, Q2, Q3, Q4, Q5, Q6, Q7, Q8, Q9, Q10, Q11, Q12, Q13, Q14, Q15, Q16]), "operationType" : NewBodyOperationType.REMOVE, "oppositeDirection" : true, "depth" : 25 * mm});
        }
        {
            var Q0;
            Q0=makeQuery(id+"F1.opExtrude","SWEPT_FACE",FACE,{"disambiguationData":[OSD([sQuery(id+"F0.wireOp",EDGE,"E0.bottom")])]});
            var sketch = newSketch(context, id + "F14", { "sketchPlane" : qUnion([Q0])});
            skLineSegment(sketch, "E72.bottom", {"start": v(2.5, 114.54) * mm, "end": v(77.5, 114.54) * mm});
            skLineSegment(sketch, "E72.top", {"start": v(2.5, -60.46) * mm, "end": v(77.5, -60.46) * mm});
            skLineSegment(sketch, "E72.left", {"start": v(2.5, 114.54) * mm, "end": v(2.5, -60.46) * mm});
            skLineSegment(sketch, "E72.right", {"start": v(77.5, 114.54) * mm, "end": v(77.5, -60.46) * mm});
            skSolve(sketch);
        }
        {
            var Q0;
            Q0=makeQuery(id+"F14.imprint","IMPRINT",FACE,{"disambiguationData":[TD([[makeQuery(id+"F14.imprint","IMPRINT",EDGE,{"derivedFrom":sQuery(id+"F14.wireOp",EDGE,"E72.bottom")}),-1.0]])]});
            extrude(context, id + "F15", {"entities" : qUnion([Q0]), "operationType" : NewBodyOperationType.REMOVE, "oppositeDirection" : true, "depth" : 117.5 * mm});
        }
        {
            var Q0;
            {var subQ0=sQuery(id+"F10.wireOp",EDGE,"E50.top");var subQ1=sQuery(id+"F6.wireOp",EDGE,"E24");Q0=makeQuery(id+"F15.boolean.opBoolean","MERGE",FACE,{"derivedFrom":[makeQuery(id+"F5.boolean.opBoolean","COPY",FACE,{"derivedFrom":makeQuery(id+"F5.opExtrude","SWEPT_FACE",FACE,{"disambiguationData":[OSD([sQuery(id+"F4.wireOp",EDGE,"E3.top")])]})}),makeQuery(id+"F11.boolean.opBoolean","MERGE",FACE,{"derivedFrom":[makeQuery(id+"F7.boolean.opBoolean","MERGE",FACE,{"derivedFrom":[makeQuery(id+"F3.boolean.opBoolean","COPY",FACE,{"derivedFrom":makeQuery(id+"F3.opExtrude","SWEPT_FACE",FACE,{"disambiguationData":[OSD([sQuery(id+"F2.wireOp",EDGE,"E2.top")])]})}),makeQuery(id+"F7.opExtrude","SWEPT_FACE",FACE,{"disambiguationData":[OSD([subQ1]),TDD([makeQuery(id+"F6.imprint","IMPRINT",EDGE,{"disambiguationData":[TD([[makeQuery(id+"F6.imprint","INTERSECT",VERTEX,{"derivedFrom":[sQuery(id+"F6.wireOp",EDGE,"E23"),subQ1]}),-1.0]])],"derivedFrom":subQ1})])]}),makeQuery(id+"F7.opExtrude","SWEPT_FACE",FACE,{"disambiguationData":[OSD([subQ1]),TDD([makeQuery(id+"F6.imprint","IMPRINT",EDGE,{"disambiguationData":[TD([[makeQuery(id+"F6.imprint","INTERSECT",VERTEX,{"derivedFrom":[sQuery(id+"F6.wireOp",EDGE,"E20.4.3.8"),subQ1]}),1.0]])],"derivedFrom":subQ1})])]}),makeQuery(id+"F7.opExtrude","SWEPT_FACE",FACE,{"disambiguationData":[OSD([subQ1]),TDD([makeQuery(id+"F6.imprint","IMPRINT",EDGE,{"disambiguationData":[TD([[makeQuery(id+"F6.imprint","INTERSECT",VERTEX,{"derivedFrom":[sQuery(id+"F6.wireOp",EDGE,"E20.5.3.8"),subQ1]}),1.0]])],"derivedFrom":subQ1})])]})]}),makeQuery(id+"F11.opExtrude","SWEPT_FACE",FACE,{"disambiguationData":[OSD([subQ0]),TDD([makeQuery(id+"F10.imprint","IMPRINT",EDGE,{"disambiguationData":[TD([[makeQuery(id+"F10.imprint","INTERSECT",VERTEX,{"derivedFrom":[subQ0,sQuery(id+"F10.wireOp",EDGE,"E50.left")]}),-1.0]])],"derivedFrom":subQ0})])]}),makeQuery(id+"F11.opExtrude","SWEPT_FACE",FACE,{"disambiguationData":[OSD([subQ0]),TDD([makeQuery(id+"F10.imprint","IMPRINT",EDGE,{"disambiguationData":[TD([[makeQuery(id+"F10.imprint","INTERSECT",VERTEX,{"derivedFrom":[sQuery(id+"F10.wireOp",EDGE,"E49.1.3.8"),subQ0]}),1.0]])],"derivedFrom":subQ0})])]}),makeQuery(id+"F11.opExtrude","SWEPT_FACE",FACE,{"disambiguationData":[OSD([subQ0]),TDD([makeQuery(id+"F10.imprint","IMPRINT",EDGE,{"disambiguationData":[TD([[makeQuery(id+"F10.imprint","INTERSECT",VERTEX,{"derivedFrom":[sQuery(id+"F10.wireOp",EDGE,"E49.2.3.8"),subQ0]}),1.0]])],"derivedFrom":subQ0})])]}),makeQuery(id+"F11.opExtrude","SWEPT_FACE",FACE,{"disambiguationData":[OSD([subQ0]),TDD([makeQuery(id+"F10.imprint","IMPRINT",EDGE,{"disambiguationData":[TD([[makeQuery(id+"F10.imprint","INTERSECT",VERTEX,{"derivedFrom":[subQ0,sQuery(id+"F10.wireOp",EDGE,"E50.right")]}),1.0]])],"derivedFrom":subQ0})])]})]}),makeQuery(id+"F15.opExtrude","CAP_FACE",FACE,{"disambiguationData":[OSD([sQuery(id+"F14.wireOp",EDGE,"E72.bottom"),sQuery(id+"F14.wireOp",EDGE,"E72.top"),sQuery(id+"F14.wireOp",EDGE,"E72.left"),sQuery(id+"F14.wireOp",EDGE,"E72.right")])],"isStart":false})]});}
            var sketch = newSketch(context, id + "F16", { "sketchPlane" : qUnion([Q0])});
            skLineSegment(sketch, "E73.bottom", {"start": v(2.5, 27.04) * mm, "end": v(77.5, 27.04) * mm});
            skLineSegment(sketch, "E73.top", {"start": v(2.5, 24.54) * mm, "end": v(77.5, 24.54) * mm});
            skLineSegment(sketch, "E73.left", {"start": v(2.5, 27.04) * mm, "end": v(2.5, 24.54) * mm});
            skLineSegment(sketch, "E73.right", {"start": v(77.5, 27.04) * mm, "end": v(77.5, 24.54) * mm});
            skSolve(sketch);
        }
        {
            var Q0;
            Q0=makeQuery(id+"F16.imprint","IMPRINT",FACE,{"disambiguationData":[TD([[makeQuery(id+"F16.imprint","IMPRINT",EDGE,{"derivedFrom":sQuery(id+"F16.wireOp",EDGE,"E73.bottom")}),-1.0]])]});
            extrude(context, id + "F17", {"entities" : qUnion([Q0]), "operationType" : NewBodyOperationType.REMOVE, "oppositeDirection" : true, "depth" : 1.25 * mm});
        }
        {
            var Q0;
            {var subQ0=sQuery(id+"F6.wireOp",EDGE,"E21");Q0=makeQuery(id+"F15.boolean.opBoolean","MERGE",FACE,{"derivedFrom":[makeQuery(id+"F7.boolean.opBoolean","MERGE",FACE,{"derivedFrom":[makeQuery(id+"F3.boolean.opBoolean","COPY",FACE,{"derivedFrom":makeQuery(id+"F3.opExtrude","SWEPT_FACE",FACE,{"disambiguationData":[OSD([sQuery(id+"F2.wireOp",EDGE,"E1.left")])]})}),makeQuery(id+"F7.opExtrude","SWEPT_FACE",FACE,{"disambiguationData":[OSD([subQ0]),TDD([makeQuery(id+"F6.imprint","IMPRINT",EDGE,{"disambiguationData":[TD([[makeQuery(id+"F6.imprint","INTERSECT",VERTEX,{"derivedFrom":[subQ0,sQuery(id+"F6.wireOp",EDGE,"E29")]}),-1.0]])],"derivedFrom":subQ0})])]}),makeQuery(id+"F7.opExtrude","SWEPT_FACE",FACE,{"disambiguationData":[OSD([subQ0]),TDD([makeQuery(id+"F6.imprint","IMPRINT",EDGE,{"disambiguationData":[TD([[makeQuery(id+"F6.imprint","INTERSECT",VERTEX,{"derivedFrom":[sQuery(id+"F6.wireOp",EDGE,"E16"),subQ0]}),-1.0]])],"derivedFrom":subQ0})])]}),makeQuery(id+"F7.opExtrude","SWEPT_FACE",FACE,{"disambiguationData":[OSD([subQ0]),TDD([makeQuery(id+"F6.imprint","IMPRINT",EDGE,{"disambiguationData":[TD([[makeQuery(id+"F6.imprint","INTERSECT",VERTEX,{"derivedFrom":[sQuery(id+"F6.wireOp",EDGE,"E20.0.1.9"),subQ0]}),-1.0]])],"derivedFrom":subQ0})])]})]}),makeQuery(id+"F15.opExtrude","SWEPT_FACE",FACE,{"disambiguationData":[OSD([sQuery(id+"F14.wireOp",EDGE,"E72.top")])]})]});}
            var sketch = newSketch(context, id + "F18", { "sketchPlane" : qUnion([Q0])});
            skLineSegment(sketch, "E74.bottom", {"start": v(-77.5, -13.97) * mm, "end": v(-2.5, -13.97) * mm});
            skLineSegment(sketch, "E74.top", {"start": v(-77.5, -16.47) * mm, "end": v(-2.5, -16.47) * mm});
            skLineSegment(sketch, "E74.left", {"start": v(-77.5, -13.97) * mm, "end": v(-77.5, -16.47) * mm});
            skLineSegment(sketch, "E74.right", {"start": v(-2.5, -13.97) * mm, "end": v(-2.5, -16.47) * mm});
            skSolve(sketch);
        }
        {
            var Q0;
            Q0=makeQuery(id+"F18.imprint","IMPRINT",FACE,{"disambiguationData":[TD([[makeQuery(id+"F18.imprint","IMPRINT",EDGE,{"derivedFrom":sQuery(id+"F18.wireOp",EDGE,"E74.top")}),1.0]])]});
            extrude(context, id + "F19", {"entities" : qUnion([Q0]), "operationType" : NewBodyOperationType.REMOVE, "oppositeDirection" : true, "depth" : 1.25 * mm});
        }
    });
